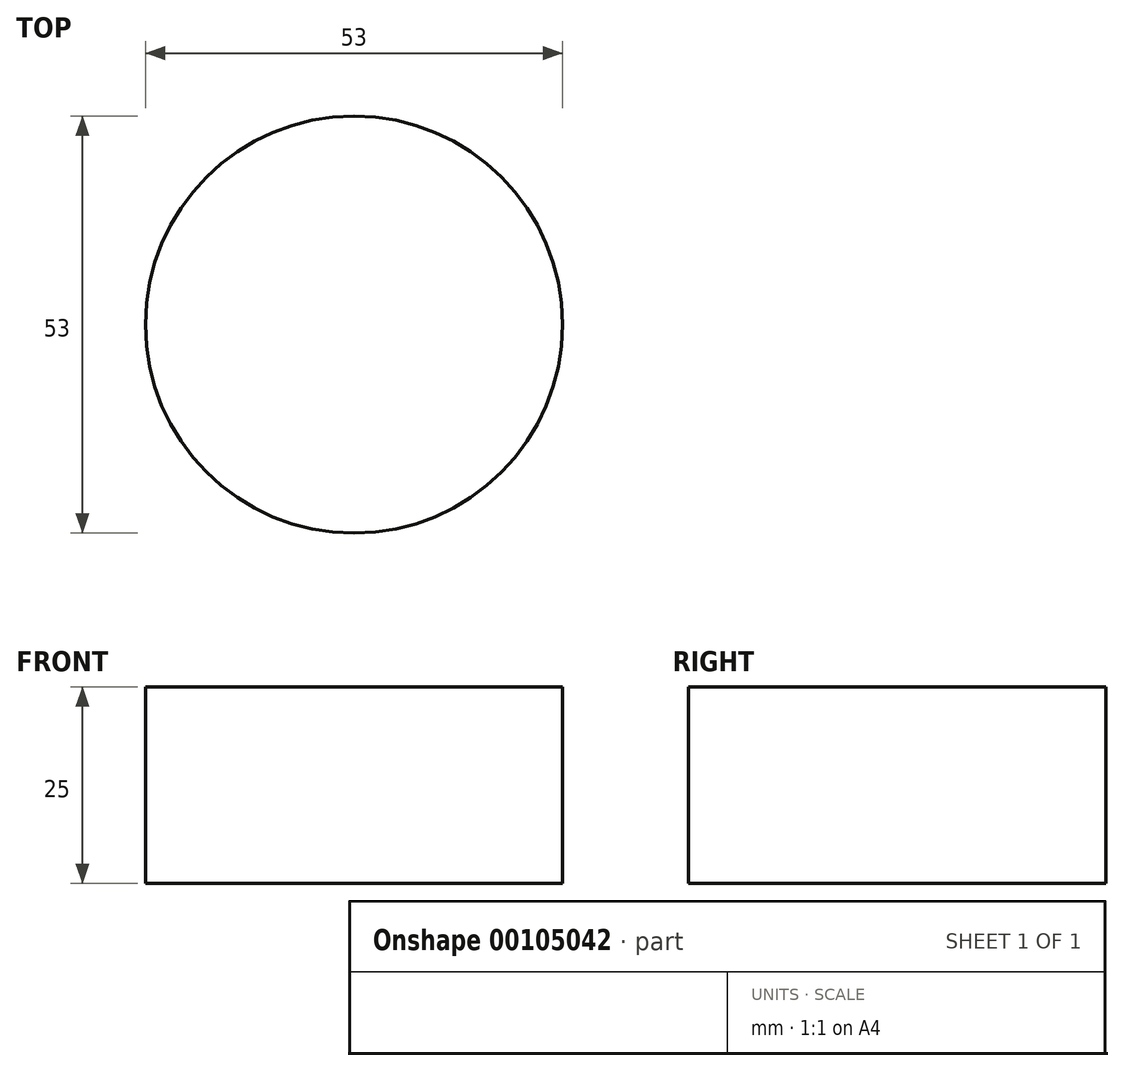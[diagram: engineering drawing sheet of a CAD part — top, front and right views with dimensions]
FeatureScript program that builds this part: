
annotation { "Feature Type Name" : "Feature", "Feature Type Description" : "" }
export const myFeature = defineFeature(function(context is Context, id is Id, definition is map)
    precondition{}
    {
        {
            assignVariable(context, id + "F0", {"name" : "F3", "anyValue" : 25});
        }
        {
            var Q0;
            Q0=qCreatedBy(makeId("Top.planeOp"),FACE);
            var sketch = newSketch(context, id + "F1", { "sketchPlane" : qUnion([Q0])});
            skCircle(sketch, "E0", {"center": v(390, 0) * mm, "radius": 26.5 * mm});
            skCircle(sketch, "E1", {"center": v(455, 0) * mm, "radius": 26.5 * mm});
            skCircle(sketch, "E2", {"center": v(520, 0) * mm, "radius": 26.5 * mm});
            skCircle(sketch, "E3", {"center": v(585, 0) * mm, "radius": 26.5 * mm});
            skCircle(sketch, "E4", {"center": v(650, 0) * mm, "radius": 26.5 * mm});
            skCircle(sketch, "E5", {"center": v(715, 0) * mm, "radius": 26.5 * mm});
            skCircle(sketch, "E6", {"center": v(780, 0) * mm, "radius": 26.5 * mm});
            skCircle(sketch, "E7", {"center": v(845, 0) * mm, "radius": 26.5 * mm});
            skCircle(sketch, "E8", {"center": v(910, 0) * mm, "radius": 26.5 * mm});
            skCircle(sketch, "E9", {"center": v(975, 0) * mm, "radius": 26.5 * mm});
            skCircle(sketch, "E10", {"center": v(1040, 0) * mm, "radius": 26.5 * mm});
            skCircle(sketch, "E11", {"center": v(1105, 0) * mm, "radius": 26.5 * mm});
            skCircle(sketch, "E12", {"center": v(1170, 0) * mm, "radius": 26.5 * mm});
            skCircle(sketch, "E13", {"center": v(1235, 0) * mm, "radius": 26.5 * mm});
            skCircle(sketch, "E14", {"center": v(1300, 0) * mm, "radius": 26.5 * mm});
            skCircle(sketch, "E15", {"center": v(1365, 0) * mm, "radius": 26.5 * mm});
            skCircle(sketch, "E16", {"center": v(1430, 0) * mm, "radius": 26.5 * mm});
            skCircle(sketch, "E17", {"center": v(1495, 0) * mm, "radius": 26.5 * mm});
            skCircle(sketch, "E18", {"center": v(1560, 0) * mm, "radius": 26.5 * mm});
            skCircle(sketch, "E19", {"center": v(422.5, 56.3) * mm, "radius": 26.5 * mm});
            skCircle(sketch, "E20", {"center": v(487.5, 56.3) * mm, "radius": 26.5 * mm});
            skCircle(sketch, "E21", {"center": v(552.5, 56.3) * mm, "radius": 26.5 * mm});
            skCircle(sketch, "E22", {"center": v(617.5, 56.3) * mm, "radius": 26.5 * mm});
            skCircle(sketch, "E23", {"center": v(682.5, 56.3) * mm, "radius": 26.5 * mm});
            skCircle(sketch, "E24", {"center": v(747.5, 56.3) * mm, "radius": 26.5 * mm});
            skCircle(sketch, "E25", {"center": v(812.5, 56.3) * mm, "radius": 26.5 * mm});
            skCircle(sketch, "E26", {"center": v(877.5, 56.3) * mm, "radius": 26.5 * mm});
            skCircle(sketch, "E27", {"center": v(942.5, 56.3) * mm, "radius": 26.5 * mm});
            skCircle(sketch, "E28", {"center": v(1007.5, 56.3) * mm, "radius": 26.5 * mm});
            skCircle(sketch, "E29", {"center": v(1072.5, 56.3) * mm, "radius": 26.5 * mm});
            skCircle(sketch, "E30", {"center": v(1137.5, 56.3) * mm, "radius": 26.5 * mm});
            skCircle(sketch, "E31", {"center": v(1202.5, 56.3) * mm, "radius": 26.5 * mm});
            skCircle(sketch, "E32", {"center": v(1267.5, 56.3) * mm, "radius": 26.5 * mm});
            skCircle(sketch, "E33", {"center": v(1332.5, 56.3) * mm, "radius": 26.5 * mm});
            skCircle(sketch, "E34", {"center": v(1397.5, 56.3) * mm, "radius": 26.5 * mm});
            skCircle(sketch, "E35", {"center": v(1462.5, 56.3) * mm, "radius": 26.5 * mm});
            skCircle(sketch, "E36", {"center": v(1527.5, 56.3) * mm, "radius": 26.5 * mm});
            skCircle(sketch, "E37", {"center": v(390, 112.58) * mm, "radius": 26.5 * mm});
            skCircle(sketch, "E38", {"center": v(455, 112.58) * mm, "radius": 26.5 * mm});
            skCircle(sketch, "E39", {"center": v(520, 112.58) * mm, "radius": 26.5 * mm});
            skCircle(sketch, "E40", {"center": v(585, 112.58) * mm, "radius": 26.5 * mm});
            skCircle(sketch, "E41", {"center": v(650, 112.58) * mm, "radius": 26.5 * mm});
            skCircle(sketch, "E42", {"center": v(715, 112.58) * mm, "radius": 26.5 * mm});
            skCircle(sketch, "E43", {"center": v(780, 112.58) * mm, "radius": 26.5 * mm});
            skCircle(sketch, "E44", {"center": v(845, 112.58) * mm, "radius": 26.5 * mm});
            skCircle(sketch, "E45", {"center": v(910, 112.58) * mm, "radius": 26.5 * mm});
            skCircle(sketch, "E46", {"center": v(975, 112.58) * mm, "radius": 26.5 * mm});
            skCircle(sketch, "E47", {"center": v(1040, 112.58) * mm, "radius": 26.5 * mm});
            skCircle(sketch, "E48", {"center": v(1105, 112.58) * mm, "radius": 26.5 * mm});
            skCircle(sketch, "E49", {"center": v(1170, 112.58) * mm, "radius": 26.5 * mm});
            skCircle(sketch, "E50", {"center": v(1235, 112.58) * mm, "radius": 26.5 * mm});
            skCircle(sketch, "E51", {"center": v(1300, 112.58) * mm, "radius": 26.5 * mm});
            skCircle(sketch, "E52", {"center": v(1365, 112.58) * mm, "radius": 26.5 * mm});
            skCircle(sketch, "E53", {"center": v(1430, 112.58) * mm, "radius": 26.5 * mm});
            skCircle(sketch, "E54", {"center": v(1495, 112.58) * mm, "radius": 26.5 * mm});
            skCircle(sketch, "E55", {"center": v(1560, 112.58) * mm, "radius": 26.5 * mm});
            skCircle(sketch, "E56", {"center": v(357.5, 168.87) * mm, "radius": 26.5 * mm});
            skCircle(sketch, "E57", {"center": v(422.5, 168.87) * mm, "radius": 26.5 * mm});
            skCircle(sketch, "E58", {"center": v(487.5, 168.87) * mm, "radius": 26.5 * mm});
            skCircle(sketch, "E59", {"center": v(552.5, 168.87) * mm, "radius": 26.5 * mm});
            skCircle(sketch, "E60", {"center": v(617.5, 168.87) * mm, "radius": 26.5 * mm});
            skCircle(sketch, "E61", {"center": v(682.5, 168.87) * mm, "radius": 26.5 * mm});
            skCircle(sketch, "E62", {"center": v(747.5, 168.87) * mm, "radius": 26.5 * mm});
            skCircle(sketch, "E63", {"center": v(812.5, 168.87) * mm, "radius": 26.5 * mm});
            skCircle(sketch, "E64", {"center": v(877.5, 168.87) * mm, "radius": 26.5 * mm});
            skCircle(sketch, "E65", {"center": v(942.5, 168.87) * mm, "radius": 26.5 * mm});
            skCircle(sketch, "E66", {"center": v(1007.5, 168.87) * mm, "radius": 26.5 * mm});
            skCircle(sketch, "E67", {"center": v(1072.5, 168.87) * mm, "radius": 26.5 * mm});
            skCircle(sketch, "E68", {"center": v(1137.5, 168.87) * mm, "radius": 26.5 * mm});
            skCircle(sketch, "E69", {"center": v(1202.5, 168.87) * mm, "radius": 26.5 * mm});
            skCircle(sketch, "E70", {"center": v(1267.5, 168.87) * mm, "radius": 26.5 * mm});
            skCircle(sketch, "E71", {"center": v(1332.5, 168.87) * mm, "radius": 26.5 * mm});
            skCircle(sketch, "E72", {"center": v(1397.5, 168.87) * mm, "radius": 26.5 * mm});
            skCircle(sketch, "E73", {"center": v(1462.5, 168.87) * mm, "radius": 26.5 * mm});
            skCircle(sketch, "E74", {"center": v(1527.5, 168.87) * mm, "radius": 26.5 * mm});
            skCircle(sketch, "E75", {"center": v(325, 225.17) * mm, "radius": 26.5 * mm});
            skCircle(sketch, "E76", {"center": v(390, 225.17) * mm, "radius": 26.5 * mm});
            skCircle(sketch, "E77", {"center": v(455, 225.17) * mm, "radius": 26.5 * mm});
            skCircle(sketch, "E78", {"center": v(520, 225.17) * mm, "radius": 26.5 * mm});
            skCircle(sketch, "E79", {"center": v(585, 225.17) * mm, "radius": 26.5 * mm});
            skCircle(sketch, "E80", {"center": v(650, 225.17) * mm, "radius": 26.5 * mm});
            skCircle(sketch, "E81", {"center": v(715, 225.17) * mm, "radius": 26.5 * mm});
            skCircle(sketch, "E82", {"center": v(780, 225.17) * mm, "radius": 26.5 * mm});
            skCircle(sketch, "E83", {"center": v(845, 225.17) * mm, "radius": 26.5 * mm});
            skCircle(sketch, "E84", {"center": v(910, 225.17) * mm, "radius": 26.5 * mm});
            skCircle(sketch, "E85", {"center": v(975, 225.17) * mm, "radius": 26.5 * mm});
            skCircle(sketch, "E86", {"center": v(1040, 225.17) * mm, "radius": 26.5 * mm});
            skCircle(sketch, "E87", {"center": v(1105, 225.17) * mm, "radius": 26.5 * mm});
            skCircle(sketch, "E88", {"center": v(1170, 225.17) * mm, "radius": 26.5 * mm});
            skCircle(sketch, "E89", {"center": v(1235, 225.17) * mm, "radius": 26.5 * mm});
            skCircle(sketch, "E90", {"center": v(1300, 225.17) * mm, "radius": 26.5 * mm});
            skCircle(sketch, "E91", {"center": v(1365, 225.17) * mm, "radius": 26.5 * mm});
            skCircle(sketch, "E92", {"center": v(1430, 225.17) * mm, "radius": 26.5 * mm});
            skCircle(sketch, "E93", {"center": v(1495, 225.17) * mm, "radius": 26.5 * mm});
            skCircle(sketch, "E94", {"center": v(1560, 225.17) * mm, "radius": 26.5 * mm});
            skCircle(sketch, "E95", {"center": v(292.5, 281.46) * mm, "radius": 26.5 * mm});
            skCircle(sketch, "E96", {"center": v(357.5, 281.46) * mm, "radius": 26.5 * mm});
            skCircle(sketch, "E97", {"center": v(422.5, 281.46) * mm, "radius": 26.5 * mm});
            skCircle(sketch, "E98", {"center": v(487.5, 281.46) * mm, "radius": 26.5 * mm});
            skCircle(sketch, "E99", {"center": v(552.5, 281.46) * mm, "radius": 26.5 * mm});
            skCircle(sketch, "E100", {"center": v(617.5, 281.46) * mm, "radius": 26.5 * mm});
            skCircle(sketch, "E101", {"center": v(682.5, 281.46) * mm, "radius": 26.5 * mm});
            skCircle(sketch, "E102", {"center": v(747.5, 281.46) * mm, "radius": 26.5 * mm});
            skCircle(sketch, "E103", {"center": v(812.5, 281.46) * mm, "radius": 26.5 * mm});
            skCircle(sketch, "E104", {"center": v(877.5, 281.46) * mm, "radius": 26.5 * mm});
            skCircle(sketch, "E105", {"center": v(942.5, 281.46) * mm, "radius": 26.5 * mm});
            skCircle(sketch, "E106", {"center": v(1007.5, 281.46) * mm, "radius": 26.5 * mm});
            skCircle(sketch, "E107", {"center": v(1072.5, 281.46) * mm, "radius": 26.5 * mm});
            skCircle(sketch, "E108", {"center": v(1137.5, 281.46) * mm, "radius": 26.5 * mm});
            skCircle(sketch, "E109", {"center": v(1202.5, 281.46) * mm, "radius": 26.5 * mm});
            skCircle(sketch, "E110", {"center": v(1267.5, 281.46) * mm, "radius": 26.5 * mm});
            skCircle(sketch, "E111", {"center": v(1332.5, 281.46) * mm, "radius": 26.5 * mm});
            skCircle(sketch, "E112", {"center": v(1397.5, 281.46) * mm, "radius": 26.5 * mm});
            skCircle(sketch, "E113", {"center": v(1462.5, 281.46) * mm, "radius": 26.5 * mm});
            skCircle(sketch, "E114", {"center": v(1527.5, 281.46) * mm, "radius": 26.5 * mm});
            skCircle(sketch, "E115", {"center": v(260, 337.75) * mm, "radius": 26.5 * mm});
            skCircle(sketch, "E116", {"center": v(325, 337.75) * mm, "radius": 26.5 * mm});
            skCircle(sketch, "E117", {"center": v(390, 337.75) * mm, "radius": 26.5 * mm});
            skCircle(sketch, "E118", {"center": v(455, 337.75) * mm, "radius": 26.5 * mm});
            skCircle(sketch, "E119", {"center": v(520, 337.75) * mm, "radius": 26.5 * mm});
            skCircle(sketch, "E120", {"center": v(585, 337.75) * mm, "radius": 26.5 * mm});
            skCircle(sketch, "E121", {"center": v(650, 337.75) * mm, "radius": 26.5 * mm});
            skCircle(sketch, "E122", {"center": v(715, 337.75) * mm, "radius": 26.5 * mm});
            skCircle(sketch, "E123", {"center": v(780, 337.75) * mm, "radius": 26.5 * mm});
            skCircle(sketch, "E124", {"center": v(845, 337.75) * mm, "radius": 26.5 * mm});
            skCircle(sketch, "E125", {"center": v(910, 337.75) * mm, "radius": 26.5 * mm});
            skCircle(sketch, "E126", {"center": v(975, 337.75) * mm, "radius": 26.5 * mm});
            skCircle(sketch, "E127", {"center": v(1040, 337.75) * mm, "radius": 26.5 * mm});
            skCircle(sketch, "E128", {"center": v(1105, 337.75) * mm, "radius": 26.5 * mm});
            skCircle(sketch, "E129", {"center": v(1170, 337.75) * mm, "radius": 26.5 * mm});
            skCircle(sketch, "E130", {"center": v(1235, 337.75) * mm, "radius": 26.5 * mm});
            skCircle(sketch, "E131", {"center": v(1300, 337.75) * mm, "radius": 26.5 * mm});
            skCircle(sketch, "E132", {"center": v(1365, 337.75) * mm, "radius": 26.5 * mm});
            skCircle(sketch, "E133", {"center": v(1430, 337.75) * mm, "radius": 26.5 * mm});
            skCircle(sketch, "E134", {"center": v(1495, 337.75) * mm, "radius": 26.5 * mm});
            skCircle(sketch, "E135", {"center": v(292.5, 394.04) * mm, "radius": 26.5 * mm});
            skCircle(sketch, "E136", {"center": v(357.5, 394.04) * mm, "radius": 26.5 * mm});
            skCircle(sketch, "E137", {"center": v(422.5, 394.04) * mm, "radius": 26.5 * mm});
            skCircle(sketch, "E138", {"center": v(487.5, 394.04) * mm, "radius": 26.5 * mm});
            skCircle(sketch, "E139", {"center": v(552.5, 394.04) * mm, "radius": 26.5 * mm});
            skCircle(sketch, "E140", {"center": v(617.5, 394.04) * mm, "radius": 26.5 * mm});
            skCircle(sketch, "E141", {"center": v(682.5, 394.04) * mm, "radius": 26.5 * mm});
            skCircle(sketch, "E142", {"center": v(747.5, 394.04) * mm, "radius": 26.5 * mm});
            skCircle(sketch, "E143", {"center": v(812.5, 394.04) * mm, "radius": 26.5 * mm});
            skCircle(sketch, "E144", {"center": v(877.5, 394.04) * mm, "radius": 26.5 * mm});
            skCircle(sketch, "E145", {"center": v(942.5, 394.04) * mm, "radius": 26.5 * mm});
            skCircle(sketch, "E146", {"center": v(1007.5, 394.04) * mm, "radius": 26.5 * mm});
            skCircle(sketch, "E147", {"center": v(1072.5, 394.04) * mm, "radius": 26.5 * mm});
            skCircle(sketch, "E148", {"center": v(1137.5, 394.04) * mm, "radius": 26.5 * mm});
            skCircle(sketch, "E149", {"center": v(1202.5, 394.04) * mm, "radius": 26.5 * mm});
            skCircle(sketch, "E150", {"center": v(1267.5, 394.04) * mm, "radius": 26.5 * mm});
            skCircle(sketch, "E151", {"center": v(1332.5, 394.04) * mm, "radius": 26.5 * mm});
            skCircle(sketch, "E152", {"center": v(1397.5, 394.04) * mm, "radius": 26.5 * mm});
            skCircle(sketch, "E153", {"center": v(1462.5, 394.04) * mm, "radius": 26.5 * mm});
            skCircle(sketch, "E154", {"center": v(1527.5, 394.04) * mm, "radius": 26.5 * mm});
            skCircle(sketch, "E155", {"center": v(325, 450.33) * mm, "radius": 26.5 * mm});
            skCircle(sketch, "E156", {"center": v(390, 450.33) * mm, "radius": 26.5 * mm});
            skCircle(sketch, "E157", {"center": v(455, 450.33) * mm, "radius": 26.5 * mm});
            skCircle(sketch, "E158", {"center": v(520, 450.33) * mm, "radius": 26.5 * mm});
            skCircle(sketch, "E159", {"center": v(585, 450.33) * mm, "radius": 26.5 * mm});
            skCircle(sketch, "E160", {"center": v(650, 450.33) * mm, "radius": 26.5 * mm});
            skCircle(sketch, "E161", {"center": v(715, 450.33) * mm, "radius": 26.5 * mm});
            skCircle(sketch, "E162", {"center": v(780, 450.33) * mm, "radius": 26.5 * mm});
            skCircle(sketch, "E163", {"center": v(845, 450.33) * mm, "radius": 26.5 * mm});
            skCircle(sketch, "E164", {"center": v(910, 450.33) * mm, "radius": 26.5 * mm});
            skCircle(sketch, "E165", {"center": v(975, 450.33) * mm, "radius": 26.5 * mm});
            skCircle(sketch, "E166", {"center": v(1040, 450.33) * mm, "radius": 26.5 * mm});
            skCircle(sketch, "E167", {"center": v(1105, 450.33) * mm, "radius": 26.5 * mm});
            skCircle(sketch, "E168", {"center": v(1170, 450.33) * mm, "radius": 26.5 * mm});
            skCircle(sketch, "E169", {"center": v(1235, 450.33) * mm, "radius": 26.5 * mm});
            skCircle(sketch, "E170", {"center": v(1300, 450.33) * mm, "radius": 26.5 * mm});
            skCircle(sketch, "E171", {"center": v(1365, 450.33) * mm, "radius": 26.5 * mm});
            skCircle(sketch, "E172", {"center": v(1430, 450.33) * mm, "radius": 26.5 * mm});
            skCircle(sketch, "E173", {"center": v(1495, 450.33) * mm, "radius": 26.5 * mm});
            skCircle(sketch, "E174", {"center": v(357.5, 506.62) * mm, "radius": 26.5 * mm});
            skCircle(sketch, "E175", {"center": v(422.5, 506.62) * mm, "radius": 26.5 * mm});
            skCircle(sketch, "E176", {"center": v(487.5, 506.62) * mm, "radius": 26.5 * mm});
            skCircle(sketch, "E177", {"center": v(552.5, 506.62) * mm, "radius": 26.5 * mm});
            skCircle(sketch, "E178", {"center": v(617.5, 506.62) * mm, "radius": 26.5 * mm});
            skCircle(sketch, "E179", {"center": v(682.5, 506.62) * mm, "radius": 26.5 * mm});
            skCircle(sketch, "E180", {"center": v(747.5, 506.62) * mm, "radius": 26.5 * mm});
            skCircle(sketch, "E181", {"center": v(812.5, 506.62) * mm, "radius": 26.5 * mm});
            skCircle(sketch, "E182", {"center": v(877.5, 506.62) * mm, "radius": 26.5 * mm});
            skCircle(sketch, "E183", {"center": v(1072.5, 506.62) * mm, "radius": 26.5 * mm});
            skCircle(sketch, "E184", {"center": v(1137.5, 506.62) * mm, "radius": 26.5 * mm});
            skCircle(sketch, "E185", {"center": v(1202.5, 506.62) * mm, "radius": 26.5 * mm});
            skCircle(sketch, "E186", {"center": v(1267.5, 506.62) * mm, "radius": 26.5 * mm});
            skCircle(sketch, "E187", {"center": v(1332.5, 506.62) * mm, "radius": 26.5 * mm});
            skCircle(sketch, "E188", {"center": v(1397.5, 506.62) * mm, "radius": 26.5 * mm});
            skCircle(sketch, "E189", {"center": v(1462.5, 506.62) * mm, "radius": 26.5 * mm});
            skCircle(sketch, "E190", {"center": v(390, 562.92) * mm, "radius": 26.5 * mm});
            skCircle(sketch, "E191", {"center": v(455, 562.92) * mm, "radius": 26.5 * mm});
            skCircle(sketch, "E192", {"center": v(520, 562.92) * mm, "radius": 26.5 * mm});
            skCircle(sketch, "E193", {"center": v(585, 562.92) * mm, "radius": 26.5 * mm});
            skCircle(sketch, "E194", {"center": v(650, 562.92) * mm, "radius": 26.5 * mm});
            skCircle(sketch, "E195", {"center": v(715, 562.92) * mm, "radius": 26.5 * mm});
            skCircle(sketch, "E196", {"center": v(780, 562.92) * mm, "radius": 26.5 * mm});
            skCircle(sketch, "E197", {"center": v(845, 562.92) * mm, "radius": 26.5 * mm});
            skCircle(sketch, "E198", {"center": v(1105, 562.92) * mm, "radius": 26.5 * mm});
            skCircle(sketch, "E199", {"center": v(1170, 562.92) * mm, "radius": 26.5 * mm});
            skCircle(sketch, "E200", {"center": v(1235, 562.92) * mm, "radius": 26.5 * mm});
            skCircle(sketch, "E201", {"center": v(1300, 562.92) * mm, "radius": 26.5 * mm});
            skCircle(sketch, "E202", {"center": v(1365, 562.92) * mm, "radius": 26.5 * mm});
            skCircle(sketch, "E203", {"center": v(1430, 562.92) * mm, "radius": 26.5 * mm});
            skCircle(sketch, "E204", {"center": v(422.5, 619.2) * mm, "radius": 26.5 * mm});
            skCircle(sketch, "E205", {"center": v(487.5, 619.2) * mm, "radius": 26.5 * mm});
            skCircle(sketch, "E206", {"center": v(552.5, 619.2) * mm, "radius": 26.5 * mm});
            skCircle(sketch, "E207", {"center": v(617.5, 619.2) * mm, "radius": 26.5 * mm});
            skCircle(sketch, "E208", {"center": v(682.5, 619.2) * mm, "radius": 26.5 * mm});
            skCircle(sketch, "E209", {"center": v(747.5, 619.2) * mm, "radius": 26.5 * mm});
            skCircle(sketch, "E210", {"center": v(812.5, 619.2) * mm, "radius": 26.5 * mm});
            skCircle(sketch, "E211", {"center": v(877.5, 619.2) * mm, "radius": 26.5 * mm});
            skCircle(sketch, "E212", {"center": v(1072.5, 619.2) * mm, "radius": 26.5 * mm});
            skCircle(sketch, "E213", {"center": v(1137.5, 619.2) * mm, "radius": 26.5 * mm});
            skCircle(sketch, "E214", {"center": v(1202.5, 619.2) * mm, "radius": 26.5 * mm});
            skCircle(sketch, "E215", {"center": v(1267.5, 619.2) * mm, "radius": 26.5 * mm});
            skCircle(sketch, "E216", {"center": v(1332.5, 619.2) * mm, "radius": 26.5 * mm});
            skCircle(sketch, "E217", {"center": v(1397.5, 619.2) * mm, "radius": 26.5 * mm});
            skCircle(sketch, "E218", {"center": v(455, 675.5) * mm, "radius": 26.5 * mm});
            skCircle(sketch, "E219", {"center": v(520, 675.5) * mm, "radius": 26.5 * mm});
            skCircle(sketch, "E220", {"center": v(585, 675.5) * mm, "radius": 26.5 * mm});
            skCircle(sketch, "E221", {"center": v(650, 675.5) * mm, "radius": 26.5 * mm});
            skCircle(sketch, "E222", {"center": v(715, 675.5) * mm, "radius": 26.5 * mm});
            skCircle(sketch, "E223", {"center": v(780, 675.5) * mm, "radius": 26.5 * mm});
            skCircle(sketch, "E224", {"center": v(845, 675.5) * mm, "radius": 26.5 * mm});
            skCircle(sketch, "E225", {"center": v(910, 675.5) * mm, "radius": 26.5 * mm});
            skCircle(sketch, "E226", {"center": v(975, 675.5) * mm, "radius": 26.5 * mm});
            skCircle(sketch, "E227", {"center": v(1040, 675.5) * mm, "radius": 26.5 * mm});
            skCircle(sketch, "E228", {"center": v(1105, 675.5) * mm, "radius": 26.5 * mm});
            skCircle(sketch, "E229", {"center": v(1170, 675.5) * mm, "radius": 26.5 * mm});
            skCircle(sketch, "E230", {"center": v(1235, 675.5) * mm, "radius": 26.5 * mm});
            skCircle(sketch, "E231", {"center": v(1300, 675.5) * mm, "radius": 26.5 * mm});
            skCircle(sketch, "E232", {"center": v(1365, 675.5) * mm, "radius": 26.5 * mm});
            skCircle(sketch, "E233", {"center": v(487.5, 731.8) * mm, "radius": 26.5 * mm});
            skCircle(sketch, "E234", {"center": v(552.5, 731.8) * mm, "radius": 26.5 * mm});
            skCircle(sketch, "E235", {"center": v(617.5, 731.8) * mm, "radius": 26.5 * mm});
            skCircle(sketch, "E236", {"center": v(682.5, 731.8) * mm, "radius": 26.5 * mm});
            skCircle(sketch, "E237", {"center": v(747.5, 731.8) * mm, "radius": 26.5 * mm});
            skCircle(sketch, "E238", {"center": v(812.5, 731.8) * mm, "radius": 26.5 * mm});
            skCircle(sketch, "E239", {"center": v(877.5, 731.8) * mm, "radius": 26.5 * mm});
            skCircle(sketch, "E240", {"center": v(942.5, 731.8) * mm, "radius": 26.5 * mm});
            skCircle(sketch, "E241", {"center": v(1007.5, 731.8) * mm, "radius": 26.5 * mm});
            skCircle(sketch, "E242", {"center": v(1072.5, 731.8) * mm, "radius": 26.5 * mm});
            skCircle(sketch, "E243", {"center": v(1137.5, 731.8) * mm, "radius": 26.5 * mm});
            skCircle(sketch, "E244", {"center": v(1202.5, 731.8) * mm, "radius": 26.5 * mm});
            skCircle(sketch, "E245", {"center": v(1267.5, 731.8) * mm, "radius": 26.5 * mm});
            skCircle(sketch, "E246", {"center": v(1332.5, 731.8) * mm, "radius": 26.5 * mm});
            skCircle(sketch, "E247", {"center": v(1397.5, 731.8) * mm, "radius": 26.5 * mm});
            skCircle(sketch, "E248", {"center": v(520, 788.08) * mm, "radius": 26.5 * mm});
            skCircle(sketch, "E249", {"center": v(585, 788.08) * mm, "radius": 26.5 * mm});
            skCircle(sketch, "E250", {"center": v(650, 788.08) * mm, "radius": 26.5 * mm});
            skCircle(sketch, "E251", {"center": v(715, 788.08) * mm, "radius": 26.5 * mm});
            skCircle(sketch, "E252", {"center": v(780, 788.08) * mm, "radius": 26.5 * mm});
            skCircle(sketch, "E253", {"center": v(845, 788.08) * mm, "radius": 26.5 * mm});
            skCircle(sketch, "E254", {"center": v(910, 788.08) * mm, "radius": 26.5 * mm});
            skCircle(sketch, "E255", {"center": v(975, 788.08) * mm, "radius": 26.5 * mm});
            skCircle(sketch, "E256", {"center": v(1040, 788.08) * mm, "radius": 26.5 * mm});
            skCircle(sketch, "E257", {"center": v(1105, 788.08) * mm, "radius": 26.5 * mm});
            skCircle(sketch, "E258", {"center": v(1170, 788.08) * mm, "radius": 26.5 * mm});
            skCircle(sketch, "E259", {"center": v(1235, 788.08) * mm, "radius": 26.5 * mm});
            skCircle(sketch, "E260", {"center": v(1300, 788.08) * mm, "radius": 26.5 * mm});
            skCircle(sketch, "E261", {"center": v(1365, 788.08) * mm, "radius": 26.5 * mm});
            skCircle(sketch, "E262", {"center": v(552.5, 844.37) * mm, "radius": 26.5 * mm});
            skCircle(sketch, "E263", {"center": v(617.5, 844.37) * mm, "radius": 26.5 * mm});
            skCircle(sketch, "E264", {"center": v(682.5, 844.37) * mm, "radius": 26.5 * mm});
            skCircle(sketch, "E265", {"center": v(747.5, 844.37) * mm, "radius": 26.5 * mm});
            skCircle(sketch, "E266", {"center": v(812.5, 844.37) * mm, "radius": 26.5 * mm});
            skCircle(sketch, "E267", {"center": v(877.5, 844.37) * mm, "radius": 26.5 * mm});
            skCircle(sketch, "E268", {"center": v(942.5, 844.37) * mm, "radius": 26.5 * mm});
            skCircle(sketch, "E269", {"center": v(1007.5, 844.37) * mm, "radius": 26.5 * mm});
            skCircle(sketch, "E270", {"center": v(1072.5, 844.37) * mm, "radius": 26.5 * mm});
            skCircle(sketch, "E271", {"center": v(1137.5, 844.37) * mm, "radius": 26.5 * mm});
            skCircle(sketch, "E272", {"center": v(1202.5, 844.37) * mm, "radius": 26.5 * mm});
            skCircle(sketch, "E273", {"center": v(1267.5, 844.37) * mm, "radius": 26.5 * mm});
            skCircle(sketch, "E274", {"center": v(1332.5, 844.37) * mm, "radius": 26.5 * mm});
            skCircle(sketch, "E275", {"center": v(585, 900.67) * mm, "radius": 26.5 * mm});
            skCircle(sketch, "E276", {"center": v(650, 900.67) * mm, "radius": 26.5 * mm});
            skCircle(sketch, "E277", {"center": v(715, 900.67) * mm, "radius": 26.5 * mm});
            skCircle(sketch, "E278", {"center": v(780, 900.67) * mm, "radius": 26.5 * mm});
            skCircle(sketch, "E279", {"center": v(845, 900.67) * mm, "radius": 26.5 * mm});
            skCircle(sketch, "E280", {"center": v(910, 900.67) * mm, "radius": 26.5 * mm});
            skCircle(sketch, "E281", {"center": v(975, 900.67) * mm, "radius": 26.5 * mm});
            skCircle(sketch, "E282", {"center": v(1040, 900.67) * mm, "radius": 26.5 * mm});
            skCircle(sketch, "E283", {"center": v(1105, 900.67) * mm, "radius": 26.5 * mm});
            skCircle(sketch, "E284", {"center": v(1170, 900.67) * mm, "radius": 26.5 * mm});
            skCircle(sketch, "E285", {"center": v(1235, 900.67) * mm, "radius": 26.5 * mm});
            skCircle(sketch, "E286", {"center": v(617.5, 956.96) * mm, "radius": 26.5 * mm});
            skCircle(sketch, "E287", {"center": v(682.5, 956.96) * mm, "radius": 26.5 * mm});
            skCircle(sketch, "E288", {"center": v(747.5, 956.96) * mm, "radius": 26.5 * mm});
            skCircle(sketch, "E289", {"center": v(812.5, 956.96) * mm, "radius": 26.5 * mm});
            skCircle(sketch, "E290", {"center": v(877.5, 956.96) * mm, "radius": 26.5 * mm});
            skCircle(sketch, "E291", {"center": v(942.5, 956.96) * mm, "radius": 26.5 * mm});
            skCircle(sketch, "E292", {"center": v(1007.5, 956.96) * mm, "radius": 26.5 * mm});
            skCircle(sketch, "E293", {"center": v(1072.5, 956.96) * mm, "radius": 26.5 * mm});
            skCircle(sketch, "E294", {"center": v(1137.5, 956.96) * mm, "radius": 26.5 * mm});
            skCircle(sketch, "E295", {"center": v(1202.5, 956.96) * mm, "radius": 26.5 * mm});
            skCircle(sketch, "E296", {"center": v(650, 1013.25) * mm, "radius": 26.5 * mm});
            skCircle(sketch, "E297", {"center": v(715, 1013.25) * mm, "radius": 26.5 * mm});
            skCircle(sketch, "E298", {"center": v(780, 1013.25) * mm, "radius": 26.5 * mm});
            skCircle(sketch, "E299", {"center": v(845, 1013.25) * mm, "radius": 26.5 * mm});
            skCircle(sketch, "E300", {"center": v(910, 1013.25) * mm, "radius": 26.5 * mm});
            skCircle(sketch, "E301", {"center": v(975, 1013.25) * mm, "radius": 26.5 * mm});
            skCircle(sketch, "E302", {"center": v(1040, 1013.25) * mm, "radius": 26.5 * mm});
            skCircle(sketch, "E303", {"center": v(1105, 1013.25) * mm, "radius": 26.5 * mm});
            skCircle(sketch, "E304", {"center": v(1170, 1013.25) * mm, "radius": 26.5 * mm});
            skCircle(sketch, "E305", {"center": v(682.5, 1069.54) * mm, "radius": 26.5 * mm});
            skCircle(sketch, "E306", {"center": v(747.5, 1069.54) * mm, "radius": 26.5 * mm});
            skCircle(sketch, "E307", {"center": v(812.5, 1069.54) * mm, "radius": 26.5 * mm});
            skCircle(sketch, "E308", {"center": v(877.5, 1069.54) * mm, "radius": 26.5 * mm});
            skCircle(sketch, "E309", {"center": v(942.5, 1069.54) * mm, "radius": 26.5 * mm});
            skCircle(sketch, "E310", {"center": v(1007.5, 1069.54) * mm, "radius": 26.5 * mm});
            skCircle(sketch, "E311", {"center": v(1072.5, 1069.54) * mm, "radius": 26.5 * mm});
            skCircle(sketch, "E312", {"center": v(1137.5, 1069.54) * mm, "radius": 26.5 * mm});
            skCircle(sketch, "E313", {"center": v(715, 1125.83) * mm, "radius": 26.5 * mm});
            skCircle(sketch, "E314", {"center": v(780, 1125.83) * mm, "radius": 26.5 * mm});
            skCircle(sketch, "E315", {"center": v(845, 1125.83) * mm, "radius": 26.5 * mm});
            skCircle(sketch, "E316", {"center": v(910, 1125.83) * mm, "radius": 26.5 * mm});
            skCircle(sketch, "E317", {"center": v(975, 1125.83) * mm, "radius": 26.5 * mm});
            skCircle(sketch, "E318", {"center": v(1040, 1125.83) * mm, "radius": 26.5 * mm});
            skCircle(sketch, "E319", {"center": v(1105, 1125.83) * mm, "radius": 26.5 * mm});
            skCircle(sketch, "E320", {"center": v(747.5, 1182.12) * mm, "radius": 26.5 * mm});
            skCircle(sketch, "E321", {"center": v(812.5, 1182.12) * mm, "radius": 26.5 * mm});
            skCircle(sketch, "E322", {"center": v(877.5, 1182.12) * mm, "radius": 26.5 * mm});
            skCircle(sketch, "E323", {"center": v(942.5, 1182.12) * mm, "radius": 26.5 * mm});
            skCircle(sketch, "E324", {"center": v(1007.5, 1182.12) * mm, "radius": 26.5 * mm});
            skCircle(sketch, "E325", {"center": v(780, 1238.42) * mm, "radius": 26.5 * mm});
            skCircle(sketch, "E326", {"center": v(845, 1238.42) * mm, "radius": 26.5 * mm});
            skCircle(sketch, "E327", {"center": v(910, 1238.42) * mm, "radius": 26.5 * mm});
            skCircle(sketch, "E328", {"center": v(975, 1238.42) * mm, "radius": 26.5 * mm});
            skCircle(sketch, "E329", {"center": v(812.5, 1294.7) * mm, "radius": 26.5 * mm});
            skCircle(sketch, "E330", {"center": v(877.5, 1294.7) * mm, "radius": 26.5 * mm});
            skCircle(sketch, "E331", {"center": v(0, 0) * mm, "radius": 304.8 * mm, "construction": true});
            skCircle(sketch, "E332", {"center": v(0, 0) * mm, "radius": 1655.21 * mm, "construction": true});
            skCircle(sketch, "E333", {"center": v(975, 562.92) * mm, "radius": 58 * mm});
            skCircle(sketch, "E334", {"center": v(195, 337.75) * mm, "radius": 26.5 * mm});
            skCircle(sketch, "E335", {"center": v(227.5, 394.04) * mm, "radius": 26.5 * mm});
            skCircle(sketch, "E336", {"center": v(260, 450.33) * mm, "radius": 26.5 * mm});
            skCircle(sketch, "E337", {"center": v(292.5, 506.62) * mm, "radius": 26.5 * mm});
            skCircle(sketch, "E338", {"center": v(325, 562.92) * mm, "radius": 26.5 * mm});
            skCircle(sketch, "E339", {"center": v(357.5, 619.2) * mm, "radius": 26.5 * mm});
            skCircle(sketch, "E340", {"center": v(390, 675.5) * mm, "radius": 26.5 * mm});
            skCircle(sketch, "E341", {"center": v(422.5, 731.8) * mm, "radius": 26.5 * mm});
            skCircle(sketch, "E342", {"center": v(455, 788.08) * mm, "radius": 26.5 * mm});
            skCircle(sketch, "E343", {"center": v(487.5, 844.37) * mm, "radius": 26.5 * mm});
            skCircle(sketch, "E344", {"center": v(520, 900.67) * mm, "radius": 26.5 * mm});
            skCircle(sketch, "E345", {"center": v(552.5, 956.96) * mm, "radius": 26.5 * mm});
            skCircle(sketch, "E346", {"center": v(585, 1013.25) * mm, "radius": 26.5 * mm});
            skCircle(sketch, "E347", {"center": v(617.5, 1069.54) * mm, "radius": 26.5 * mm});
            skCircle(sketch, "E348", {"center": v(650, 1125.83) * mm, "radius": 26.5 * mm});
            skCircle(sketch, "E349", {"center": v(682.5, 1182.12) * mm, "radius": 26.5 * mm});
            skCircle(sketch, "E350", {"center": v(715, 1238.42) * mm, "radius": 26.5 * mm});
            skCircle(sketch, "E351", {"center": v(747.5, 1294.7) * mm, "radius": 26.5 * mm});
            skCircle(sketch, "E352", {"center": v(780, 1351) * mm, "radius": 26.5 * mm});
            skCircle(sketch, "E353", {"center": v(162.5, 394.04) * mm, "radius": 26.5 * mm});
            skCircle(sketch, "E354", {"center": v(195, 450.33) * mm, "radius": 26.5 * mm});
            skCircle(sketch, "E355", {"center": v(227.5, 506.62) * mm, "radius": 26.5 * mm});
            skCircle(sketch, "E356", {"center": v(260, 562.92) * mm, "radius": 26.5 * mm});
            skCircle(sketch, "E357", {"center": v(292.5, 619.2) * mm, "radius": 26.5 * mm});
            skCircle(sketch, "E358", {"center": v(325, 675.5) * mm, "radius": 26.5 * mm});
            skCircle(sketch, "E359", {"center": v(357.5, 731.8) * mm, "radius": 26.5 * mm});
            skCircle(sketch, "E360", {"center": v(390, 788.08) * mm, "radius": 26.5 * mm});
            skCircle(sketch, "E361", {"center": v(422.5, 844.37) * mm, "radius": 26.5 * mm});
            skCircle(sketch, "E362", {"center": v(455, 900.67) * mm, "radius": 26.5 * mm});
            skCircle(sketch, "E363", {"center": v(487.5, 956.96) * mm, "radius": 26.5 * mm});
            skCircle(sketch, "E364", {"center": v(520, 1013.25) * mm, "radius": 26.5 * mm});
            skCircle(sketch, "E365", {"center": v(552.5, 1069.54) * mm, "radius": 26.5 * mm});
            skCircle(sketch, "E366", {"center": v(585, 1125.83) * mm, "radius": 26.5 * mm});
            skCircle(sketch, "E367", {"center": v(617.5, 1182.12) * mm, "radius": 26.5 * mm});
            skCircle(sketch, "E368", {"center": v(650, 1238.42) * mm, "radius": 26.5 * mm});
            skCircle(sketch, "E369", {"center": v(682.5, 1294.7) * mm, "radius": 26.5 * mm});
            skCircle(sketch, "E370", {"center": v(715, 1351) * mm, "radius": 26.5 * mm});
            skCircle(sketch, "E371", {"center": v(97.5, 394.04) * mm, "radius": 26.5 * mm});
            skCircle(sketch, "E372", {"center": v(130, 450.33) * mm, "radius": 26.5 * mm});
            skCircle(sketch, "E373", {"center": v(162.5, 506.62) * mm, "radius": 26.5 * mm});
            skCircle(sketch, "E374", {"center": v(195, 562.92) * mm, "radius": 26.5 * mm});
            skCircle(sketch, "E375", {"center": v(227.5, 619.2) * mm, "radius": 26.5 * mm});
            skCircle(sketch, "E376", {"center": v(260, 675.5) * mm, "radius": 26.5 * mm});
            skCircle(sketch, "E377", {"center": v(292.5, 731.8) * mm, "radius": 26.5 * mm});
            skCircle(sketch, "E378", {"center": v(325, 788.08) * mm, "radius": 26.5 * mm});
            skCircle(sketch, "E379", {"center": v(357.5, 844.37) * mm, "radius": 26.5 * mm});
            skCircle(sketch, "E380", {"center": v(390, 900.67) * mm, "radius": 26.5 * mm});
            skCircle(sketch, "E381", {"center": v(422.5, 956.96) * mm, "radius": 26.5 * mm});
            skCircle(sketch, "E382", {"center": v(455, 1013.25) * mm, "radius": 26.5 * mm});
            skCircle(sketch, "E383", {"center": v(487.5, 1069.54) * mm, "radius": 26.5 * mm});
            skCircle(sketch, "E384", {"center": v(520, 1125.83) * mm, "radius": 26.5 * mm});
            skCircle(sketch, "E385", {"center": v(552.5, 1182.12) * mm, "radius": 26.5 * mm});
            skCircle(sketch, "E386", {"center": v(585, 1238.42) * mm, "radius": 26.5 * mm});
            skCircle(sketch, "E387", {"center": v(617.5, 1294.7) * mm, "radius": 26.5 * mm});
            skCircle(sketch, "E388", {"center": v(650, 1351) * mm, "radius": 26.5 * mm});
            skCircle(sketch, "E389", {"center": v(682.5, 1407.3) * mm, "radius": 26.5 * mm});
            skCircle(sketch, "E390", {"center": v(32.5, 394.04) * mm, "radius": 26.5 * mm});
            skCircle(sketch, "E391", {"center": v(65, 450.33) * mm, "radius": 26.5 * mm});
            skCircle(sketch, "E392", {"center": v(97.5, 506.62) * mm, "radius": 26.5 * mm});
            skCircle(sketch, "E393", {"center": v(130, 562.92) * mm, "radius": 26.5 * mm});
            skCircle(sketch, "E394", {"center": v(162.5, 619.2) * mm, "radius": 26.5 * mm});
            skCircle(sketch, "E395", {"center": v(195, 675.5) * mm, "radius": 26.5 * mm});
            skCircle(sketch, "E396", {"center": v(227.5, 731.8) * mm, "radius": 26.5 * mm});
            skCircle(sketch, "E397", {"center": v(260, 788.08) * mm, "radius": 26.5 * mm});
            skCircle(sketch, "E398", {"center": v(292.5, 844.37) * mm, "radius": 26.5 * mm});
            skCircle(sketch, "E399", {"center": v(325, 900.67) * mm, "radius": 26.5 * mm});
            skCircle(sketch, "E400", {"center": v(357.5, 956.96) * mm, "radius": 26.5 * mm});
            skCircle(sketch, "E401", {"center": v(390, 1013.25) * mm, "radius": 26.5 * mm});
            skCircle(sketch, "E402", {"center": v(422.5, 1069.54) * mm, "radius": 26.5 * mm});
            skCircle(sketch, "E403", {"center": v(455, 1125.83) * mm, "radius": 26.5 * mm});
            skCircle(sketch, "E404", {"center": v(487.5, 1182.12) * mm, "radius": 26.5 * mm});
            skCircle(sketch, "E405", {"center": v(520, 1238.42) * mm, "radius": 26.5 * mm});
            skCircle(sketch, "E406", {"center": v(552.5, 1294.7) * mm, "radius": 26.5 * mm});
            skCircle(sketch, "E407", {"center": v(585, 1351) * mm, "radius": 26.5 * mm});
            skCircle(sketch, "E408", {"center": v(617.5, 1407.3) * mm, "radius": 26.5 * mm});
            skCircle(sketch, "E409", {"center": v(-32.5, 394.04) * mm, "radius": 26.5 * mm});
            skCircle(sketch, "E410", {"center": v(0, 450.33) * mm, "radius": 26.5 * mm});
            skCircle(sketch, "E411", {"center": v(32.5, 506.62) * mm, "radius": 26.5 * mm});
            skCircle(sketch, "E412", {"center": v(65, 562.92) * mm, "radius": 26.5 * mm});
            skCircle(sketch, "E413", {"center": v(97.5, 619.2) * mm, "radius": 26.5 * mm});
            skCircle(sketch, "E414", {"center": v(130, 675.5) * mm, "radius": 26.5 * mm});
            skCircle(sketch, "E415", {"center": v(162.5, 731.8) * mm, "radius": 26.5 * mm});
            skCircle(sketch, "E416", {"center": v(195, 788.08) * mm, "radius": 26.5 * mm});
            skCircle(sketch, "E417", {"center": v(227.5, 844.37) * mm, "radius": 26.5 * mm});
            skCircle(sketch, "E418", {"center": v(260, 900.67) * mm, "radius": 26.5 * mm});
            skCircle(sketch, "E419", {"center": v(292.5, 956.96) * mm, "radius": 26.5 * mm});
            skCircle(sketch, "E420", {"center": v(325, 1013.25) * mm, "radius": 26.5 * mm});
            skCircle(sketch, "E421", {"center": v(357.5, 1069.54) * mm, "radius": 26.5 * mm});
            skCircle(sketch, "E422", {"center": v(390, 1125.83) * mm, "radius": 26.5 * mm});
            skCircle(sketch, "E423", {"center": v(422.5, 1182.12) * mm, "radius": 26.5 * mm});
            skCircle(sketch, "E424", {"center": v(455, 1238.42) * mm, "radius": 26.5 * mm});
            skCircle(sketch, "E425", {"center": v(487.5, 1294.7) * mm, "radius": 26.5 * mm});
            skCircle(sketch, "E426", {"center": v(520, 1351) * mm, "radius": 26.5 * mm});
            skCircle(sketch, "E427", {"center": v(552.5, 1407.3) * mm, "radius": 26.5 * mm});
            skCircle(sketch, "E428", {"center": v(585, 1463.58) * mm, "radius": 26.5 * mm});
            skCircle(sketch, "E429", {"center": v(-97.5, 394.04) * mm, "radius": 26.5 * mm});
            skCircle(sketch, "E430", {"center": v(-65, 450.33) * mm, "radius": 26.5 * mm});
            skCircle(sketch, "E431", {"center": v(-32.5, 506.62) * mm, "radius": 26.5 * mm});
            skCircle(sketch, "E432", {"center": v(0, 562.92) * mm, "radius": 26.5 * mm});
            skCircle(sketch, "E433", {"center": v(32.5, 619.2) * mm, "radius": 26.5 * mm});
            skCircle(sketch, "E434", {"center": v(65, 675.5) * mm, "radius": 26.5 * mm});
            skCircle(sketch, "E435", {"center": v(97.5, 731.8) * mm, "radius": 26.5 * mm});
            skCircle(sketch, "E436", {"center": v(130, 788.08) * mm, "radius": 26.5 * mm});
            skCircle(sketch, "E437", {"center": v(162.5, 844.37) * mm, "radius": 26.5 * mm});
            skCircle(sketch, "E438", {"center": v(195, 900.67) * mm, "radius": 26.5 * mm});
            skCircle(sketch, "E439", {"center": v(227.5, 956.96) * mm, "radius": 26.5 * mm});
            skCircle(sketch, "E440", {"center": v(260, 1013.25) * mm, "radius": 26.5 * mm});
            skCircle(sketch, "E441", {"center": v(292.5, 1069.54) * mm, "radius": 26.5 * mm});
            skCircle(sketch, "E442", {"center": v(325, 1125.83) * mm, "radius": 26.5 * mm});
            skCircle(sketch, "E443", {"center": v(357.5, 1182.12) * mm, "radius": 26.5 * mm});
            skCircle(sketch, "E444", {"center": v(390, 1238.42) * mm, "radius": 26.5 * mm});
            skCircle(sketch, "E445", {"center": v(422.5, 1294.7) * mm, "radius": 26.5 * mm});
            skCircle(sketch, "E446", {"center": v(455, 1351) * mm, "radius": 26.5 * mm});
            skCircle(sketch, "E447", {"center": v(487.5, 1407.3) * mm, "radius": 26.5 * mm});
            skCircle(sketch, "E448", {"center": v(520, 1463.58) * mm, "radius": 26.5 * mm});
            skCircle(sketch, "E449", {"center": v(-162.5, 394.04) * mm, "radius": 26.5 * mm});
            skCircle(sketch, "E450", {"center": v(-130, 450.33) * mm, "radius": 26.5 * mm});
            skCircle(sketch, "E451", {"center": v(-97.5, 506.62) * mm, "radius": 26.5 * mm});
            skCircle(sketch, "E452", {"center": v(-65, 562.92) * mm, "radius": 26.5 * mm});
            skCircle(sketch, "E453", {"center": v(-32.5, 619.2) * mm, "radius": 26.5 * mm});
            skCircle(sketch, "E454", {"center": v(0, 675.5) * mm, "radius": 26.5 * mm});
            skCircle(sketch, "E455", {"center": v(32.5, 731.8) * mm, "radius": 26.5 * mm});
            skCircle(sketch, "E456", {"center": v(65, 788.08) * mm, "radius": 26.5 * mm});
            skCircle(sketch, "E457", {"center": v(97.5, 844.37) * mm, "radius": 26.5 * mm});
            skCircle(sketch, "E458", {"center": v(130, 900.67) * mm, "radius": 26.5 * mm});
            skCircle(sketch, "E459", {"center": v(162.5, 956.96) * mm, "radius": 26.5 * mm});
            skCircle(sketch, "E460", {"center": v(195, 1013.25) * mm, "radius": 26.5 * mm});
            skCircle(sketch, "E461", {"center": v(227.5, 1069.54) * mm, "radius": 26.5 * mm});
            skCircle(sketch, "E462", {"center": v(260, 1125.83) * mm, "radius": 26.5 * mm});
            skCircle(sketch, "E463", {"center": v(292.5, 1182.12) * mm, "radius": 26.5 * mm});
            skCircle(sketch, "E464", {"center": v(325, 1238.42) * mm, "radius": 26.5 * mm});
            skCircle(sketch, "E465", {"center": v(357.5, 1294.7) * mm, "radius": 26.5 * mm});
            skCircle(sketch, "E466", {"center": v(390, 1351) * mm, "radius": 26.5 * mm});
            skCircle(sketch, "E467", {"center": v(422.5, 1407.3) * mm, "radius": 26.5 * mm});
            skCircle(sketch, "E468", {"center": v(455, 1463.58) * mm, "radius": 26.5 * mm});
            skCircle(sketch, "E469", {"center": v(-195, 450.33) * mm, "radius": 26.5 * mm});
            skCircle(sketch, "E470", {"center": v(-162.5, 506.62) * mm, "radius": 26.5 * mm});
            skCircle(sketch, "E471", {"center": v(-130, 562.92) * mm, "radius": 26.5 * mm});
            skCircle(sketch, "E472", {"center": v(-97.5, 619.2) * mm, "radius": 26.5 * mm});
            skCircle(sketch, "E473", {"center": v(-65, 675.5) * mm, "radius": 26.5 * mm});
            skCircle(sketch, "E474", {"center": v(-32.5, 731.8) * mm, "radius": 26.5 * mm});
            skCircle(sketch, "E475", {"center": v(0, 788.08) * mm, "radius": 26.5 * mm});
            skCircle(sketch, "E476", {"center": v(32.5, 844.37) * mm, "radius": 26.5 * mm});
            skCircle(sketch, "E477", {"center": v(65, 900.67) * mm, "radius": 26.5 * mm});
            skCircle(sketch, "E478", {"center": v(97.5, 956.96) * mm, "radius": 26.5 * mm});
            skCircle(sketch, "E479", {"center": v(130, 1013.25) * mm, "radius": 26.5 * mm});
            skCircle(sketch, "E480", {"center": v(162.5, 1069.54) * mm, "radius": 26.5 * mm});
            skCircle(sketch, "E481", {"center": v(195, 1125.83) * mm, "radius": 26.5 * mm});
            skCircle(sketch, "E482", {"center": v(227.5, 1182.12) * mm, "radius": 26.5 * mm});
            skCircle(sketch, "E483", {"center": v(260, 1238.42) * mm, "radius": 26.5 * mm});
            skCircle(sketch, "E484", {"center": v(292.5, 1294.7) * mm, "radius": 26.5 * mm});
            skCircle(sketch, "E485", {"center": v(325, 1351) * mm, "radius": 26.5 * mm});
            skCircle(sketch, "E486", {"center": v(357.5, 1407.3) * mm, "radius": 26.5 * mm});
            skCircle(sketch, "E487", {"center": v(390, 1463.58) * mm, "radius": 26.5 * mm});
            skCircle(sketch, "E488", {"center": v(422.5, 1519.87) * mm, "radius": 26.5 * mm});
            skCircle(sketch, "E489", {"center": v(-227.5, 506.62) * mm, "radius": 26.5 * mm});
            skCircle(sketch, "E490", {"center": v(-195, 562.92) * mm, "radius": 26.5 * mm});
            skCircle(sketch, "E491", {"center": v(-162.5, 619.2) * mm, "radius": 26.5 * mm});
            skCircle(sketch, "E492", {"center": v(-130, 675.5) * mm, "radius": 26.5 * mm});
            skCircle(sketch, "E493", {"center": v(-97.5, 731.8) * mm, "radius": 26.5 * mm});
            skCircle(sketch, "E494", {"center": v(-65, 788.08) * mm, "radius": 26.5 * mm});
            skCircle(sketch, "E495", {"center": v(-32.5, 844.37) * mm, "radius": 26.5 * mm});
            skCircle(sketch, "E496", {"center": v(0, 900.67) * mm, "radius": 26.5 * mm});
            skCircle(sketch, "E497", {"center": v(32.5, 956.96) * mm, "radius": 26.5 * mm});
            skCircle(sketch, "E498", {"center": v(65, 1013.25) * mm, "radius": 26.5 * mm});
            skCircle(sketch, "E499", {"center": v(97.5, 1069.54) * mm, "radius": 26.5 * mm});
            skCircle(sketch, "E500", {"center": v(130, 1125.83) * mm, "radius": 26.5 * mm});
            skCircle(sketch, "E501", {"center": v(162.5, 1182.12) * mm, "radius": 26.5 * mm});
            skCircle(sketch, "E502", {"center": v(195, 1238.42) * mm, "radius": 26.5 * mm});
            skCircle(sketch, "E503", {"center": v(227.5, 1294.7) * mm, "radius": 26.5 * mm});
            skCircle(sketch, "E504", {"center": v(260, 1351) * mm, "radius": 26.5 * mm});
            skCircle(sketch, "E505", {"center": v(292.5, 1407.3) * mm, "radius": 26.5 * mm});
            skCircle(sketch, "E506", {"center": v(325, 1463.58) * mm, "radius": 26.5 * mm});
            skCircle(sketch, "E507", {"center": v(357.5, 1519.87) * mm, "radius": 26.5 * mm});
            skCircle(sketch, "E508", {"center": v(-260, 562.92) * mm, "radius": 26.5 * mm});
            skCircle(sketch, "E509", {"center": v(-227.5, 619.2) * mm, "radius": 26.5 * mm});
            skCircle(sketch, "E510", {"center": v(-195, 675.5) * mm, "radius": 26.5 * mm});
            skCircle(sketch, "E511", {"center": v(-162.5, 731.8) * mm, "radius": 26.5 * mm});
            skCircle(sketch, "E512", {"center": v(-130, 788.08) * mm, "radius": 26.5 * mm});
            skCircle(sketch, "E513", {"center": v(-97.5, 844.37) * mm, "radius": 26.5 * mm});
            skCircle(sketch, "E514", {"center": v(-65, 900.67) * mm, "radius": 26.5 * mm});
            skCircle(sketch, "E515", {"center": v(-32.5, 956.96) * mm, "radius": 26.5 * mm});
            skCircle(sketch, "E516", {"center": v(0, 1013.25) * mm, "radius": 26.5 * mm});
            skCircle(sketch, "E517", {"center": v(97.5, 1182.12) * mm, "radius": 26.5 * mm});
            skCircle(sketch, "E518", {"center": v(130, 1238.42) * mm, "radius": 26.5 * mm});
            skCircle(sketch, "E519", {"center": v(162.5, 1294.7) * mm, "radius": 26.5 * mm});
            skCircle(sketch, "E520", {"center": v(195, 1351) * mm, "radius": 26.5 * mm});
            skCircle(sketch, "E521", {"center": v(227.5, 1407.3) * mm, "radius": 26.5 * mm});
            skCircle(sketch, "E522", {"center": v(260, 1463.58) * mm, "radius": 26.5 * mm});
            skCircle(sketch, "E523", {"center": v(292.5, 1519.87) * mm, "radius": 26.5 * mm});
            skCircle(sketch, "E524", {"center": v(-292.5, 619.2) * mm, "radius": 26.5 * mm});
            skCircle(sketch, "E525", {"center": v(-260, 675.5) * mm, "radius": 26.5 * mm});
            skCircle(sketch, "E526", {"center": v(-227.5, 731.8) * mm, "radius": 26.5 * mm});
            skCircle(sketch, "E527", {"center": v(-195, 788.08) * mm, "radius": 26.5 * mm});
            skCircle(sketch, "E528", {"center": v(-162.5, 844.37) * mm, "radius": 26.5 * mm});
            skCircle(sketch, "E529", {"center": v(-130, 900.67) * mm, "radius": 26.5 * mm});
            skCircle(sketch, "E530", {"center": v(-97.5, 956.96) * mm, "radius": 26.5 * mm});
            skCircle(sketch, "E531", {"center": v(-65, 1013.25) * mm, "radius": 26.5 * mm});
            skCircle(sketch, "E532", {"center": v(65, 1238.42) * mm, "radius": 26.5 * mm});
            skCircle(sketch, "E533", {"center": v(97.5, 1294.7) * mm, "radius": 26.5 * mm});
            skCircle(sketch, "E534", {"center": v(130, 1351) * mm, "radius": 26.5 * mm});
            skCircle(sketch, "E535", {"center": v(162.5, 1407.3) * mm, "radius": 26.5 * mm});
            skCircle(sketch, "E536", {"center": v(195, 1463.58) * mm, "radius": 26.5 * mm});
            skCircle(sketch, "E537", {"center": v(227.5, 1519.87) * mm, "radius": 26.5 * mm});
            skCircle(sketch, "E538", {"center": v(-325, 675.5) * mm, "radius": 26.5 * mm});
            skCircle(sketch, "E539", {"center": v(-292.5, 731.8) * mm, "radius": 26.5 * mm});
            skCircle(sketch, "E540", {"center": v(-260, 788.08) * mm, "radius": 26.5 * mm});
            skCircle(sketch, "E541", {"center": v(-227.5, 844.37) * mm, "radius": 26.5 * mm});
            skCircle(sketch, "E542", {"center": v(-195, 900.67) * mm, "radius": 26.5 * mm});
            skCircle(sketch, "E543", {"center": v(-162.5, 956.96) * mm, "radius": 26.5 * mm});
            skCircle(sketch, "E544", {"center": v(-130, 1013.25) * mm, "radius": 26.5 * mm});
            skCircle(sketch, "E545", {"center": v(-97.5, 1069.54) * mm, "radius": 26.5 * mm});
            skCircle(sketch, "E546", {"center": v(0, 1238.42) * mm, "radius": 26.5 * mm});
            skCircle(sketch, "E547", {"center": v(32.5, 1294.7) * mm, "radius": 26.5 * mm});
            skCircle(sketch, "E548", {"center": v(65, 1351) * mm, "radius": 26.5 * mm});
            skCircle(sketch, "E549", {"center": v(97.5, 1407.3) * mm, "radius": 26.5 * mm});
            skCircle(sketch, "E550", {"center": v(130, 1463.58) * mm, "radius": 26.5 * mm});
            skCircle(sketch, "E551", {"center": v(162.5, 1519.87) * mm, "radius": 26.5 * mm});
            skCircle(sketch, "E552", {"center": v(-357.5, 731.8) * mm, "radius": 26.5 * mm});
            skCircle(sketch, "E553", {"center": v(-325, 788.08) * mm, "radius": 26.5 * mm});
            skCircle(sketch, "E554", {"center": v(-292.5, 844.37) * mm, "radius": 26.5 * mm});
            skCircle(sketch, "E555", {"center": v(-260, 900.67) * mm, "radius": 26.5 * mm});
            skCircle(sketch, "E556", {"center": v(-227.5, 956.96) * mm, "radius": 26.5 * mm});
            skCircle(sketch, "E557", {"center": v(-195, 1013.25) * mm, "radius": 26.5 * mm});
            skCircle(sketch, "E558", {"center": v(-162.5, 1069.54) * mm, "radius": 26.5 * mm});
            skCircle(sketch, "E559", {"center": v(-130, 1125.83) * mm, "radius": 26.5 * mm});
            skCircle(sketch, "E560", {"center": v(-97.5, 1182.12) * mm, "radius": 26.5 * mm});
            skCircle(sketch, "E561", {"center": v(-65, 1238.42) * mm, "radius": 26.5 * mm});
            skCircle(sketch, "E562", {"center": v(-32.5, 1294.7) * mm, "radius": 26.5 * mm});
            skCircle(sketch, "E563", {"center": v(0, 1351) * mm, "radius": 26.5 * mm});
            skCircle(sketch, "E564", {"center": v(32.5, 1407.3) * mm, "radius": 26.5 * mm});
            skCircle(sketch, "E565", {"center": v(65, 1463.58) * mm, "radius": 26.5 * mm});
            skCircle(sketch, "E566", {"center": v(97.5, 1519.87) * mm, "radius": 26.5 * mm});
            skCircle(sketch, "E567", {"center": v(-390, 788.08) * mm, "radius": 26.5 * mm});
            skCircle(sketch, "E568", {"center": v(-357.5, 844.37) * mm, "radius": 26.5 * mm});
            skCircle(sketch, "E569", {"center": v(-325, 900.67) * mm, "radius": 26.5 * mm});
            skCircle(sketch, "E570", {"center": v(-292.5, 956.96) * mm, "radius": 26.5 * mm});
            skCircle(sketch, "E571", {"center": v(-260, 1013.25) * mm, "radius": 26.5 * mm});
            skCircle(sketch, "E572", {"center": v(-227.5, 1069.54) * mm, "radius": 26.5 * mm});
            skCircle(sketch, "E573", {"center": v(-195, 1125.83) * mm, "radius": 26.5 * mm});
            skCircle(sketch, "E574", {"center": v(-162.5, 1182.12) * mm, "radius": 26.5 * mm});
            skCircle(sketch, "E575", {"center": v(-130, 1238.42) * mm, "radius": 26.5 * mm});
            skCircle(sketch, "E576", {"center": v(-97.5, 1294.7) * mm, "radius": 26.5 * mm});
            skCircle(sketch, "E577", {"center": v(-65, 1351) * mm, "radius": 26.5 * mm});
            skCircle(sketch, "E578", {"center": v(-32.5, 1407.3) * mm, "radius": 26.5 * mm});
            skCircle(sketch, "E579", {"center": v(0, 1463.58) * mm, "radius": 26.5 * mm});
            skCircle(sketch, "E580", {"center": v(32.5, 1519.87) * mm, "radius": 26.5 * mm});
            skCircle(sketch, "E581", {"center": v(65, 1576.17) * mm, "radius": 26.5 * mm});
            skCircle(sketch, "E582", {"center": v(-422.5, 844.37) * mm, "radius": 26.5 * mm});
            skCircle(sketch, "E583", {"center": v(-390, 900.67) * mm, "radius": 26.5 * mm});
            skCircle(sketch, "E584", {"center": v(-357.5, 956.96) * mm, "radius": 26.5 * mm});
            skCircle(sketch, "E585", {"center": v(-325, 1013.25) * mm, "radius": 26.5 * mm});
            skCircle(sketch, "E586", {"center": v(-292.5, 1069.54) * mm, "radius": 26.5 * mm});
            skCircle(sketch, "E587", {"center": v(-260, 1125.83) * mm, "radius": 26.5 * mm});
            skCircle(sketch, "E588", {"center": v(-227.5, 1182.12) * mm, "radius": 26.5 * mm});
            skCircle(sketch, "E589", {"center": v(-195, 1238.42) * mm, "radius": 26.5 * mm});
            skCircle(sketch, "E590", {"center": v(-162.5, 1294.7) * mm, "radius": 26.5 * mm});
            skCircle(sketch, "E591", {"center": v(-130, 1351) * mm, "radius": 26.5 * mm});
            skCircle(sketch, "E592", {"center": v(-97.5, 1407.3) * mm, "radius": 26.5 * mm});
            skCircle(sketch, "E593", {"center": v(-65, 1463.58) * mm, "radius": 26.5 * mm});
            skCircle(sketch, "E594", {"center": v(-32.5, 1519.87) * mm, "radius": 26.5 * mm});
            skCircle(sketch, "E595", {"center": v(0, 1576.17) * mm, "radius": 26.5 * mm});
            skCircle(sketch, "E596", {"center": v(-455, 900.67) * mm, "radius": 26.5 * mm});
            skCircle(sketch, "E597", {"center": v(-422.5, 956.96) * mm, "radius": 26.5 * mm});
            skCircle(sketch, "E598", {"center": v(-390, 1013.25) * mm, "radius": 26.5 * mm});
            skCircle(sketch, "E599", {"center": v(-357.5, 1069.54) * mm, "radius": 26.5 * mm});
            skCircle(sketch, "E600", {"center": v(-325, 1125.83) * mm, "radius": 26.5 * mm});
            skCircle(sketch, "E601", {"center": v(-292.5, 1182.12) * mm, "radius": 26.5 * mm});
            skCircle(sketch, "E602", {"center": v(-260, 1238.42) * mm, "radius": 26.5 * mm});
            skCircle(sketch, "E603", {"center": v(-227.5, 1294.7) * mm, "radius": 26.5 * mm});
            skCircle(sketch, "E604", {"center": v(-195, 1351) * mm, "radius": 26.5 * mm});
            skCircle(sketch, "E605", {"center": v(-162.5, 1407.3) * mm, "radius": 26.5 * mm});
            skCircle(sketch, "E606", {"center": v(-130, 1463.58) * mm, "radius": 26.5 * mm});
            skCircle(sketch, "E607", {"center": v(-97.5, 1519.87) * mm, "radius": 26.5 * mm});
            skCircle(sketch, "E608", {"center": v(-65, 1576.17) * mm, "radius": 26.5 * mm});
            skCircle(sketch, "E609", {"center": v(-487.5, 956.96) * mm, "radius": 26.5 * mm});
            skCircle(sketch, "E610", {"center": v(-455, 1013.25) * mm, "radius": 26.5 * mm});
            skCircle(sketch, "E611", {"center": v(-422.5, 1069.54) * mm, "radius": 26.5 * mm});
            skCircle(sketch, "E612", {"center": v(-390, 1125.83) * mm, "radius": 26.5 * mm});
            skCircle(sketch, "E613", {"center": v(-357.5, 1182.12) * mm, "radius": 26.5 * mm});
            skCircle(sketch, "E614", {"center": v(-325, 1238.42) * mm, "radius": 26.5 * mm});
            skCircle(sketch, "E615", {"center": v(-292.5, 1294.7) * mm, "radius": 26.5 * mm});
            skCircle(sketch, "E616", {"center": v(-260, 1351) * mm, "radius": 26.5 * mm});
            skCircle(sketch, "E617", {"center": v(-227.5, 1407.3) * mm, "radius": 26.5 * mm});
            skCircle(sketch, "E618", {"center": v(-195, 1463.58) * mm, "radius": 26.5 * mm});
            skCircle(sketch, "E619", {"center": v(-162.5, 1519.87) * mm, "radius": 26.5 * mm});
            skCircle(sketch, "E620", {"center": v(-520, 1013.25) * mm, "radius": 26.5 * mm});
            skCircle(sketch, "E621", {"center": v(-487.5, 1069.54) * mm, "radius": 26.5 * mm});
            skCircle(sketch, "E622", {"center": v(-455, 1125.83) * mm, "radius": 26.5 * mm});
            skCircle(sketch, "E623", {"center": v(-422.5, 1182.12) * mm, "radius": 26.5 * mm});
            skCircle(sketch, "E624", {"center": v(-390, 1238.42) * mm, "radius": 26.5 * mm});
            skCircle(sketch, "E625", {"center": v(-357.5, 1294.7) * mm, "radius": 26.5 * mm});
            skCircle(sketch, "E626", {"center": v(-325, 1351) * mm, "radius": 26.5 * mm});
            skCircle(sketch, "E627", {"center": v(-292.5, 1407.3) * mm, "radius": 26.5 * mm});
            skCircle(sketch, "E628", {"center": v(-260, 1463.58) * mm, "radius": 26.5 * mm});
            skCircle(sketch, "E629", {"center": v(-227.5, 1519.87) * mm, "radius": 26.5 * mm});
            skCircle(sketch, "E630", {"center": v(-552.5, 1069.54) * mm, "radius": 26.5 * mm});
            skCircle(sketch, "E631", {"center": v(-520, 1125.83) * mm, "radius": 26.5 * mm});
            skCircle(sketch, "E632", {"center": v(-487.5, 1182.12) * mm, "radius": 26.5 * mm});
            skCircle(sketch, "E633", {"center": v(-455, 1238.42) * mm, "radius": 26.5 * mm});
            skCircle(sketch, "E634", {"center": v(-422.5, 1294.7) * mm, "radius": 26.5 * mm});
            skCircle(sketch, "E635", {"center": v(-390, 1351) * mm, "radius": 26.5 * mm});
            skCircle(sketch, "E636", {"center": v(-357.5, 1407.3) * mm, "radius": 26.5 * mm});
            skCircle(sketch, "E637", {"center": v(-325, 1463.58) * mm, "radius": 26.5 * mm});
            skCircle(sketch, "E638", {"center": v(-292.5, 1519.87) * mm, "radius": 26.5 * mm});
            skCircle(sketch, "E639", {"center": v(-585, 1125.83) * mm, "radius": 26.5 * mm});
            skCircle(sketch, "E640", {"center": v(-552.5, 1182.12) * mm, "radius": 26.5 * mm});
            skCircle(sketch, "E641", {"center": v(-520, 1238.42) * mm, "radius": 26.5 * mm});
            skCircle(sketch, "E642", {"center": v(-487.5, 1294.7) * mm, "radius": 26.5 * mm});
            skCircle(sketch, "E643", {"center": v(-455, 1351) * mm, "radius": 26.5 * mm});
            skCircle(sketch, "E644", {"center": v(-422.5, 1407.3) * mm, "radius": 26.5 * mm});
            skCircle(sketch, "E645", {"center": v(-390, 1463.58) * mm, "radius": 26.5 * mm});
            skCircle(sketch, "E646", {"center": v(-357.5, 1519.87) * mm, "radius": 26.5 * mm});
            skCircle(sketch, "E647", {"center": v(-617.5, 1182.12) * mm, "radius": 26.5 * mm});
            skCircle(sketch, "E648", {"center": v(-585, 1238.42) * mm, "radius": 26.5 * mm});
            skCircle(sketch, "E649", {"center": v(-552.5, 1294.7) * mm, "radius": 26.5 * mm});
            skCircle(sketch, "E650", {"center": v(-520, 1351) * mm, "radius": 26.5 * mm});
            skCircle(sketch, "E651", {"center": v(-487.5, 1407.3) * mm, "radius": 26.5 * mm});
            skCircle(sketch, "E652", {"center": v(-455, 1463.58) * mm, "radius": 26.5 * mm});
            skCircle(sketch, "E653", {"center": v(-422.5, 1519.87) * mm, "radius": 26.5 * mm});
            skCircle(sketch, "E654", {"center": v(-650, 1238.42) * mm, "radius": 26.5 * mm});
            skCircle(sketch, "E655", {"center": v(-617.5, 1294.7) * mm, "radius": 26.5 * mm});
            skCircle(sketch, "E656", {"center": v(-585, 1351) * mm, "radius": 26.5 * mm});
            skCircle(sketch, "E657", {"center": v(-552.5, 1407.3) * mm, "radius": 26.5 * mm});
            skCircle(sketch, "E658", {"center": v(-520, 1463.58) * mm, "radius": 26.5 * mm});
            skCircle(sketch, "E659", {"center": v(-682.5, 1294.7) * mm, "radius": 26.5 * mm});
            skCircle(sketch, "E660", {"center": v(-650, 1351) * mm, "radius": 26.5 * mm});
            skCircle(sketch, "E661", {"center": v(-617.5, 1407.3) * mm, "radius": 26.5 * mm});
            skCircle(sketch, "E662", {"center": v(-585, 1463.58) * mm, "radius": 26.5 * mm});
            skCircle(sketch, "E663", {"center": v(-715, 1351) * mm, "radius": 26.5 * mm});
            skCircle(sketch, "E664", {"center": v(-682.5, 1407.3) * mm, "radius": 26.5 * mm});
            skCircle(sketch, "E665", {"center": v(0, 1125.83) * mm, "radius": 58 * mm});
            skCircle(sketch, "E666", {"center": v(-195, 337.75) * mm, "radius": 26.5 * mm});
            skCircle(sketch, "E667", {"center": v(-227.5, 394.04) * mm, "radius": 26.5 * mm});
            skCircle(sketch, "E668", {"center": v(-260, 450.33) * mm, "radius": 26.5 * mm});
            skCircle(sketch, "E669", {"center": v(-292.5, 506.62) * mm, "radius": 26.5 * mm});
            skCircle(sketch, "E670", {"center": v(-325, 562.92) * mm, "radius": 26.5 * mm});
            skCircle(sketch, "E671", {"center": v(-357.5, 619.2) * mm, "radius": 26.5 * mm});
            skCircle(sketch, "E672", {"center": v(-390, 675.5) * mm, "radius": 26.5 * mm});
            skCircle(sketch, "E673", {"center": v(-422.5, 731.8) * mm, "radius": 26.5 * mm});
            skCircle(sketch, "E674", {"center": v(-455, 788.08) * mm, "radius": 26.5 * mm});
            skCircle(sketch, "E675", {"center": v(-487.5, 844.37) * mm, "radius": 26.5 * mm});
            skCircle(sketch, "E676", {"center": v(-520, 900.67) * mm, "radius": 26.5 * mm});
            skCircle(sketch, "E677", {"center": v(-552.5, 956.96) * mm, "radius": 26.5 * mm});
            skCircle(sketch, "E678", {"center": v(-585, 1013.25) * mm, "radius": 26.5 * mm});
            skCircle(sketch, "E679", {"center": v(-617.5, 1069.54) * mm, "radius": 26.5 * mm});
            skCircle(sketch, "E680", {"center": v(-650, 1125.83) * mm, "radius": 26.5 * mm});
            skCircle(sketch, "E681", {"center": v(-682.5, 1182.12) * mm, "radius": 26.5 * mm});
            skCircle(sketch, "E682", {"center": v(-715, 1238.42) * mm, "radius": 26.5 * mm});
            skCircle(sketch, "E683", {"center": v(-747.5, 1294.7) * mm, "radius": 26.5 * mm});
            skCircle(sketch, "E684", {"center": v(-780, 1351) * mm, "radius": 26.5 * mm});
            skCircle(sketch, "E685", {"center": v(-260, 337.75) * mm, "radius": 26.5 * mm});
            skCircle(sketch, "E686", {"center": v(-292.5, 394.04) * mm, "radius": 26.5 * mm});
            skCircle(sketch, "E687", {"center": v(-325, 450.33) * mm, "radius": 26.5 * mm});
            skCircle(sketch, "E688", {"center": v(-357.5, 506.62) * mm, "radius": 26.5 * mm});
            skCircle(sketch, "E689", {"center": v(-390, 562.92) * mm, "radius": 26.5 * mm});
            skCircle(sketch, "E690", {"center": v(-422.5, 619.2) * mm, "radius": 26.5 * mm});
            skCircle(sketch, "E691", {"center": v(-455, 675.5) * mm, "radius": 26.5 * mm});
            skCircle(sketch, "E692", {"center": v(-487.5, 731.8) * mm, "radius": 26.5 * mm});
            skCircle(sketch, "E693", {"center": v(-520, 788.08) * mm, "radius": 26.5 * mm});
            skCircle(sketch, "E694", {"center": v(-552.5, 844.37) * mm, "radius": 26.5 * mm});
            skCircle(sketch, "E695", {"center": v(-585, 900.67) * mm, "radius": 26.5 * mm});
            skCircle(sketch, "E696", {"center": v(-617.5, 956.96) * mm, "radius": 26.5 * mm});
            skCircle(sketch, "E697", {"center": v(-650, 1013.25) * mm, "radius": 26.5 * mm});
            skCircle(sketch, "E698", {"center": v(-682.5, 1069.54) * mm, "radius": 26.5 * mm});
            skCircle(sketch, "E699", {"center": v(-715, 1125.83) * mm, "radius": 26.5 * mm});
            skCircle(sketch, "E700", {"center": v(-747.5, 1182.12) * mm, "radius": 26.5 * mm});
            skCircle(sketch, "E701", {"center": v(-780, 1238.42) * mm, "radius": 26.5 * mm});
            skCircle(sketch, "E702", {"center": v(-812.5, 1294.7) * mm, "radius": 26.5 * mm});
            skCircle(sketch, "E703", {"center": v(-292.5, 281.46) * mm, "radius": 26.5 * mm});
            skCircle(sketch, "E704", {"center": v(-325, 337.75) * mm, "radius": 26.5 * mm});
            skCircle(sketch, "E705", {"center": v(-357.5, 394.04) * mm, "radius": 26.5 * mm});
            skCircle(sketch, "E706", {"center": v(-390, 450.33) * mm, "radius": 26.5 * mm});
            skCircle(sketch, "E707", {"center": v(-422.5, 506.62) * mm, "radius": 26.5 * mm});
            skCircle(sketch, "E708", {"center": v(-455, 562.92) * mm, "radius": 26.5 * mm});
            skCircle(sketch, "E709", {"center": v(-487.5, 619.2) * mm, "radius": 26.5 * mm});
            skCircle(sketch, "E710", {"center": v(-520, 675.5) * mm, "radius": 26.5 * mm});
            skCircle(sketch, "E711", {"center": v(-552.5, 731.8) * mm, "radius": 26.5 * mm});
            skCircle(sketch, "E712", {"center": v(-585, 788.08) * mm, "radius": 26.5 * mm});
            skCircle(sketch, "E713", {"center": v(-617.5, 844.37) * mm, "radius": 26.5 * mm});
            skCircle(sketch, "E714", {"center": v(-650, 900.67) * mm, "radius": 26.5 * mm});
            skCircle(sketch, "E715", {"center": v(-682.5, 956.96) * mm, "radius": 26.5 * mm});
            skCircle(sketch, "E716", {"center": v(-715, 1013.25) * mm, "radius": 26.5 * mm});
            skCircle(sketch, "E717", {"center": v(-747.5, 1069.54) * mm, "radius": 26.5 * mm});
            skCircle(sketch, "E718", {"center": v(-780, 1125.83) * mm, "radius": 26.5 * mm});
            skCircle(sketch, "E719", {"center": v(-812.5, 1182.12) * mm, "radius": 26.5 * mm});
            skCircle(sketch, "E720", {"center": v(-845, 1238.42) * mm, "radius": 26.5 * mm});
            skCircle(sketch, "E721", {"center": v(-877.5, 1294.7) * mm, "radius": 26.5 * mm});
            skCircle(sketch, "E722", {"center": v(-325, 225.17) * mm, "radius": 26.5 * mm});
            skCircle(sketch, "E723", {"center": v(-357.5, 281.46) * mm, "radius": 26.5 * mm});
            skCircle(sketch, "E724", {"center": v(-390, 337.75) * mm, "radius": 26.5 * mm});
            skCircle(sketch, "E725", {"center": v(-422.5, 394.04) * mm, "radius": 26.5 * mm});
            skCircle(sketch, "E726", {"center": v(-455, 450.33) * mm, "radius": 26.5 * mm});
            skCircle(sketch, "E727", {"center": v(-487.5, 506.62) * mm, "radius": 26.5 * mm});
            skCircle(sketch, "E728", {"center": v(-520, 562.92) * mm, "radius": 26.5 * mm});
            skCircle(sketch, "E729", {"center": v(-552.5, 619.2) * mm, "radius": 26.5 * mm});
            skCircle(sketch, "E730", {"center": v(-585, 675.5) * mm, "radius": 26.5 * mm});
            skCircle(sketch, "E731", {"center": v(-617.5, 731.8) * mm, "radius": 26.5 * mm});
            skCircle(sketch, "E732", {"center": v(-650, 788.08) * mm, "radius": 26.5 * mm});
            skCircle(sketch, "E733", {"center": v(-682.5, 844.37) * mm, "radius": 26.5 * mm});
            skCircle(sketch, "E734", {"center": v(-715, 900.67) * mm, "radius": 26.5 * mm});
            skCircle(sketch, "E735", {"center": v(-747.5, 956.96) * mm, "radius": 26.5 * mm});
            skCircle(sketch, "E736", {"center": v(-780, 1013.25) * mm, "radius": 26.5 * mm});
            skCircle(sketch, "E737", {"center": v(-812.5, 1069.54) * mm, "radius": 26.5 * mm});
            skCircle(sketch, "E738", {"center": v(-845, 1125.83) * mm, "radius": 26.5 * mm});
            skCircle(sketch, "E739", {"center": v(-877.5, 1182.12) * mm, "radius": 26.5 * mm});
            skCircle(sketch, "E740", {"center": v(-910, 1238.42) * mm, "radius": 26.5 * mm});
            skCircle(sketch, "E741", {"center": v(-357.5, 168.87) * mm, "radius": 26.5 * mm});
            skCircle(sketch, "E742", {"center": v(-390, 225.17) * mm, "radius": 26.5 * mm});
            skCircle(sketch, "E743", {"center": v(-422.5, 281.46) * mm, "radius": 26.5 * mm});
            skCircle(sketch, "E744", {"center": v(-455, 337.75) * mm, "radius": 26.5 * mm});
            skCircle(sketch, "E745", {"center": v(-487.5, 394.04) * mm, "radius": 26.5 * mm});
            skCircle(sketch, "E746", {"center": v(-520, 450.33) * mm, "radius": 26.5 * mm});
            skCircle(sketch, "E747", {"center": v(-552.5, 506.62) * mm, "radius": 26.5 * mm});
            skCircle(sketch, "E748", {"center": v(-585, 562.92) * mm, "radius": 26.5 * mm});
            skCircle(sketch, "E749", {"center": v(-617.5, 619.2) * mm, "radius": 26.5 * mm});
            skCircle(sketch, "E750", {"center": v(-650, 675.5) * mm, "radius": 26.5 * mm});
            skCircle(sketch, "E751", {"center": v(-682.5, 731.8) * mm, "radius": 26.5 * mm});
            skCircle(sketch, "E752", {"center": v(-715, 788.08) * mm, "radius": 26.5 * mm});
            skCircle(sketch, "E753", {"center": v(-747.5, 844.37) * mm, "radius": 26.5 * mm});
            skCircle(sketch, "E754", {"center": v(-780, 900.67) * mm, "radius": 26.5 * mm});
            skCircle(sketch, "E755", {"center": v(-812.5, 956.96) * mm, "radius": 26.5 * mm});
            skCircle(sketch, "E756", {"center": v(-845, 1013.25) * mm, "radius": 26.5 * mm});
            skCircle(sketch, "E757", {"center": v(-877.5, 1069.54) * mm, "radius": 26.5 * mm});
            skCircle(sketch, "E758", {"center": v(-910, 1125.83) * mm, "radius": 26.5 * mm});
            skCircle(sketch, "E759", {"center": v(-942.5, 1182.12) * mm, "radius": 26.5 * mm});
            skCircle(sketch, "E760", {"center": v(-975, 1238.42) * mm, "radius": 26.5 * mm});
            skCircle(sketch, "E761", {"center": v(-390, 112.58) * mm, "radius": 26.5 * mm});
            skCircle(sketch, "E762", {"center": v(-422.5, 168.87) * mm, "radius": 26.5 * mm});
            skCircle(sketch, "E763", {"center": v(-455, 225.17) * mm, "radius": 26.5 * mm});
            skCircle(sketch, "E764", {"center": v(-487.5, 281.46) * mm, "radius": 26.5 * mm});
            skCircle(sketch, "E765", {"center": v(-520, 337.75) * mm, "radius": 26.5 * mm});
            skCircle(sketch, "E766", {"center": v(-552.5, 394.04) * mm, "radius": 26.5 * mm});
            skCircle(sketch, "E767", {"center": v(-585, 450.33) * mm, "radius": 26.5 * mm});
            skCircle(sketch, "E768", {"center": v(-617.5, 506.62) * mm, "radius": 26.5 * mm});
            skCircle(sketch, "E769", {"center": v(-650, 562.92) * mm, "radius": 26.5 * mm});
            skCircle(sketch, "E770", {"center": v(-682.5, 619.2) * mm, "radius": 26.5 * mm});
            skCircle(sketch, "E771", {"center": v(-715, 675.5) * mm, "radius": 26.5 * mm});
            skCircle(sketch, "E772", {"center": v(-747.5, 731.8) * mm, "radius": 26.5 * mm});
            skCircle(sketch, "E773", {"center": v(-780, 788.08) * mm, "radius": 26.5 * mm});
            skCircle(sketch, "E774", {"center": v(-812.5, 844.37) * mm, "radius": 26.5 * mm});
            skCircle(sketch, "E775", {"center": v(-845, 900.67) * mm, "radius": 26.5 * mm});
            skCircle(sketch, "E776", {"center": v(-877.5, 956.96) * mm, "radius": 26.5 * mm});
            skCircle(sketch, "E777", {"center": v(-910, 1013.25) * mm, "radius": 26.5 * mm});
            skCircle(sketch, "E778", {"center": v(-942.5, 1069.54) * mm, "radius": 26.5 * mm});
            skCircle(sketch, "E779", {"center": v(-975, 1125.83) * mm, "radius": 26.5 * mm});
            skCircle(sketch, "E780", {"center": v(-1007.5, 1182.12) * mm, "radius": 26.5 * mm});
            skCircle(sketch, "E781", {"center": v(-422.5, 56.3) * mm, "radius": 26.5 * mm});
            skCircle(sketch, "E782", {"center": v(-455, 112.58) * mm, "radius": 26.5 * mm});
            skCircle(sketch, "E783", {"center": v(-487.5, 168.87) * mm, "radius": 26.5 * mm});
            skCircle(sketch, "E784", {"center": v(-520, 225.17) * mm, "radius": 26.5 * mm});
            skCircle(sketch, "E785", {"center": v(-552.5, 281.46) * mm, "radius": 26.5 * mm});
            skCircle(sketch, "E786", {"center": v(-585, 337.75) * mm, "radius": 26.5 * mm});
            skCircle(sketch, "E787", {"center": v(-617.5, 394.04) * mm, "radius": 26.5 * mm});
            skCircle(sketch, "E788", {"center": v(-650, 450.33) * mm, "radius": 26.5 * mm});
            skCircle(sketch, "E789", {"center": v(-682.5, 506.62) * mm, "radius": 26.5 * mm});
            skCircle(sketch, "E790", {"center": v(-715, 562.92) * mm, "radius": 26.5 * mm});
            skCircle(sketch, "E791", {"center": v(-747.5, 619.2) * mm, "radius": 26.5 * mm});
            skCircle(sketch, "E792", {"center": v(-780, 675.5) * mm, "radius": 26.5 * mm});
            skCircle(sketch, "E793", {"center": v(-812.5, 731.8) * mm, "radius": 26.5 * mm});
            skCircle(sketch, "E794", {"center": v(-845, 788.08) * mm, "radius": 26.5 * mm});
            skCircle(sketch, "E795", {"center": v(-877.5, 844.37) * mm, "radius": 26.5 * mm});
            skCircle(sketch, "E796", {"center": v(-910, 900.67) * mm, "radius": 26.5 * mm});
            skCircle(sketch, "E797", {"center": v(-942.5, 956.96) * mm, "radius": 26.5 * mm});
            skCircle(sketch, "E798", {"center": v(-975, 1013.25) * mm, "radius": 26.5 * mm});
            skCircle(sketch, "E799", {"center": v(-1007.5, 1069.54) * mm, "radius": 26.5 * mm});
            skCircle(sketch, "E800", {"center": v(-1040, 1125.83) * mm, "radius": 26.5 * mm});
            skCircle(sketch, "E801", {"center": v(-487.5, 56.3) * mm, "radius": 26.5 * mm});
            skCircle(sketch, "E802", {"center": v(-520, 112.58) * mm, "radius": 26.5 * mm});
            skCircle(sketch, "E803", {"center": v(-552.5, 168.87) * mm, "radius": 26.5 * mm});
            skCircle(sketch, "E804", {"center": v(-585, 225.17) * mm, "radius": 26.5 * mm});
            skCircle(sketch, "E805", {"center": v(-617.5, 281.46) * mm, "radius": 26.5 * mm});
            skCircle(sketch, "E806", {"center": v(-650, 337.75) * mm, "radius": 26.5 * mm});
            skCircle(sketch, "E807", {"center": v(-682.5, 394.04) * mm, "radius": 26.5 * mm});
            skCircle(sketch, "E808", {"center": v(-715, 450.33) * mm, "radius": 26.5 * mm});
            skCircle(sketch, "E809", {"center": v(-747.5, 506.62) * mm, "radius": 26.5 * mm});
            skCircle(sketch, "E810", {"center": v(-780, 562.92) * mm, "radius": 26.5 * mm});
            skCircle(sketch, "E811", {"center": v(-812.5, 619.2) * mm, "radius": 26.5 * mm});
            skCircle(sketch, "E812", {"center": v(-845, 675.5) * mm, "radius": 26.5 * mm});
            skCircle(sketch, "E813", {"center": v(-877.5, 731.8) * mm, "radius": 26.5 * mm});
            skCircle(sketch, "E814", {"center": v(-910, 788.08) * mm, "radius": 26.5 * mm});
            skCircle(sketch, "E815", {"center": v(-942.5, 844.37) * mm, "radius": 26.5 * mm});
            skCircle(sketch, "E816", {"center": v(-975, 900.67) * mm, "radius": 26.5 * mm});
            skCircle(sketch, "E817", {"center": v(-1007.5, 956.96) * mm, "radius": 26.5 * mm});
            skCircle(sketch, "E818", {"center": v(-1040, 1013.25) * mm, "radius": 26.5 * mm});
            skCircle(sketch, "E819", {"center": v(-1072.5, 1069.54) * mm, "radius": 26.5 * mm});
            skCircle(sketch, "E820", {"center": v(-1105, 1125.83) * mm, "radius": 26.5 * mm});
            skCircle(sketch, "E821", {"center": v(-552.5, 56.3) * mm, "radius": 26.5 * mm});
            skCircle(sketch, "E822", {"center": v(-585, 112.58) * mm, "radius": 26.5 * mm});
            skCircle(sketch, "E823", {"center": v(-617.5, 168.87) * mm, "radius": 26.5 * mm});
            skCircle(sketch, "E824", {"center": v(-650, 225.17) * mm, "radius": 26.5 * mm});
            skCircle(sketch, "E825", {"center": v(-682.5, 281.46) * mm, "radius": 26.5 * mm});
            skCircle(sketch, "E826", {"center": v(-715, 337.75) * mm, "radius": 26.5 * mm});
            skCircle(sketch, "E827", {"center": v(-747.5, 394.04) * mm, "radius": 26.5 * mm});
            skCircle(sketch, "E828", {"center": v(-780, 450.33) * mm, "radius": 26.5 * mm});
            skCircle(sketch, "E829", {"center": v(-812.5, 506.62) * mm, "radius": 26.5 * mm});
            skCircle(sketch, "E830", {"center": v(-845, 562.92) * mm, "radius": 26.5 * mm});
            skCircle(sketch, "E831", {"center": v(-877.5, 619.2) * mm, "radius": 26.5 * mm});
            skCircle(sketch, "E832", {"center": v(-910, 675.5) * mm, "radius": 26.5 * mm});
            skCircle(sketch, "E833", {"center": v(-942.5, 731.8) * mm, "radius": 26.5 * mm});
            skCircle(sketch, "E834", {"center": v(-975, 788.08) * mm, "radius": 26.5 * mm});
            skCircle(sketch, "E835", {"center": v(-1007.5, 844.37) * mm, "radius": 26.5 * mm});
            skCircle(sketch, "E836", {"center": v(-1040, 900.67) * mm, "radius": 26.5 * mm});
            skCircle(sketch, "E837", {"center": v(-1072.5, 956.96) * mm, "radius": 26.5 * mm});
            skCircle(sketch, "E838", {"center": v(-1105, 1013.25) * mm, "radius": 26.5 * mm});
            skCircle(sketch, "E839", {"center": v(-1137.5, 1069.54) * mm, "radius": 26.5 * mm});
            skCircle(sketch, "E840", {"center": v(-617.5, 56.3) * mm, "radius": 26.5 * mm});
            skCircle(sketch, "E841", {"center": v(-650, 112.58) * mm, "radius": 26.5 * mm});
            skCircle(sketch, "E842", {"center": v(-682.5, 168.87) * mm, "radius": 26.5 * mm});
            skCircle(sketch, "E843", {"center": v(-715, 225.17) * mm, "radius": 26.5 * mm});
            skCircle(sketch, "E844", {"center": v(-747.5, 281.46) * mm, "radius": 26.5 * mm});
            skCircle(sketch, "E845", {"center": v(-780, 337.75) * mm, "radius": 26.5 * mm});
            skCircle(sketch, "E846", {"center": v(-812.5, 394.04) * mm, "radius": 26.5 * mm});
            skCircle(sketch, "E847", {"center": v(-845, 450.33) * mm, "radius": 26.5 * mm});
            skCircle(sketch, "E848", {"center": v(-877.5, 506.62) * mm, "radius": 26.5 * mm});
            skCircle(sketch, "E849", {"center": v(-975, 675.5) * mm, "radius": 26.5 * mm});
            skCircle(sketch, "E850", {"center": v(-1007.5, 731.8) * mm, "radius": 26.5 * mm});
            skCircle(sketch, "E851", {"center": v(-1040, 788.08) * mm, "radius": 26.5 * mm});
            skCircle(sketch, "E852", {"center": v(-1072.5, 844.37) * mm, "radius": 26.5 * mm});
            skCircle(sketch, "E853", {"center": v(-1105, 900.67) * mm, "radius": 26.5 * mm});
            skCircle(sketch, "E854", {"center": v(-1137.5, 956.96) * mm, "radius": 26.5 * mm});
            skCircle(sketch, "E855", {"center": v(-1170, 1013.25) * mm, "radius": 26.5 * mm});
            skCircle(sketch, "E856", {"center": v(-682.5, 56.3) * mm, "radius": 26.5 * mm});
            skCircle(sketch, "E857", {"center": v(-715, 112.58) * mm, "radius": 26.5 * mm});
            skCircle(sketch, "E858", {"center": v(-747.5, 168.87) * mm, "radius": 26.5 * mm});
            skCircle(sketch, "E859", {"center": v(-780, 225.17) * mm, "radius": 26.5 * mm});
            skCircle(sketch, "E860", {"center": v(-812.5, 281.46) * mm, "radius": 26.5 * mm});
            skCircle(sketch, "E861", {"center": v(-845, 337.75) * mm, "radius": 26.5 * mm});
            skCircle(sketch, "E862", {"center": v(-877.5, 394.04) * mm, "radius": 26.5 * mm});
            skCircle(sketch, "E863", {"center": v(-910, 450.33) * mm, "radius": 26.5 * mm});
            skCircle(sketch, "E864", {"center": v(-1040, 675.5) * mm, "radius": 26.5 * mm});
            skCircle(sketch, "E865", {"center": v(-1072.5, 731.8) * mm, "radius": 26.5 * mm});
            skCircle(sketch, "E866", {"center": v(-1105, 788.08) * mm, "radius": 26.5 * mm});
            skCircle(sketch, "E867", {"center": v(-1137.5, 844.37) * mm, "radius": 26.5 * mm});
            skCircle(sketch, "E868", {"center": v(-1170, 900.67) * mm, "radius": 26.5 * mm});
            skCircle(sketch, "E869", {"center": v(-1202.5, 956.96) * mm, "radius": 26.5 * mm});
            skCircle(sketch, "E870", {"center": v(-747.5, 56.3) * mm, "radius": 26.5 * mm});
            skCircle(sketch, "E871", {"center": v(-780, 112.58) * mm, "radius": 26.5 * mm});
            skCircle(sketch, "E872", {"center": v(-812.5, 168.87) * mm, "radius": 26.5 * mm});
            skCircle(sketch, "E873", {"center": v(-845, 225.17) * mm, "radius": 26.5 * mm});
            skCircle(sketch, "E874", {"center": v(-877.5, 281.46) * mm, "radius": 26.5 * mm});
            skCircle(sketch, "E875", {"center": v(-910, 337.75) * mm, "radius": 26.5 * mm});
            skCircle(sketch, "E876", {"center": v(-942.5, 394.04) * mm, "radius": 26.5 * mm});
            skCircle(sketch, "E877", {"center": v(-975, 450.33) * mm, "radius": 26.5 * mm});
            skCircle(sketch, "E878", {"center": v(-1072.5, 619.2) * mm, "radius": 26.5 * mm});
            skCircle(sketch, "E879", {"center": v(-1105, 675.5) * mm, "radius": 26.5 * mm});
            skCircle(sketch, "E880", {"center": v(-1137.5, 731.8) * mm, "radius": 26.5 * mm});
            skCircle(sketch, "E881", {"center": v(-1170, 788.08) * mm, "radius": 26.5 * mm});
            skCircle(sketch, "E882", {"center": v(-1202.5, 844.37) * mm, "radius": 26.5 * mm});
            skCircle(sketch, "E883", {"center": v(-1235, 900.67) * mm, "radius": 26.5 * mm});
            skCircle(sketch, "E884", {"center": v(-812.5, 56.3) * mm, "radius": 26.5 * mm});
            skCircle(sketch, "E885", {"center": v(-845, 112.58) * mm, "radius": 26.5 * mm});
            skCircle(sketch, "E886", {"center": v(-877.5, 168.87) * mm, "radius": 26.5 * mm});
            skCircle(sketch, "E887", {"center": v(-910, 225.17) * mm, "radius": 26.5 * mm});
            skCircle(sketch, "E888", {"center": v(-942.5, 281.46) * mm, "radius": 26.5 * mm});
            skCircle(sketch, "E889", {"center": v(-975, 337.75) * mm, "radius": 26.5 * mm});
            skCircle(sketch, "E890", {"center": v(-1007.5, 394.04) * mm, "radius": 26.5 * mm});
            skCircle(sketch, "E891", {"center": v(-1040, 450.33) * mm, "radius": 26.5 * mm});
            skCircle(sketch, "E892", {"center": v(-1072.5, 506.62) * mm, "radius": 26.5 * mm});
            skCircle(sketch, "E893", {"center": v(-1105, 562.92) * mm, "radius": 26.5 * mm});
            skCircle(sketch, "E894", {"center": v(-1137.5, 619.2) * mm, "radius": 26.5 * mm});
            skCircle(sketch, "E895", {"center": v(-1170, 675.5) * mm, "radius": 26.5 * mm});
            skCircle(sketch, "E896", {"center": v(-1202.5, 731.8) * mm, "radius": 26.5 * mm});
            skCircle(sketch, "E897", {"center": v(-1235, 788.08) * mm, "radius": 26.5 * mm});
            skCircle(sketch, "E898", {"center": v(-1267.5, 844.37) * mm, "radius": 26.5 * mm});
            skCircle(sketch, "E899", {"center": v(-877.5, 56.3) * mm, "radius": 26.5 * mm});
            skCircle(sketch, "E900", {"center": v(-910, 112.58) * mm, "radius": 26.5 * mm});
            skCircle(sketch, "E901", {"center": v(-942.5, 168.87) * mm, "radius": 26.5 * mm});
            skCircle(sketch, "E902", {"center": v(-975, 225.17) * mm, "radius": 26.5 * mm});
            skCircle(sketch, "E903", {"center": v(-1007.5, 281.46) * mm, "radius": 26.5 * mm});
            skCircle(sketch, "E904", {"center": v(-1040, 337.75) * mm, "radius": 26.5 * mm});
            skCircle(sketch, "E905", {"center": v(-1072.5, 394.04) * mm, "radius": 26.5 * mm});
            skCircle(sketch, "E906", {"center": v(-1105, 450.33) * mm, "radius": 26.5 * mm});
            skCircle(sketch, "E907", {"center": v(-1137.5, 506.62) * mm, "radius": 26.5 * mm});
            skCircle(sketch, "E908", {"center": v(-1170, 562.92) * mm, "radius": 26.5 * mm});
            skCircle(sketch, "E909", {"center": v(-1202.5, 619.2) * mm, "radius": 26.5 * mm});
            skCircle(sketch, "E910", {"center": v(-1235, 675.5) * mm, "radius": 26.5 * mm});
            skCircle(sketch, "E911", {"center": v(-1267.5, 731.8) * mm, "radius": 26.5 * mm});
            skCircle(sketch, "E912", {"center": v(-1300, 788.08) * mm, "radius": 26.5 * mm});
            skCircle(sketch, "E913", {"center": v(-1332.5, 844.37) * mm, "radius": 26.5 * mm});
            skCircle(sketch, "E914", {"center": v(-942.5, 56.3) * mm, "radius": 26.5 * mm});
            skCircle(sketch, "E915", {"center": v(-975, 112.58) * mm, "radius": 26.5 * mm});
            skCircle(sketch, "E916", {"center": v(-1007.5, 168.87) * mm, "radius": 26.5 * mm});
            skCircle(sketch, "E917", {"center": v(-1040, 225.17) * mm, "radius": 26.5 * mm});
            skCircle(sketch, "E918", {"center": v(-1072.5, 281.46) * mm, "radius": 26.5 * mm});
            skCircle(sketch, "E919", {"center": v(-1105, 337.75) * mm, "radius": 26.5 * mm});
            skCircle(sketch, "E920", {"center": v(-1137.5, 394.04) * mm, "radius": 26.5 * mm});
            skCircle(sketch, "E921", {"center": v(-1170, 450.33) * mm, "radius": 26.5 * mm});
            skCircle(sketch, "E922", {"center": v(-1202.5, 506.62) * mm, "radius": 26.5 * mm});
            skCircle(sketch, "E923", {"center": v(-1235, 562.92) * mm, "radius": 26.5 * mm});
            skCircle(sketch, "E924", {"center": v(-1267.5, 619.2) * mm, "radius": 26.5 * mm});
            skCircle(sketch, "E925", {"center": v(-1300, 675.5) * mm, "radius": 26.5 * mm});
            skCircle(sketch, "E926", {"center": v(-1332.5, 731.8) * mm, "radius": 26.5 * mm});
            skCircle(sketch, "E927", {"center": v(-1365, 788.08) * mm, "radius": 26.5 * mm});
            skCircle(sketch, "E928", {"center": v(-1007.5, 56.3) * mm, "radius": 26.5 * mm});
            skCircle(sketch, "E929", {"center": v(-1040, 112.58) * mm, "radius": 26.5 * mm});
            skCircle(sketch, "E930", {"center": v(-1072.5, 168.87) * mm, "radius": 26.5 * mm});
            skCircle(sketch, "E931", {"center": v(-1105, 225.17) * mm, "radius": 26.5 * mm});
            skCircle(sketch, "E932", {"center": v(-1137.5, 281.46) * mm, "radius": 26.5 * mm});
            skCircle(sketch, "E933", {"center": v(-1170, 337.75) * mm, "radius": 26.5 * mm});
            skCircle(sketch, "E934", {"center": v(-1202.5, 394.04) * mm, "radius": 26.5 * mm});
            skCircle(sketch, "E935", {"center": v(-1235, 450.33) * mm, "radius": 26.5 * mm});
            skCircle(sketch, "E936", {"center": v(-1267.5, 506.62) * mm, "radius": 26.5 * mm});
            skCircle(sketch, "E937", {"center": v(-1300, 562.92) * mm, "radius": 26.5 * mm});
            skCircle(sketch, "E938", {"center": v(-1332.5, 619.2) * mm, "radius": 26.5 * mm});
            skCircle(sketch, "E939", {"center": v(-1365, 675.5) * mm, "radius": 26.5 * mm});
            skCircle(sketch, "E940", {"center": v(-1397.5, 731.8) * mm, "radius": 26.5 * mm});
            skCircle(sketch, "E941", {"center": v(-1072.5, 56.3) * mm, "radius": 26.5 * mm});
            skCircle(sketch, "E942", {"center": v(-1105, 112.58) * mm, "radius": 26.5 * mm});
            skCircle(sketch, "E943", {"center": v(-1137.5, 168.87) * mm, "radius": 26.5 * mm});
            skCircle(sketch, "E944", {"center": v(-1170, 225.17) * mm, "radius": 26.5 * mm});
            skCircle(sketch, "E945", {"center": v(-1202.5, 281.46) * mm, "radius": 26.5 * mm});
            skCircle(sketch, "E946", {"center": v(-1235, 337.75) * mm, "radius": 26.5 * mm});
            skCircle(sketch, "E947", {"center": v(-1267.5, 394.04) * mm, "radius": 26.5 * mm});
            skCircle(sketch, "E948", {"center": v(-1300, 450.33) * mm, "radius": 26.5 * mm});
            skCircle(sketch, "E949", {"center": v(-1332.5, 506.62) * mm, "radius": 26.5 * mm});
            skCircle(sketch, "E950", {"center": v(-1365, 562.92) * mm, "radius": 26.5 * mm});
            skCircle(sketch, "E951", {"center": v(-1397.5, 619.2) * mm, "radius": 26.5 * mm});
            skCircle(sketch, "E952", {"center": v(-1137.5, 56.3) * mm, "radius": 26.5 * mm});
            skCircle(sketch, "E953", {"center": v(-1170, 112.58) * mm, "radius": 26.5 * mm});
            skCircle(sketch, "E954", {"center": v(-1202.5, 168.87) * mm, "radius": 26.5 * mm});
            skCircle(sketch, "E955", {"center": v(-1235, 225.17) * mm, "radius": 26.5 * mm});
            skCircle(sketch, "E956", {"center": v(-1267.5, 281.46) * mm, "radius": 26.5 * mm});
            skCircle(sketch, "E957", {"center": v(-1300, 337.75) * mm, "radius": 26.5 * mm});
            skCircle(sketch, "E958", {"center": v(-1332.5, 394.04) * mm, "radius": 26.5 * mm});
            skCircle(sketch, "E959", {"center": v(-1365, 450.33) * mm, "radius": 26.5 * mm});
            skCircle(sketch, "E960", {"center": v(-1397.5, 506.62) * mm, "radius": 26.5 * mm});
            skCircle(sketch, "E961", {"center": v(-1430, 562.92) * mm, "radius": 26.5 * mm});
            skCircle(sketch, "E962", {"center": v(-1202.5, 56.3) * mm, "radius": 26.5 * mm});
            skCircle(sketch, "E963", {"center": v(-1235, 112.58) * mm, "radius": 26.5 * mm});
            skCircle(sketch, "E964", {"center": v(-1267.5, 168.87) * mm, "radius": 26.5 * mm});
            skCircle(sketch, "E965", {"center": v(-1300, 225.17) * mm, "radius": 26.5 * mm});
            skCircle(sketch, "E966", {"center": v(-1332.5, 281.46) * mm, "radius": 26.5 * mm});
            skCircle(sketch, "E967", {"center": v(-1365, 337.75) * mm, "radius": 26.5 * mm});
            skCircle(sketch, "E968", {"center": v(-1397.5, 394.04) * mm, "radius": 26.5 * mm});
            skCircle(sketch, "E969", {"center": v(-1430, 450.33) * mm, "radius": 26.5 * mm});
            skCircle(sketch, "E970", {"center": v(-1462.5, 506.62) * mm, "radius": 26.5 * mm});
            skCircle(sketch, "E971", {"center": v(-1267.5, 56.3) * mm, "radius": 26.5 * mm});
            skCircle(sketch, "E972", {"center": v(-1300, 112.58) * mm, "radius": 26.5 * mm});
            skCircle(sketch, "E973", {"center": v(-1332.5, 168.87) * mm, "radius": 26.5 * mm});
            skCircle(sketch, "E974", {"center": v(-1365, 225.17) * mm, "radius": 26.5 * mm});
            skCircle(sketch, "E975", {"center": v(-1397.5, 281.46) * mm, "radius": 26.5 * mm});
            skCircle(sketch, "E976", {"center": v(-1430, 337.75) * mm, "radius": 26.5 * mm});
            skCircle(sketch, "E977", {"center": v(-1462.5, 394.04) * mm, "radius": 26.5 * mm});
            skCircle(sketch, "E978", {"center": v(-1495, 450.33) * mm, "radius": 26.5 * mm});
            skCircle(sketch, "E979", {"center": v(-1332.5, 56.3) * mm, "radius": 26.5 * mm});
            skCircle(sketch, "E980", {"center": v(-1365, 112.58) * mm, "radius": 26.5 * mm});
            skCircle(sketch, "E981", {"center": v(-1397.5, 168.87) * mm, "radius": 26.5 * mm});
            skCircle(sketch, "E982", {"center": v(-1430, 225.17) * mm, "radius": 26.5 * mm});
            skCircle(sketch, "E983", {"center": v(-1462.5, 281.46) * mm, "radius": 26.5 * mm});
            skCircle(sketch, "E984", {"center": v(-1495, 337.75) * mm, "radius": 26.5 * mm});
            skCircle(sketch, "E985", {"center": v(-1527.5, 394.04) * mm, "radius": 26.5 * mm});
            skCircle(sketch, "E986", {"center": v(-1397.5, 56.3) * mm, "radius": 26.5 * mm});
            skCircle(sketch, "E987", {"center": v(-1430, 112.58) * mm, "radius": 26.5 * mm});
            skCircle(sketch, "E988", {"center": v(-1462.5, 168.87) * mm, "radius": 26.5 * mm});
            skCircle(sketch, "E989", {"center": v(-1495, 225.17) * mm, "radius": 26.5 * mm});
            skCircle(sketch, "E990", {"center": v(-1527.5, 281.46) * mm, "radius": 26.5 * mm});
            skCircle(sketch, "E991", {"center": v(-1462.5, 56.3) * mm, "radius": 26.5 * mm});
            skCircle(sketch, "E992", {"center": v(-1495, 112.58) * mm, "radius": 26.5 * mm});
            skCircle(sketch, "E993", {"center": v(-1527.5, 168.87) * mm, "radius": 26.5 * mm});
            skCircle(sketch, "E994", {"center": v(-1560, 225.17) * mm, "radius": 26.5 * mm});
            skCircle(sketch, "E995", {"center": v(-1527.5, 56.3) * mm, "radius": 26.5 * mm});
            skCircle(sketch, "E996", {"center": v(-1560, 112.58) * mm, "radius": 26.5 * mm});
            skCircle(sketch, "E997", {"center": v(-975, 562.92) * mm, "radius": 58 * mm});
            skCircle(sketch, "E998", {"center": v(-390, 0) * mm, "radius": 26.5 * mm});
            skCircle(sketch, "E999", {"center": v(-455, 0) * mm, "radius": 26.5 * mm});
            skCircle(sketch, "E1000", {"center": v(-520, 0) * mm, "radius": 26.5 * mm});
            skCircle(sketch, "E1001", {"center": v(-585, 0) * mm, "radius": 26.5 * mm});
            skCircle(sketch, "E1002", {"center": v(-650, 0) * mm, "radius": 26.5 * mm});
            skCircle(sketch, "E1003", {"center": v(-715, 0) * mm, "radius": 26.5 * mm});
            skCircle(sketch, "E1004", {"center": v(-780, 0) * mm, "radius": 26.5 * mm});
            skCircle(sketch, "E1005", {"center": v(-845, 0) * mm, "radius": 26.5 * mm});
            skCircle(sketch, "E1006", {"center": v(-910, 0) * mm, "radius": 26.5 * mm});
            skCircle(sketch, "E1007", {"center": v(-975, 0) * mm, "radius": 26.5 * mm});
            skCircle(sketch, "E1008", {"center": v(-1040, 0) * mm, "radius": 26.5 * mm});
            skCircle(sketch, "E1009", {"center": v(-1105, 0) * mm, "radius": 26.5 * mm});
            skCircle(sketch, "E1010", {"center": v(-1170, 0) * mm, "radius": 26.5 * mm});
            skCircle(sketch, "E1011", {"center": v(-1235, 0) * mm, "radius": 26.5 * mm});
            skCircle(sketch, "E1012", {"center": v(-1300, 0) * mm, "radius": 26.5 * mm});
            skCircle(sketch, "E1013", {"center": v(-1365, 0) * mm, "radius": 26.5 * mm});
            skCircle(sketch, "E1014", {"center": v(-1430, 0) * mm, "radius": 26.5 * mm});
            skCircle(sketch, "E1015", {"center": v(-1495, 0) * mm, "radius": 26.5 * mm});
            skCircle(sketch, "E1016", {"center": v(-1560, 0) * mm, "radius": 26.5 * mm});
            skCircle(sketch, "E1017", {"center": v(-422.5, -56.3) * mm, "radius": 26.5 * mm});
            skCircle(sketch, "E1018", {"center": v(-487.5, -56.3) * mm, "radius": 26.5 * mm});
            skCircle(sketch, "E1019", {"center": v(-552.5, -56.3) * mm, "radius": 26.5 * mm});
            skCircle(sketch, "E1020", {"center": v(-617.5, -56.3) * mm, "radius": 26.5 * mm});
            skCircle(sketch, "E1021", {"center": v(-682.5, -56.3) * mm, "radius": 26.5 * mm});
            skCircle(sketch, "E1022", {"center": v(-747.5, -56.3) * mm, "radius": 26.5 * mm});
            skCircle(sketch, "E1023", {"center": v(-812.5, -56.3) * mm, "radius": 26.5 * mm});
            skCircle(sketch, "E1024", {"center": v(-877.5, -56.3) * mm, "radius": 26.5 * mm});
            skCircle(sketch, "E1025", {"center": v(-942.5, -56.3) * mm, "radius": 26.5 * mm});
            skCircle(sketch, "E1026", {"center": v(-1007.5, -56.3) * mm, "radius": 26.5 * mm});
            skCircle(sketch, "E1027", {"center": v(-1072.5, -56.3) * mm, "radius": 26.5 * mm});
            skCircle(sketch, "E1028", {"center": v(-1137.5, -56.3) * mm, "radius": 26.5 * mm});
            skCircle(sketch, "E1029", {"center": v(-1202.5, -56.3) * mm, "radius": 26.5 * mm});
            skCircle(sketch, "E1030", {"center": v(-1267.5, -56.3) * mm, "radius": 26.5 * mm});
            skCircle(sketch, "E1031", {"center": v(-1332.5, -56.3) * mm, "radius": 26.5 * mm});
            skCircle(sketch, "E1032", {"center": v(-1397.5, -56.3) * mm, "radius": 26.5 * mm});
            skCircle(sketch, "E1033", {"center": v(-1462.5, -56.3) * mm, "radius": 26.5 * mm});
            skCircle(sketch, "E1034", {"center": v(-1527.5, -56.3) * mm, "radius": 26.5 * mm});
            skCircle(sketch, "E1035", {"center": v(-390, -112.58) * mm, "radius": 26.5 * mm});
            skCircle(sketch, "E1036", {"center": v(-455, -112.58) * mm, "radius": 26.5 * mm});
            skCircle(sketch, "E1037", {"center": v(-520, -112.58) * mm, "radius": 26.5 * mm});
            skCircle(sketch, "E1038", {"center": v(-585, -112.58) * mm, "radius": 26.5 * mm});
            skCircle(sketch, "E1039", {"center": v(-650, -112.58) * mm, "radius": 26.5 * mm});
            skCircle(sketch, "E1040", {"center": v(-715, -112.58) * mm, "radius": 26.5 * mm});
            skCircle(sketch, "E1041", {"center": v(-780, -112.58) * mm, "radius": 26.5 * mm});
            skCircle(sketch, "E1042", {"center": v(-845, -112.58) * mm, "radius": 26.5 * mm});
            skCircle(sketch, "E1043", {"center": v(-910, -112.58) * mm, "radius": 26.5 * mm});
            skCircle(sketch, "E1044", {"center": v(-975, -112.58) * mm, "radius": 26.5 * mm});
            skCircle(sketch, "E1045", {"center": v(-1040, -112.58) * mm, "radius": 26.5 * mm});
            skCircle(sketch, "E1046", {"center": v(-1105, -112.58) * mm, "radius": 26.5 * mm});
            skCircle(sketch, "E1047", {"center": v(-1170, -112.58) * mm, "radius": 26.5 * mm});
            skCircle(sketch, "E1048", {"center": v(-1235, -112.58) * mm, "radius": 26.5 * mm});
            skCircle(sketch, "E1049", {"center": v(-1300, -112.58) * mm, "radius": 26.5 * mm});
            skCircle(sketch, "E1050", {"center": v(-1365, -112.58) * mm, "radius": 26.5 * mm});
            skCircle(sketch, "E1051", {"center": v(-1430, -112.58) * mm, "radius": 26.5 * mm});
            skCircle(sketch, "E1052", {"center": v(-1495, -112.58) * mm, "radius": 26.5 * mm});
            skCircle(sketch, "E1053", {"center": v(-1560, -112.58) * mm, "radius": 26.5 * mm});
            skCircle(sketch, "E1054", {"center": v(-357.5, -168.87) * mm, "radius": 26.5 * mm});
            skCircle(sketch, "E1055", {"center": v(-422.5, -168.87) * mm, "radius": 26.5 * mm});
            skCircle(sketch, "E1056", {"center": v(-487.5, -168.87) * mm, "radius": 26.5 * mm});
            skCircle(sketch, "E1057", {"center": v(-552.5, -168.87) * mm, "radius": 26.5 * mm});
            skCircle(sketch, "E1058", {"center": v(-617.5, -168.87) * mm, "radius": 26.5 * mm});
            skCircle(sketch, "E1059", {"center": v(-682.5, -168.87) * mm, "radius": 26.5 * mm});
            skCircle(sketch, "E1060", {"center": v(-747.5, -168.87) * mm, "radius": 26.5 * mm});
            skCircle(sketch, "E1061", {"center": v(-812.5, -168.87) * mm, "radius": 26.5 * mm});
            skCircle(sketch, "E1062", {"center": v(-877.5, -168.87) * mm, "radius": 26.5 * mm});
            skCircle(sketch, "E1063", {"center": v(-942.5, -168.87) * mm, "radius": 26.5 * mm});
            skCircle(sketch, "E1064", {"center": v(-1007.5, -168.87) * mm, "radius": 26.5 * mm});
            skCircle(sketch, "E1065", {"center": v(-1072.5, -168.87) * mm, "radius": 26.5 * mm});
            skCircle(sketch, "E1066", {"center": v(-1137.5, -168.87) * mm, "radius": 26.5 * mm});
            skCircle(sketch, "E1067", {"center": v(-1202.5, -168.87) * mm, "radius": 26.5 * mm});
            skCircle(sketch, "E1068", {"center": v(-1267.5, -168.87) * mm, "radius": 26.5 * mm});
            skCircle(sketch, "E1069", {"center": v(-1332.5, -168.87) * mm, "radius": 26.5 * mm});
            skCircle(sketch, "E1070", {"center": v(-1397.5, -168.87) * mm, "radius": 26.5 * mm});
            skCircle(sketch, "E1071", {"center": v(-1462.5, -168.87) * mm, "radius": 26.5 * mm});
            skCircle(sketch, "E1072", {"center": v(-1527.5, -168.87) * mm, "radius": 26.5 * mm});
            skCircle(sketch, "E1073", {"center": v(-325, -225.17) * mm, "radius": 26.5 * mm});
            skCircle(sketch, "E1074", {"center": v(-390, -225.17) * mm, "radius": 26.5 * mm});
            skCircle(sketch, "E1075", {"center": v(-455, -225.17) * mm, "radius": 26.5 * mm});
            skCircle(sketch, "E1076", {"center": v(-520, -225.17) * mm, "radius": 26.5 * mm});
            skCircle(sketch, "E1077", {"center": v(-585, -225.17) * mm, "radius": 26.5 * mm});
            skCircle(sketch, "E1078", {"center": v(-650, -225.17) * mm, "radius": 26.5 * mm});
            skCircle(sketch, "E1079", {"center": v(-715, -225.17) * mm, "radius": 26.5 * mm});
            skCircle(sketch, "E1080", {"center": v(-780, -225.17) * mm, "radius": 26.5 * mm});
            skCircle(sketch, "E1081", {"center": v(-845, -225.17) * mm, "radius": 26.5 * mm});
            skCircle(sketch, "E1082", {"center": v(-910, -225.17) * mm, "radius": 26.5 * mm});
            skCircle(sketch, "E1083", {"center": v(-975, -225.17) * mm, "radius": 26.5 * mm});
            skCircle(sketch, "E1084", {"center": v(-1040, -225.17) * mm, "radius": 26.5 * mm});
            skCircle(sketch, "E1085", {"center": v(-1105, -225.17) * mm, "radius": 26.5 * mm});
            skCircle(sketch, "E1086", {"center": v(-1170, -225.17) * mm, "radius": 26.5 * mm});
            skCircle(sketch, "E1087", {"center": v(-1235, -225.17) * mm, "radius": 26.5 * mm});
            skCircle(sketch, "E1088", {"center": v(-1300, -225.17) * mm, "radius": 26.5 * mm});
            skCircle(sketch, "E1089", {"center": v(-1365, -225.17) * mm, "radius": 26.5 * mm});
            skCircle(sketch, "E1090", {"center": v(-1430, -225.17) * mm, "radius": 26.5 * mm});
            skCircle(sketch, "E1091", {"center": v(-1495, -225.17) * mm, "radius": 26.5 * mm});
            skCircle(sketch, "E1092", {"center": v(-1560, -225.17) * mm, "radius": 26.5 * mm});
            skCircle(sketch, "E1093", {"center": v(-292.5, -281.46) * mm, "radius": 26.5 * mm});
            skCircle(sketch, "E1094", {"center": v(-357.5, -281.46) * mm, "radius": 26.5 * mm});
            skCircle(sketch, "E1095", {"center": v(-422.5, -281.46) * mm, "radius": 26.5 * mm});
            skCircle(sketch, "E1096", {"center": v(-487.5, -281.46) * mm, "radius": 26.5 * mm});
            skCircle(sketch, "E1097", {"center": v(-552.5, -281.46) * mm, "radius": 26.5 * mm});
            skCircle(sketch, "E1098", {"center": v(-617.5, -281.46) * mm, "radius": 26.5 * mm});
            skCircle(sketch, "E1099", {"center": v(-682.5, -281.46) * mm, "radius": 26.5 * mm});
            skCircle(sketch, "E1100", {"center": v(-747.5, -281.46) * mm, "radius": 26.5 * mm});
            skCircle(sketch, "E1101", {"center": v(-812.5, -281.46) * mm, "radius": 26.5 * mm});
            skCircle(sketch, "E1102", {"center": v(-877.5, -281.46) * mm, "radius": 26.5 * mm});
            skCircle(sketch, "E1103", {"center": v(-942.5, -281.46) * mm, "radius": 26.5 * mm});
            skCircle(sketch, "E1104", {"center": v(-1007.5, -281.46) * mm, "radius": 26.5 * mm});
            skCircle(sketch, "E1105", {"center": v(-1072.5, -281.46) * mm, "radius": 26.5 * mm});
            skCircle(sketch, "E1106", {"center": v(-1137.5, -281.46) * mm, "radius": 26.5 * mm});
            skCircle(sketch, "E1107", {"center": v(-1202.5, -281.46) * mm, "radius": 26.5 * mm});
            skCircle(sketch, "E1108", {"center": v(-1267.5, -281.46) * mm, "radius": 26.5 * mm});
            skCircle(sketch, "E1109", {"center": v(-1332.5, -281.46) * mm, "radius": 26.5 * mm});
            skCircle(sketch, "E1110", {"center": v(-1397.5, -281.46) * mm, "radius": 26.5 * mm});
            skCircle(sketch, "E1111", {"center": v(-1462.5, -281.46) * mm, "radius": 26.5 * mm});
            skCircle(sketch, "E1112", {"center": v(-1527.5, -281.46) * mm, "radius": 26.5 * mm});
            skCircle(sketch, "E1113", {"center": v(-260, -337.75) * mm, "radius": 26.5 * mm});
            skCircle(sketch, "E1114", {"center": v(-325, -337.75) * mm, "radius": 26.5 * mm});
            skCircle(sketch, "E1115", {"center": v(-390, -337.75) * mm, "radius": 26.5 * mm});
            skCircle(sketch, "E1116", {"center": v(-455, -337.75) * mm, "radius": 26.5 * mm});
            skCircle(sketch, "E1117", {"center": v(-520, -337.75) * mm, "radius": 26.5 * mm});
            skCircle(sketch, "E1118", {"center": v(-585, -337.75) * mm, "radius": 26.5 * mm});
            skCircle(sketch, "E1119", {"center": v(-650, -337.75) * mm, "radius": 26.5 * mm});
            skCircle(sketch, "E1120", {"center": v(-715, -337.75) * mm, "radius": 26.5 * mm});
            skCircle(sketch, "E1121", {"center": v(-780, -337.75) * mm, "radius": 26.5 * mm});
            skCircle(sketch, "E1122", {"center": v(-845, -337.75) * mm, "radius": 26.5 * mm});
            skCircle(sketch, "E1123", {"center": v(-910, -337.75) * mm, "radius": 26.5 * mm});
            skCircle(sketch, "E1124", {"center": v(-975, -337.75) * mm, "radius": 26.5 * mm});
            skCircle(sketch, "E1125", {"center": v(-1040, -337.75) * mm, "radius": 26.5 * mm});
            skCircle(sketch, "E1126", {"center": v(-1105, -337.75) * mm, "radius": 26.5 * mm});
            skCircle(sketch, "E1127", {"center": v(-1170, -337.75) * mm, "radius": 26.5 * mm});
            skCircle(sketch, "E1128", {"center": v(-1235, -337.75) * mm, "radius": 26.5 * mm});
            skCircle(sketch, "E1129", {"center": v(-1300, -337.75) * mm, "radius": 26.5 * mm});
            skCircle(sketch, "E1130", {"center": v(-1365, -337.75) * mm, "radius": 26.5 * mm});
            skCircle(sketch, "E1131", {"center": v(-1430, -337.75) * mm, "radius": 26.5 * mm});
            skCircle(sketch, "E1132", {"center": v(-1495, -337.75) * mm, "radius": 26.5 * mm});
            skCircle(sketch, "E1133", {"center": v(-292.5, -394.04) * mm, "radius": 26.5 * mm});
            skCircle(sketch, "E1134", {"center": v(-357.5, -394.04) * mm, "radius": 26.5 * mm});
            skCircle(sketch, "E1135", {"center": v(-422.5, -394.04) * mm, "radius": 26.5 * mm});
            skCircle(sketch, "E1136", {"center": v(-487.5, -394.04) * mm, "radius": 26.5 * mm});
            skCircle(sketch, "E1137", {"center": v(-552.5, -394.04) * mm, "radius": 26.5 * mm});
            skCircle(sketch, "E1138", {"center": v(-617.5, -394.04) * mm, "radius": 26.5 * mm});
            skCircle(sketch, "E1139", {"center": v(-682.5, -394.04) * mm, "radius": 26.5 * mm});
            skCircle(sketch, "E1140", {"center": v(-747.5, -394.04) * mm, "radius": 26.5 * mm});
            skCircle(sketch, "E1141", {"center": v(-812.5, -394.04) * mm, "radius": 26.5 * mm});
            skCircle(sketch, "E1142", {"center": v(-877.5, -394.04) * mm, "radius": 26.5 * mm});
            skCircle(sketch, "E1143", {"center": v(-942.5, -394.04) * mm, "radius": 26.5 * mm});
            skCircle(sketch, "E1144", {"center": v(-1007.5, -394.04) * mm, "radius": 26.5 * mm});
            skCircle(sketch, "E1145", {"center": v(-1072.5, -394.04) * mm, "radius": 26.5 * mm});
            skCircle(sketch, "E1146", {"center": v(-1137.5, -394.04) * mm, "radius": 26.5 * mm});
            skCircle(sketch, "E1147", {"center": v(-1202.5, -394.04) * mm, "radius": 26.5 * mm});
            skCircle(sketch, "E1148", {"center": v(-1267.5, -394.04) * mm, "radius": 26.5 * mm});
            skCircle(sketch, "E1149", {"center": v(-1332.5, -394.04) * mm, "radius": 26.5 * mm});
            skCircle(sketch, "E1150", {"center": v(-1397.5, -394.04) * mm, "radius": 26.5 * mm});
            skCircle(sketch, "E1151", {"center": v(-1462.5, -394.04) * mm, "radius": 26.5 * mm});
            skCircle(sketch, "E1152", {"center": v(-1527.5, -394.04) * mm, "radius": 26.5 * mm});
            skCircle(sketch, "E1153", {"center": v(-325, -450.33) * mm, "radius": 26.5 * mm});
            skCircle(sketch, "E1154", {"center": v(-390, -450.33) * mm, "radius": 26.5 * mm});
            skCircle(sketch, "E1155", {"center": v(-455, -450.33) * mm, "radius": 26.5 * mm});
            skCircle(sketch, "E1156", {"center": v(-520, -450.33) * mm, "radius": 26.5 * mm});
            skCircle(sketch, "E1157", {"center": v(-585, -450.33) * mm, "radius": 26.5 * mm});
            skCircle(sketch, "E1158", {"center": v(-650, -450.33) * mm, "radius": 26.5 * mm});
            skCircle(sketch, "E1159", {"center": v(-715, -450.33) * mm, "radius": 26.5 * mm});
            skCircle(sketch, "E1160", {"center": v(-780, -450.33) * mm, "radius": 26.5 * mm});
            skCircle(sketch, "E1161", {"center": v(-845, -450.33) * mm, "radius": 26.5 * mm});
            skCircle(sketch, "E1162", {"center": v(-910, -450.33) * mm, "radius": 26.5 * mm});
            skCircle(sketch, "E1163", {"center": v(-975, -450.33) * mm, "radius": 26.5 * mm});
            skCircle(sketch, "E1164", {"center": v(-1040, -450.33) * mm, "radius": 26.5 * mm});
            skCircle(sketch, "E1165", {"center": v(-1105, -450.33) * mm, "radius": 26.5 * mm});
            skCircle(sketch, "E1166", {"center": v(-1170, -450.33) * mm, "radius": 26.5 * mm});
            skCircle(sketch, "E1167", {"center": v(-1235, -450.33) * mm, "radius": 26.5 * mm});
            skCircle(sketch, "E1168", {"center": v(-1300, -450.33) * mm, "radius": 26.5 * mm});
            skCircle(sketch, "E1169", {"center": v(-1365, -450.33) * mm, "radius": 26.5 * mm});
            skCircle(sketch, "E1170", {"center": v(-1430, -450.33) * mm, "radius": 26.5 * mm});
            skCircle(sketch, "E1171", {"center": v(-1495, -450.33) * mm, "radius": 26.5 * mm});
            skCircle(sketch, "E1172", {"center": v(-357.5, -506.62) * mm, "radius": 26.5 * mm});
            skCircle(sketch, "E1173", {"center": v(-422.5, -506.62) * mm, "radius": 26.5 * mm});
            skCircle(sketch, "E1174", {"center": v(-487.5, -506.62) * mm, "radius": 26.5 * mm});
            skCircle(sketch, "E1175", {"center": v(-552.5, -506.62) * mm, "radius": 26.5 * mm});
            skCircle(sketch, "E1176", {"center": v(-617.5, -506.62) * mm, "radius": 26.5 * mm});
            skCircle(sketch, "E1177", {"center": v(-682.5, -506.62) * mm, "radius": 26.5 * mm});
            skCircle(sketch, "E1178", {"center": v(-747.5, -506.62) * mm, "radius": 26.5 * mm});
            skCircle(sketch, "E1179", {"center": v(-812.5, -506.62) * mm, "radius": 26.5 * mm});
            skCircle(sketch, "E1180", {"center": v(-877.5, -506.62) * mm, "radius": 26.5 * mm});
            skCircle(sketch, "E1181", {"center": v(-1072.5, -506.62) * mm, "radius": 26.5 * mm});
            skCircle(sketch, "E1182", {"center": v(-1137.5, -506.62) * mm, "radius": 26.5 * mm});
            skCircle(sketch, "E1183", {"center": v(-1202.5, -506.62) * mm, "radius": 26.5 * mm});
            skCircle(sketch, "E1184", {"center": v(-1267.5, -506.62) * mm, "radius": 26.5 * mm});
            skCircle(sketch, "E1185", {"center": v(-1332.5, -506.62) * mm, "radius": 26.5 * mm});
            skCircle(sketch, "E1186", {"center": v(-1397.5, -506.62) * mm, "radius": 26.5 * mm});
            skCircle(sketch, "E1187", {"center": v(-1462.5, -506.62) * mm, "radius": 26.5 * mm});
            skCircle(sketch, "E1188", {"center": v(-390, -562.92) * mm, "radius": 26.5 * mm});
            skCircle(sketch, "E1189", {"center": v(-455, -562.92) * mm, "radius": 26.5 * mm});
            skCircle(sketch, "E1190", {"center": v(-520, -562.92) * mm, "radius": 26.5 * mm});
            skCircle(sketch, "E1191", {"center": v(-585, -562.92) * mm, "radius": 26.5 * mm});
            skCircle(sketch, "E1192", {"center": v(-650, -562.92) * mm, "radius": 26.5 * mm});
            skCircle(sketch, "E1193", {"center": v(-715, -562.92) * mm, "radius": 26.5 * mm});
            skCircle(sketch, "E1194", {"center": v(-780, -562.92) * mm, "radius": 26.5 * mm});
            skCircle(sketch, "E1195", {"center": v(-845, -562.92) * mm, "radius": 26.5 * mm});
            skCircle(sketch, "E1196", {"center": v(-1105, -562.92) * mm, "radius": 26.5 * mm});
            skCircle(sketch, "E1197", {"center": v(-1170, -562.92) * mm, "radius": 26.5 * mm});
            skCircle(sketch, "E1198", {"center": v(-1235, -562.92) * mm, "radius": 26.5 * mm});
            skCircle(sketch, "E1199", {"center": v(-1300, -562.92) * mm, "radius": 26.5 * mm});
            skCircle(sketch, "E1200", {"center": v(-1365, -562.92) * mm, "radius": 26.5 * mm});
            skCircle(sketch, "E1201", {"center": v(-1430, -562.92) * mm, "radius": 26.5 * mm});
            skCircle(sketch, "E1202", {"center": v(-422.5, -619.2) * mm, "radius": 26.5 * mm});
            skCircle(sketch, "E1203", {"center": v(-487.5, -619.2) * mm, "radius": 26.5 * mm});
            skCircle(sketch, "E1204", {"center": v(-552.5, -619.2) * mm, "radius": 26.5 * mm});
            skCircle(sketch, "E1205", {"center": v(-617.5, -619.2) * mm, "radius": 26.5 * mm});
            skCircle(sketch, "E1206", {"center": v(-682.5, -619.2) * mm, "radius": 26.5 * mm});
            skCircle(sketch, "E1207", {"center": v(-747.5, -619.2) * mm, "radius": 26.5 * mm});
            skCircle(sketch, "E1208", {"center": v(-812.5, -619.2) * mm, "radius": 26.5 * mm});
            skCircle(sketch, "E1209", {"center": v(-877.5, -619.2) * mm, "radius": 26.5 * mm});
            skCircle(sketch, "E1210", {"center": v(-1072.5, -619.2) * mm, "radius": 26.5 * mm});
            skCircle(sketch, "E1211", {"center": v(-1137.5, -619.2) * mm, "radius": 26.5 * mm});
            skCircle(sketch, "E1212", {"center": v(-1202.5, -619.2) * mm, "radius": 26.5 * mm});
            skCircle(sketch, "E1213", {"center": v(-1267.5, -619.2) * mm, "radius": 26.5 * mm});
            skCircle(sketch, "E1214", {"center": v(-1332.5, -619.2) * mm, "radius": 26.5 * mm});
            skCircle(sketch, "E1215", {"center": v(-1397.5, -619.2) * mm, "radius": 26.5 * mm});
            skCircle(sketch, "E1216", {"center": v(-455, -675.5) * mm, "radius": 26.5 * mm});
            skCircle(sketch, "E1217", {"center": v(-520, -675.5) * mm, "radius": 26.5 * mm});
            skCircle(sketch, "E1218", {"center": v(-585, -675.5) * mm, "radius": 26.5 * mm});
            skCircle(sketch, "E1219", {"center": v(-650, -675.5) * mm, "radius": 26.5 * mm});
            skCircle(sketch, "E1220", {"center": v(-715, -675.5) * mm, "radius": 26.5 * mm});
            skCircle(sketch, "E1221", {"center": v(-780, -675.5) * mm, "radius": 26.5 * mm});
            skCircle(sketch, "E1222", {"center": v(-845, -675.5) * mm, "radius": 26.5 * mm});
            skCircle(sketch, "E1223", {"center": v(-910, -675.5) * mm, "radius": 26.5 * mm});
            skCircle(sketch, "E1224", {"center": v(-975, -675.5) * mm, "radius": 26.5 * mm});
            skCircle(sketch, "E1225", {"center": v(-1040, -675.5) * mm, "radius": 26.5 * mm});
            skCircle(sketch, "E1226", {"center": v(-1105, -675.5) * mm, "radius": 26.5 * mm});
            skCircle(sketch, "E1227", {"center": v(-1170, -675.5) * mm, "radius": 26.5 * mm});
            skCircle(sketch, "E1228", {"center": v(-1235, -675.5) * mm, "radius": 26.5 * mm});
            skCircle(sketch, "E1229", {"center": v(-1300, -675.5) * mm, "radius": 26.5 * mm});
            skCircle(sketch, "E1230", {"center": v(-1365, -675.5) * mm, "radius": 26.5 * mm});
            skCircle(sketch, "E1231", {"center": v(-487.5, -731.8) * mm, "radius": 26.5 * mm});
            skCircle(sketch, "E1232", {"center": v(-552.5, -731.8) * mm, "radius": 26.5 * mm});
            skCircle(sketch, "E1233", {"center": v(-617.5, -731.8) * mm, "radius": 26.5 * mm});
            skCircle(sketch, "E1234", {"center": v(-682.5, -731.8) * mm, "radius": 26.5 * mm});
            skCircle(sketch, "E1235", {"center": v(-747.5, -731.8) * mm, "radius": 26.5 * mm});
            skCircle(sketch, "E1236", {"center": v(-812.5, -731.8) * mm, "radius": 26.5 * mm});
            skCircle(sketch, "E1237", {"center": v(-877.5, -731.8) * mm, "radius": 26.5 * mm});
            skCircle(sketch, "E1238", {"center": v(-942.5, -731.8) * mm, "radius": 26.5 * mm});
            skCircle(sketch, "E1239", {"center": v(-1007.5, -731.8) * mm, "radius": 26.5 * mm});
            skCircle(sketch, "E1240", {"center": v(-1072.5, -731.8) * mm, "radius": 26.5 * mm});
            skCircle(sketch, "E1241", {"center": v(-1137.5, -731.8) * mm, "radius": 26.5 * mm});
            skCircle(sketch, "E1242", {"center": v(-1202.5, -731.8) * mm, "radius": 26.5 * mm});
            skCircle(sketch, "E1243", {"center": v(-1267.5, -731.8) * mm, "radius": 26.5 * mm});
            skCircle(sketch, "E1244", {"center": v(-1332.5, -731.8) * mm, "radius": 26.5 * mm});
            skCircle(sketch, "E1245", {"center": v(-1397.5, -731.8) * mm, "radius": 26.5 * mm});
            skCircle(sketch, "E1246", {"center": v(-520, -788.08) * mm, "radius": 26.5 * mm});
            skCircle(sketch, "E1247", {"center": v(-585, -788.08) * mm, "radius": 26.5 * mm});
            skCircle(sketch, "E1248", {"center": v(-650, -788.08) * mm, "radius": 26.5 * mm});
            skCircle(sketch, "E1249", {"center": v(-715, -788.08) * mm, "radius": 26.5 * mm});
            skCircle(sketch, "E1250", {"center": v(-780, -788.08) * mm, "radius": 26.5 * mm});
            skCircle(sketch, "E1251", {"center": v(-845, -788.08) * mm, "radius": 26.5 * mm});
            skCircle(sketch, "E1252", {"center": v(-910, -788.08) * mm, "radius": 26.5 * mm});
            skCircle(sketch, "E1253", {"center": v(-975, -788.08) * mm, "radius": 26.5 * mm});
            skCircle(sketch, "E1254", {"center": v(-1040, -788.08) * mm, "radius": 26.5 * mm});
            skCircle(sketch, "E1255", {"center": v(-1105, -788.08) * mm, "radius": 26.5 * mm});
            skCircle(sketch, "E1256", {"center": v(-1170, -788.08) * mm, "radius": 26.5 * mm});
            skCircle(sketch, "E1257", {"center": v(-1235, -788.08) * mm, "radius": 26.5 * mm});
            skCircle(sketch, "E1258", {"center": v(-1300, -788.08) * mm, "radius": 26.5 * mm});
            skCircle(sketch, "E1259", {"center": v(-1365, -788.08) * mm, "radius": 26.5 * mm});
            skCircle(sketch, "E1260", {"center": v(-552.5, -844.37) * mm, "radius": 26.5 * mm});
            skCircle(sketch, "E1261", {"center": v(-617.5, -844.37) * mm, "radius": 26.5 * mm});
            skCircle(sketch, "E1262", {"center": v(-682.5, -844.37) * mm, "radius": 26.5 * mm});
            skCircle(sketch, "E1263", {"center": v(-747.5, -844.37) * mm, "radius": 26.5 * mm});
            skCircle(sketch, "E1264", {"center": v(-812.5, -844.37) * mm, "radius": 26.5 * mm});
            skCircle(sketch, "E1265", {"center": v(-877.5, -844.37) * mm, "radius": 26.5 * mm});
            skCircle(sketch, "E1266", {"center": v(-942.5, -844.37) * mm, "radius": 26.5 * mm});
            skCircle(sketch, "E1267", {"center": v(-1007.5, -844.37) * mm, "radius": 26.5 * mm});
            skCircle(sketch, "E1268", {"center": v(-1072.5, -844.37) * mm, "radius": 26.5 * mm});
            skCircle(sketch, "E1269", {"center": v(-1137.5, -844.37) * mm, "radius": 26.5 * mm});
            skCircle(sketch, "E1270", {"center": v(-1202.5, -844.37) * mm, "radius": 26.5 * mm});
            skCircle(sketch, "E1271", {"center": v(-1267.5, -844.37) * mm, "radius": 26.5 * mm});
            skCircle(sketch, "E1272", {"center": v(-1332.5, -844.37) * mm, "radius": 26.5 * mm});
            skCircle(sketch, "E1273", {"center": v(-585, -900.67) * mm, "radius": 26.5 * mm});
            skCircle(sketch, "E1274", {"center": v(-650, -900.67) * mm, "radius": 26.5 * mm});
            skCircle(sketch, "E1275", {"center": v(-715, -900.67) * mm, "radius": 26.5 * mm});
            skCircle(sketch, "E1276", {"center": v(-780, -900.67) * mm, "radius": 26.5 * mm});
            skCircle(sketch, "E1277", {"center": v(-845, -900.67) * mm, "radius": 26.5 * mm});
            skCircle(sketch, "E1278", {"center": v(-910, -900.67) * mm, "radius": 26.5 * mm});
            skCircle(sketch, "E1279", {"center": v(-975, -900.67) * mm, "radius": 26.5 * mm});
            skCircle(sketch, "E1280", {"center": v(-1040, -900.67) * mm, "radius": 26.5 * mm});
            skCircle(sketch, "E1281", {"center": v(-1105, -900.67) * mm, "radius": 26.5 * mm});
            skCircle(sketch, "E1282", {"center": v(-1170, -900.67) * mm, "radius": 26.5 * mm});
            skCircle(sketch, "E1283", {"center": v(-1235, -900.67) * mm, "radius": 26.5 * mm});
            skCircle(sketch, "E1284", {"center": v(-617.5, -956.96) * mm, "radius": 26.5 * mm});
            skCircle(sketch, "E1285", {"center": v(-682.5, -956.96) * mm, "radius": 26.5 * mm});
            skCircle(sketch, "E1286", {"center": v(-747.5, -956.96) * mm, "radius": 26.5 * mm});
            skCircle(sketch, "E1287", {"center": v(-812.5, -956.96) * mm, "radius": 26.5 * mm});
            skCircle(sketch, "E1288", {"center": v(-877.5, -956.96) * mm, "radius": 26.5 * mm});
            skCircle(sketch, "E1289", {"center": v(-942.5, -956.96) * mm, "radius": 26.5 * mm});
            skCircle(sketch, "E1290", {"center": v(-1007.5, -956.96) * mm, "radius": 26.5 * mm});
            skCircle(sketch, "E1291", {"center": v(-1072.5, -956.96) * mm, "radius": 26.5 * mm});
            skCircle(sketch, "E1292", {"center": v(-1137.5, -956.96) * mm, "radius": 26.5 * mm});
            skCircle(sketch, "E1293", {"center": v(-1202.5, -956.96) * mm, "radius": 26.5 * mm});
            skCircle(sketch, "E1294", {"center": v(-650, -1013.25) * mm, "radius": 26.5 * mm});
            skCircle(sketch, "E1295", {"center": v(-715, -1013.25) * mm, "radius": 26.5 * mm});
            skCircle(sketch, "E1296", {"center": v(-780, -1013.25) * mm, "radius": 26.5 * mm});
            skCircle(sketch, "E1297", {"center": v(-845, -1013.25) * mm, "radius": 26.5 * mm});
            skCircle(sketch, "E1298", {"center": v(-910, -1013.25) * mm, "radius": 26.5 * mm});
            skCircle(sketch, "E1299", {"center": v(-975, -1013.25) * mm, "radius": 26.5 * mm});
            skCircle(sketch, "E1300", {"center": v(-1040, -1013.25) * mm, "radius": 26.5 * mm});
            skCircle(sketch, "E1301", {"center": v(-1105, -1013.25) * mm, "radius": 26.5 * mm});
            skCircle(sketch, "E1302", {"center": v(-1170, -1013.25) * mm, "radius": 26.5 * mm});
            skCircle(sketch, "E1303", {"center": v(-682.5, -1069.54) * mm, "radius": 26.5 * mm});
            skCircle(sketch, "E1304", {"center": v(-747.5, -1069.54) * mm, "radius": 26.5 * mm});
            skCircle(sketch, "E1305", {"center": v(-812.5, -1069.54) * mm, "radius": 26.5 * mm});
            skCircle(sketch, "E1306", {"center": v(-877.5, -1069.54) * mm, "radius": 26.5 * mm});
            skCircle(sketch, "E1307", {"center": v(-942.5, -1069.54) * mm, "radius": 26.5 * mm});
            skCircle(sketch, "E1308", {"center": v(-1007.5, -1069.54) * mm, "radius": 26.5 * mm});
            skCircle(sketch, "E1309", {"center": v(-1072.5, -1069.54) * mm, "radius": 26.5 * mm});
            skCircle(sketch, "E1310", {"center": v(-1137.5, -1069.54) * mm, "radius": 26.5 * mm});
            skCircle(sketch, "E1311", {"center": v(-715, -1125.83) * mm, "radius": 26.5 * mm});
            skCircle(sketch, "E1312", {"center": v(-780, -1125.83) * mm, "radius": 26.5 * mm});
            skCircle(sketch, "E1313", {"center": v(-845, -1125.83) * mm, "radius": 26.5 * mm});
            skCircle(sketch, "E1314", {"center": v(-910, -1125.83) * mm, "radius": 26.5 * mm});
            skCircle(sketch, "E1315", {"center": v(-975, -1125.83) * mm, "radius": 26.5 * mm});
            skCircle(sketch, "E1316", {"center": v(-1040, -1125.83) * mm, "radius": 26.5 * mm});
            skCircle(sketch, "E1317", {"center": v(-1105, -1125.83) * mm, "radius": 26.5 * mm});
            skCircle(sketch, "E1318", {"center": v(-747.5, -1182.12) * mm, "radius": 26.5 * mm});
            skCircle(sketch, "E1319", {"center": v(-812.5, -1182.12) * mm, "radius": 26.5 * mm});
            skCircle(sketch, "E1320", {"center": v(-877.5, -1182.12) * mm, "radius": 26.5 * mm});
            skCircle(sketch, "E1321", {"center": v(-942.5, -1182.12) * mm, "radius": 26.5 * mm});
            skCircle(sketch, "E1322", {"center": v(-1007.5, -1182.12) * mm, "radius": 26.5 * mm});
            skCircle(sketch, "E1323", {"center": v(-780, -1238.42) * mm, "radius": 26.5 * mm});
            skCircle(sketch, "E1324", {"center": v(-845, -1238.42) * mm, "radius": 26.5 * mm});
            skCircle(sketch, "E1325", {"center": v(-910, -1238.42) * mm, "radius": 26.5 * mm});
            skCircle(sketch, "E1326", {"center": v(-975, -1238.42) * mm, "radius": 26.5 * mm});
            skCircle(sketch, "E1327", {"center": v(-812.5, -1294.7) * mm, "radius": 26.5 * mm});
            skCircle(sketch, "E1328", {"center": v(-877.5, -1294.7) * mm, "radius": 26.5 * mm});
            skCircle(sketch, "E1329", {"center": v(-975, -562.92) * mm, "radius": 58 * mm});
            skCircle(sketch, "E1330", {"center": v(-195, -337.75) * mm, "radius": 26.5 * mm});
            skCircle(sketch, "E1331", {"center": v(-227.5, -394.04) * mm, "radius": 26.5 * mm});
            skCircle(sketch, "E1332", {"center": v(-260, -450.33) * mm, "radius": 26.5 * mm});
            skCircle(sketch, "E1333", {"center": v(-292.5, -506.62) * mm, "radius": 26.5 * mm});
            skCircle(sketch, "E1334", {"center": v(-325, -562.92) * mm, "radius": 26.5 * mm});
            skCircle(sketch, "E1335", {"center": v(-357.5, -619.2) * mm, "radius": 26.5 * mm});
            skCircle(sketch, "E1336", {"center": v(-390, -675.5) * mm, "radius": 26.5 * mm});
            skCircle(sketch, "E1337", {"center": v(-422.5, -731.8) * mm, "radius": 26.5 * mm});
            skCircle(sketch, "E1338", {"center": v(-455, -788.08) * mm, "radius": 26.5 * mm});
            skCircle(sketch, "E1339", {"center": v(-487.5, -844.37) * mm, "radius": 26.5 * mm});
            skCircle(sketch, "E1340", {"center": v(-520, -900.67) * mm, "radius": 26.5 * mm});
            skCircle(sketch, "E1341", {"center": v(-552.5, -956.96) * mm, "radius": 26.5 * mm});
            skCircle(sketch, "E1342", {"center": v(-585, -1013.25) * mm, "radius": 26.5 * mm});
            skCircle(sketch, "E1343", {"center": v(-617.5, -1069.54) * mm, "radius": 26.5 * mm});
            skCircle(sketch, "E1344", {"center": v(-650, -1125.83) * mm, "radius": 26.5 * mm});
            skCircle(sketch, "E1345", {"center": v(-682.5, -1182.12) * mm, "radius": 26.5 * mm});
            skCircle(sketch, "E1346", {"center": v(-715, -1238.42) * mm, "radius": 26.5 * mm});
            skCircle(sketch, "E1347", {"center": v(-747.5, -1294.7) * mm, "radius": 26.5 * mm});
            skCircle(sketch, "E1348", {"center": v(-780, -1351) * mm, "radius": 26.5 * mm});
            skCircle(sketch, "E1349", {"center": v(-162.5, -394.04) * mm, "radius": 26.5 * mm});
            skCircle(sketch, "E1350", {"center": v(-195, -450.33) * mm, "radius": 26.5 * mm});
            skCircle(sketch, "E1351", {"center": v(-227.5, -506.62) * mm, "radius": 26.5 * mm});
            skCircle(sketch, "E1352", {"center": v(-260, -562.92) * mm, "radius": 26.5 * mm});
            skCircle(sketch, "E1353", {"center": v(-292.5, -619.2) * mm, "radius": 26.5 * mm});
            skCircle(sketch, "E1354", {"center": v(-325, -675.5) * mm, "radius": 26.5 * mm});
            skCircle(sketch, "E1355", {"center": v(-357.5, -731.8) * mm, "radius": 26.5 * mm});
            skCircle(sketch, "E1356", {"center": v(-390, -788.08) * mm, "radius": 26.5 * mm});
            skCircle(sketch, "E1357", {"center": v(-422.5, -844.37) * mm, "radius": 26.5 * mm});
            skCircle(sketch, "E1358", {"center": v(-455, -900.67) * mm, "radius": 26.5 * mm});
            skCircle(sketch, "E1359", {"center": v(-487.5, -956.96) * mm, "radius": 26.5 * mm});
            skCircle(sketch, "E1360", {"center": v(-520, -1013.25) * mm, "radius": 26.5 * mm});
            skCircle(sketch, "E1361", {"center": v(-552.5, -1069.54) * mm, "radius": 26.5 * mm});
            skCircle(sketch, "E1362", {"center": v(-585, -1125.83) * mm, "radius": 26.5 * mm});
            skCircle(sketch, "E1363", {"center": v(-617.5, -1182.12) * mm, "radius": 26.5 * mm});
            skCircle(sketch, "E1364", {"center": v(-650, -1238.42) * mm, "radius": 26.5 * mm});
            skCircle(sketch, "E1365", {"center": v(-682.5, -1294.7) * mm, "radius": 26.5 * mm});
            skCircle(sketch, "E1366", {"center": v(-715, -1351) * mm, "radius": 26.5 * mm});
            skCircle(sketch, "E1367", {"center": v(-97.5, -394.04) * mm, "radius": 26.5 * mm});
            skCircle(sketch, "E1368", {"center": v(-130, -450.33) * mm, "radius": 26.5 * mm});
            skCircle(sketch, "E1369", {"center": v(-162.5, -506.62) * mm, "radius": 26.5 * mm});
            skCircle(sketch, "E1370", {"center": v(-195, -562.92) * mm, "radius": 26.5 * mm});
            skCircle(sketch, "E1371", {"center": v(-227.5, -619.2) * mm, "radius": 26.5 * mm});
            skCircle(sketch, "E1372", {"center": v(-260, -675.5) * mm, "radius": 26.5 * mm});
            skCircle(sketch, "E1373", {"center": v(-292.5, -731.8) * mm, "radius": 26.5 * mm});
            skCircle(sketch, "E1374", {"center": v(-325, -788.08) * mm, "radius": 26.5 * mm});
            skCircle(sketch, "E1375", {"center": v(-357.5, -844.37) * mm, "radius": 26.5 * mm});
            skCircle(sketch, "E1376", {"center": v(-390, -900.67) * mm, "radius": 26.5 * mm});
            skCircle(sketch, "E1377", {"center": v(-422.5, -956.96) * mm, "radius": 26.5 * mm});
            skCircle(sketch, "E1378", {"center": v(-455, -1013.25) * mm, "radius": 26.5 * mm});
            skCircle(sketch, "E1379", {"center": v(-487.5, -1069.54) * mm, "radius": 26.5 * mm});
            skCircle(sketch, "E1380", {"center": v(-520, -1125.83) * mm, "radius": 26.5 * mm});
            skCircle(sketch, "E1381", {"center": v(-552.5, -1182.12) * mm, "radius": 26.5 * mm});
            skCircle(sketch, "E1382", {"center": v(-585, -1238.42) * mm, "radius": 26.5 * mm});
            skCircle(sketch, "E1383", {"center": v(-617.5, -1294.7) * mm, "radius": 26.5 * mm});
            skCircle(sketch, "E1384", {"center": v(-650, -1351) * mm, "radius": 26.5 * mm});
            skCircle(sketch, "E1385", {"center": v(-682.5, -1407.3) * mm, "radius": 26.5 * mm});
            skCircle(sketch, "E1386", {"center": v(-32.5, -394.04) * mm, "radius": 26.5 * mm});
            skCircle(sketch, "E1387", {"center": v(-65, -450.33) * mm, "radius": 26.5 * mm});
            skCircle(sketch, "E1388", {"center": v(-97.5, -506.62) * mm, "radius": 26.5 * mm});
            skCircle(sketch, "E1389", {"center": v(-130, -562.92) * mm, "radius": 26.5 * mm});
            skCircle(sketch, "E1390", {"center": v(-162.5, -619.2) * mm, "radius": 26.5 * mm});
            skCircle(sketch, "E1391", {"center": v(-195, -675.5) * mm, "radius": 26.5 * mm});
            skCircle(sketch, "E1392", {"center": v(-227.5, -731.8) * mm, "radius": 26.5 * mm});
            skCircle(sketch, "E1393", {"center": v(-260, -788.08) * mm, "radius": 26.5 * mm});
            skCircle(sketch, "E1394", {"center": v(-292.5, -844.37) * mm, "radius": 26.5 * mm});
            skCircle(sketch, "E1395", {"center": v(-325, -900.67) * mm, "radius": 26.5 * mm});
            skCircle(sketch, "E1396", {"center": v(-357.5, -956.96) * mm, "radius": 26.5 * mm});
            skCircle(sketch, "E1397", {"center": v(-390, -1013.25) * mm, "radius": 26.5 * mm});
            skCircle(sketch, "E1398", {"center": v(-422.5, -1069.54) * mm, "radius": 26.5 * mm});
            skCircle(sketch, "E1399", {"center": v(-455, -1125.83) * mm, "radius": 26.5 * mm});
            skCircle(sketch, "E1400", {"center": v(-487.5, -1182.12) * mm, "radius": 26.5 * mm});
            skCircle(sketch, "E1401", {"center": v(-520, -1238.42) * mm, "radius": 26.5 * mm});
            skCircle(sketch, "E1402", {"center": v(-552.5, -1294.7) * mm, "radius": 26.5 * mm});
            skCircle(sketch, "E1403", {"center": v(-585, -1351) * mm, "radius": 26.5 * mm});
            skCircle(sketch, "E1404", {"center": v(-617.5, -1407.3) * mm, "radius": 26.5 * mm});
            skCircle(sketch, "E1405", {"center": v(32.5, -394.04) * mm, "radius": 26.5 * mm});
            skCircle(sketch, "E1406", {"center": v(0, -450.33) * mm, "radius": 26.5 * mm});
            skCircle(sketch, "E1407", {"center": v(-32.5, -506.62) * mm, "radius": 26.5 * mm});
            skCircle(sketch, "E1408", {"center": v(-65, -562.92) * mm, "radius": 26.5 * mm});
            skCircle(sketch, "E1409", {"center": v(-97.5, -619.2) * mm, "radius": 26.5 * mm});
            skCircle(sketch, "E1410", {"center": v(-130, -675.5) * mm, "radius": 26.5 * mm});
            skCircle(sketch, "E1411", {"center": v(-162.5, -731.8) * mm, "radius": 26.5 * mm});
            skCircle(sketch, "E1412", {"center": v(-195, -788.08) * mm, "radius": 26.5 * mm});
            skCircle(sketch, "E1413", {"center": v(-227.5, -844.37) * mm, "radius": 26.5 * mm});
            skCircle(sketch, "E1414", {"center": v(-260, -900.67) * mm, "radius": 26.5 * mm});
            skCircle(sketch, "E1415", {"center": v(-292.5, -956.96) * mm, "radius": 26.5 * mm});
            skCircle(sketch, "E1416", {"center": v(-325, -1013.25) * mm, "radius": 26.5 * mm});
            skCircle(sketch, "E1417", {"center": v(-357.5, -1069.54) * mm, "radius": 26.5 * mm});
            skCircle(sketch, "E1418", {"center": v(-390, -1125.83) * mm, "radius": 26.5 * mm});
            skCircle(sketch, "E1419", {"center": v(-422.5, -1182.12) * mm, "radius": 26.5 * mm});
            skCircle(sketch, "E1420", {"center": v(-455, -1238.42) * mm, "radius": 26.5 * mm});
            skCircle(sketch, "E1421", {"center": v(-487.5, -1294.7) * mm, "radius": 26.5 * mm});
            skCircle(sketch, "E1422", {"center": v(-520, -1351) * mm, "radius": 26.5 * mm});
            skCircle(sketch, "E1423", {"center": v(-552.5, -1407.3) * mm, "radius": 26.5 * mm});
            skCircle(sketch, "E1424", {"center": v(-585, -1463.58) * mm, "radius": 26.5 * mm});
            skCircle(sketch, "E1425", {"center": v(97.5, -394.04) * mm, "radius": 26.5 * mm});
            skCircle(sketch, "E1426", {"center": v(65, -450.33) * mm, "radius": 26.5 * mm});
            skCircle(sketch, "E1427", {"center": v(32.5, -506.62) * mm, "radius": 26.5 * mm});
            skCircle(sketch, "E1428", {"center": v(0, -562.92) * mm, "radius": 26.5 * mm});
            skCircle(sketch, "E1429", {"center": v(-32.5, -619.2) * mm, "radius": 26.5 * mm});
            skCircle(sketch, "E1430", {"center": v(-65, -675.5) * mm, "radius": 26.5 * mm});
            skCircle(sketch, "E1431", {"center": v(-97.5, -731.8) * mm, "radius": 26.5 * mm});
            skCircle(sketch, "E1432", {"center": v(-130, -788.08) * mm, "radius": 26.5 * mm});
            skCircle(sketch, "E1433", {"center": v(-162.5, -844.37) * mm, "radius": 26.5 * mm});
            skCircle(sketch, "E1434", {"center": v(-195, -900.67) * mm, "radius": 26.5 * mm});
            skCircle(sketch, "E1435", {"center": v(-227.5, -956.96) * mm, "radius": 26.5 * mm});
            skCircle(sketch, "E1436", {"center": v(-260, -1013.25) * mm, "radius": 26.5 * mm});
            skCircle(sketch, "E1437", {"center": v(-292.5, -1069.54) * mm, "radius": 26.5 * mm});
            skCircle(sketch, "E1438", {"center": v(-325, -1125.83) * mm, "radius": 26.5 * mm});
            skCircle(sketch, "E1439", {"center": v(-357.5, -1182.12) * mm, "radius": 26.5 * mm});
            skCircle(sketch, "E1440", {"center": v(-390, -1238.42) * mm, "radius": 26.5 * mm});
            skCircle(sketch, "E1441", {"center": v(-422.5, -1294.7) * mm, "radius": 26.5 * mm});
            skCircle(sketch, "E1442", {"center": v(-455, -1351) * mm, "radius": 26.5 * mm});
            skCircle(sketch, "E1443", {"center": v(-487.5, -1407.3) * mm, "radius": 26.5 * mm});
            skCircle(sketch, "E1444", {"center": v(-520, -1463.58) * mm, "radius": 26.5 * mm});
            skCircle(sketch, "E1445", {"center": v(162.5, -394.04) * mm, "radius": 26.5 * mm});
            skCircle(sketch, "E1446", {"center": v(130, -450.33) * mm, "radius": 26.5 * mm});
            skCircle(sketch, "E1447", {"center": v(97.5, -506.62) * mm, "radius": 26.5 * mm});
            skCircle(sketch, "E1448", {"center": v(65, -562.92) * mm, "radius": 26.5 * mm});
            skCircle(sketch, "E1449", {"center": v(32.5, -619.2) * mm, "radius": 26.5 * mm});
            skCircle(sketch, "E1450", {"center": v(0, -675.5) * mm, "radius": 26.5 * mm});
            skCircle(sketch, "E1451", {"center": v(-32.5, -731.8) * mm, "radius": 26.5 * mm});
            skCircle(sketch, "E1452", {"center": v(-65, -788.08) * mm, "radius": 26.5 * mm});
            skCircle(sketch, "E1453", {"center": v(-97.5, -844.37) * mm, "radius": 26.5 * mm});
            skCircle(sketch, "E1454", {"center": v(-130, -900.67) * mm, "radius": 26.5 * mm});
            skCircle(sketch, "E1455", {"center": v(-162.5, -956.96) * mm, "radius": 26.5 * mm});
            skCircle(sketch, "E1456", {"center": v(-195, -1013.25) * mm, "radius": 26.5 * mm});
            skCircle(sketch, "E1457", {"center": v(-227.5, -1069.54) * mm, "radius": 26.5 * mm});
            skCircle(sketch, "E1458", {"center": v(-260, -1125.83) * mm, "radius": 26.5 * mm});
            skCircle(sketch, "E1459", {"center": v(-292.5, -1182.12) * mm, "radius": 26.5 * mm});
            skCircle(sketch, "E1460", {"center": v(-325, -1238.42) * mm, "radius": 26.5 * mm});
            skCircle(sketch, "E1461", {"center": v(-357.5, -1294.7) * mm, "radius": 26.5 * mm});
            skCircle(sketch, "E1462", {"center": v(-390, -1351) * mm, "radius": 26.5 * mm});
            skCircle(sketch, "E1463", {"center": v(-422.5, -1407.3) * mm, "radius": 26.5 * mm});
            skCircle(sketch, "E1464", {"center": v(-455, -1463.58) * mm, "radius": 26.5 * mm});
            skCircle(sketch, "E1465", {"center": v(195, -450.33) * mm, "radius": 26.5 * mm});
            skCircle(sketch, "E1466", {"center": v(162.5, -506.62) * mm, "radius": 26.5 * mm});
            skCircle(sketch, "E1467", {"center": v(130, -562.92) * mm, "radius": 26.5 * mm});
            skCircle(sketch, "E1468", {"center": v(97.5, -619.2) * mm, "radius": 26.5 * mm});
            skCircle(sketch, "E1469", {"center": v(65, -675.5) * mm, "radius": 26.5 * mm});
            skCircle(sketch, "E1470", {"center": v(32.5, -731.8) * mm, "radius": 26.5 * mm});
            skCircle(sketch, "E1471", {"center": v(0, -788.08) * mm, "radius": 26.5 * mm});
            skCircle(sketch, "E1472", {"center": v(-32.5, -844.37) * mm, "radius": 26.5 * mm});
            skCircle(sketch, "E1473", {"center": v(-65, -900.67) * mm, "radius": 26.5 * mm});
            skCircle(sketch, "E1474", {"center": v(-97.5, -956.96) * mm, "radius": 26.5 * mm});
            skCircle(sketch, "E1475", {"center": v(-130, -1013.25) * mm, "radius": 26.5 * mm});
            skCircle(sketch, "E1476", {"center": v(-162.5, -1069.54) * mm, "radius": 26.5 * mm});
            skCircle(sketch, "E1477", {"center": v(-195, -1125.83) * mm, "radius": 26.5 * mm});
            skCircle(sketch, "E1478", {"center": v(-227.5, -1182.12) * mm, "radius": 26.5 * mm});
            skCircle(sketch, "E1479", {"center": v(-260, -1238.42) * mm, "radius": 26.5 * mm});
            skCircle(sketch, "E1480", {"center": v(-292.5, -1294.7) * mm, "radius": 26.5 * mm});
            skCircle(sketch, "E1481", {"center": v(-325, -1351) * mm, "radius": 26.5 * mm});
            skCircle(sketch, "E1482", {"center": v(-357.5, -1407.3) * mm, "radius": 26.5 * mm});
            skCircle(sketch, "E1483", {"center": v(-390, -1463.58) * mm, "radius": 26.5 * mm});
            skCircle(sketch, "E1484", {"center": v(-422.5, -1519.87) * mm, "radius": 26.5 * mm});
            skCircle(sketch, "E1485", {"center": v(227.5, -506.62) * mm, "radius": 26.5 * mm});
            skCircle(sketch, "E1486", {"center": v(195, -562.92) * mm, "radius": 26.5 * mm});
            skCircle(sketch, "E1487", {"center": v(162.5, -619.2) * mm, "radius": 26.5 * mm});
            skCircle(sketch, "E1488", {"center": v(130, -675.5) * mm, "radius": 26.5 * mm});
            skCircle(sketch, "E1489", {"center": v(97.5, -731.8) * mm, "radius": 26.5 * mm});
            skCircle(sketch, "E1490", {"center": v(65, -788.08) * mm, "radius": 26.5 * mm});
            skCircle(sketch, "E1491", {"center": v(32.5, -844.37) * mm, "radius": 26.5 * mm});
            skCircle(sketch, "E1492", {"center": v(0, -900.67) * mm, "radius": 26.5 * mm});
            skCircle(sketch, "E1493", {"center": v(-32.5, -956.96) * mm, "radius": 26.5 * mm});
            skCircle(sketch, "E1494", {"center": v(-65, -1013.25) * mm, "radius": 26.5 * mm});
            skCircle(sketch, "E1495", {"center": v(-97.5, -1069.54) * mm, "radius": 26.5 * mm});
            skCircle(sketch, "E1496", {"center": v(-130, -1125.83) * mm, "radius": 26.5 * mm});
            skCircle(sketch, "E1497", {"center": v(-162.5, -1182.12) * mm, "radius": 26.5 * mm});
            skCircle(sketch, "E1498", {"center": v(-195, -1238.42) * mm, "radius": 26.5 * mm});
            skCircle(sketch, "E1499", {"center": v(-227.5, -1294.7) * mm, "radius": 26.5 * mm});
            skCircle(sketch, "E1500", {"center": v(-260, -1351) * mm, "radius": 26.5 * mm});
            skCircle(sketch, "E1501", {"center": v(-292.5, -1407.3) * mm, "radius": 26.5 * mm});
            skCircle(sketch, "E1502", {"center": v(-325, -1463.58) * mm, "radius": 26.5 * mm});
            skCircle(sketch, "E1503", {"center": v(-357.5, -1519.87) * mm, "radius": 26.5 * mm});
            skCircle(sketch, "E1504", {"center": v(260, -562.92) * mm, "radius": 26.5 * mm});
            skCircle(sketch, "E1505", {"center": v(227.5, -619.2) * mm, "radius": 26.5 * mm});
            skCircle(sketch, "E1506", {"center": v(195, -675.5) * mm, "radius": 26.5 * mm});
            skCircle(sketch, "E1507", {"center": v(162.5, -731.8) * mm, "radius": 26.5 * mm});
            skCircle(sketch, "E1508", {"center": v(130, -788.08) * mm, "radius": 26.5 * mm});
            skCircle(sketch, "E1509", {"center": v(97.5, -844.37) * mm, "radius": 26.5 * mm});
            skCircle(sketch, "E1510", {"center": v(65, -900.67) * mm, "radius": 26.5 * mm});
            skCircle(sketch, "E1511", {"center": v(32.5, -956.96) * mm, "radius": 26.5 * mm});
            skCircle(sketch, "E1512", {"center": v(0, -1013.25) * mm, "radius": 26.5 * mm});
            skCircle(sketch, "E1513", {"center": v(-97.5, -1182.12) * mm, "radius": 26.5 * mm});
            skCircle(sketch, "E1514", {"center": v(-130, -1238.42) * mm, "radius": 26.5 * mm});
            skCircle(sketch, "E1515", {"center": v(-162.5, -1294.7) * mm, "radius": 26.5 * mm});
            skCircle(sketch, "E1516", {"center": v(-195, -1351) * mm, "radius": 26.5 * mm});
            skCircle(sketch, "E1517", {"center": v(-227.5, -1407.3) * mm, "radius": 26.5 * mm});
            skCircle(sketch, "E1518", {"center": v(-260, -1463.58) * mm, "radius": 26.5 * mm});
            skCircle(sketch, "E1519", {"center": v(-292.5, -1519.87) * mm, "radius": 26.5 * mm});
            skCircle(sketch, "E1520", {"center": v(292.5, -619.2) * mm, "radius": 26.5 * mm});
            skCircle(sketch, "E1521", {"center": v(260, -675.5) * mm, "radius": 26.5 * mm});
            skCircle(sketch, "E1522", {"center": v(227.5, -731.8) * mm, "radius": 26.5 * mm});
            skCircle(sketch, "E1523", {"center": v(195, -788.08) * mm, "radius": 26.5 * mm});
            skCircle(sketch, "E1524", {"center": v(162.5, -844.37) * mm, "radius": 26.5 * mm});
            skCircle(sketch, "E1525", {"center": v(130, -900.67) * mm, "radius": 26.5 * mm});
            skCircle(sketch, "E1526", {"center": v(97.5, -956.96) * mm, "radius": 26.5 * mm});
            skCircle(sketch, "E1527", {"center": v(65, -1013.25) * mm, "radius": 26.5 * mm});
            skCircle(sketch, "E1528", {"center": v(-65, -1238.42) * mm, "radius": 26.5 * mm});
            skCircle(sketch, "E1529", {"center": v(-97.5, -1294.7) * mm, "radius": 26.5 * mm});
            skCircle(sketch, "E1530", {"center": v(-130, -1351) * mm, "radius": 26.5 * mm});
            skCircle(sketch, "E1531", {"center": v(-162.5, -1407.3) * mm, "radius": 26.5 * mm});
            skCircle(sketch, "E1532", {"center": v(-195, -1463.58) * mm, "radius": 26.5 * mm});
            skCircle(sketch, "E1533", {"center": v(-227.5, -1519.87) * mm, "radius": 26.5 * mm});
            skCircle(sketch, "E1534", {"center": v(325, -675.5) * mm, "radius": 26.5 * mm});
            skCircle(sketch, "E1535", {"center": v(292.5, -731.8) * mm, "radius": 26.5 * mm});
            skCircle(sketch, "E1536", {"center": v(260, -788.08) * mm, "radius": 26.5 * mm});
            skCircle(sketch, "E1537", {"center": v(227.5, -844.37) * mm, "radius": 26.5 * mm});
            skCircle(sketch, "E1538", {"center": v(195, -900.67) * mm, "radius": 26.5 * mm});
            skCircle(sketch, "E1539", {"center": v(162.5, -956.96) * mm, "radius": 26.5 * mm});
            skCircle(sketch, "E1540", {"center": v(130, -1013.25) * mm, "radius": 26.5 * mm});
            skCircle(sketch, "E1541", {"center": v(97.5, -1069.54) * mm, "radius": 26.5 * mm});
            skCircle(sketch, "E1542", {"center": v(0, -1238.42) * mm, "radius": 26.5 * mm});
            skCircle(sketch, "E1543", {"center": v(-32.5, -1294.7) * mm, "radius": 26.5 * mm});
            skCircle(sketch, "E1544", {"center": v(-65, -1351) * mm, "radius": 26.5 * mm});
            skCircle(sketch, "E1545", {"center": v(-97.5, -1407.3) * mm, "radius": 26.5 * mm});
            skCircle(sketch, "E1546", {"center": v(-130, -1463.58) * mm, "radius": 26.5 * mm});
            skCircle(sketch, "E1547", {"center": v(-162.5, -1519.87) * mm, "radius": 26.5 * mm});
            skCircle(sketch, "E1548", {"center": v(357.5, -731.8) * mm, "radius": 26.5 * mm});
            skCircle(sketch, "E1549", {"center": v(325, -788.08) * mm, "radius": 26.5 * mm});
            skCircle(sketch, "E1550", {"center": v(292.5, -844.37) * mm, "radius": 26.5 * mm});
            skCircle(sketch, "E1551", {"center": v(260, -900.67) * mm, "radius": 26.5 * mm});
            skCircle(sketch, "E1552", {"center": v(227.5, -956.96) * mm, "radius": 26.5 * mm});
            skCircle(sketch, "E1553", {"center": v(195, -1013.25) * mm, "radius": 26.5 * mm});
            skCircle(sketch, "E1554", {"center": v(162.5, -1069.54) * mm, "radius": 26.5 * mm});
            skCircle(sketch, "E1555", {"center": v(130, -1125.83) * mm, "radius": 26.5 * mm});
            skCircle(sketch, "E1556", {"center": v(97.5, -1182.12) * mm, "radius": 26.5 * mm});
            skCircle(sketch, "E1557", {"center": v(65, -1238.42) * mm, "radius": 26.5 * mm});
            skCircle(sketch, "E1558", {"center": v(32.5, -1294.7) * mm, "radius": 26.5 * mm});
            skCircle(sketch, "E1559", {"center": v(0, -1351) * mm, "radius": 26.5 * mm});
            skCircle(sketch, "E1560", {"center": v(-32.5, -1407.3) * mm, "radius": 26.5 * mm});
            skCircle(sketch, "E1561", {"center": v(-65, -1463.58) * mm, "radius": 26.5 * mm});
            skCircle(sketch, "E1562", {"center": v(-97.5, -1519.87) * mm, "radius": 26.5 * mm});
            skCircle(sketch, "E1563", {"center": v(390, -788.08) * mm, "radius": 26.5 * mm});
            skCircle(sketch, "E1564", {"center": v(357.5, -844.37) * mm, "radius": 26.5 * mm});
            skCircle(sketch, "E1565", {"center": v(325, -900.67) * mm, "radius": 26.5 * mm});
            skCircle(sketch, "E1566", {"center": v(292.5, -956.96) * mm, "radius": 26.5 * mm});
            skCircle(sketch, "E1567", {"center": v(260, -1013.25) * mm, "radius": 26.5 * mm});
            skCircle(sketch, "E1568", {"center": v(227.5, -1069.54) * mm, "radius": 26.5 * mm});
            skCircle(sketch, "E1569", {"center": v(195, -1125.83) * mm, "radius": 26.5 * mm});
            skCircle(sketch, "E1570", {"center": v(162.5, -1182.12) * mm, "radius": 26.5 * mm});
            skCircle(sketch, "E1571", {"center": v(130, -1238.42) * mm, "radius": 26.5 * mm});
            skCircle(sketch, "E1572", {"center": v(97.5, -1294.7) * mm, "radius": 26.5 * mm});
            skCircle(sketch, "E1573", {"center": v(65, -1351) * mm, "radius": 26.5 * mm});
            skCircle(sketch, "E1574", {"center": v(32.5, -1407.3) * mm, "radius": 26.5 * mm});
            skCircle(sketch, "E1575", {"center": v(0, -1463.58) * mm, "radius": 26.5 * mm});
            skCircle(sketch, "E1576", {"center": v(-32.5, -1519.87) * mm, "radius": 26.5 * mm});
            skCircle(sketch, "E1577", {"center": v(-65, -1576.17) * mm, "radius": 26.5 * mm});
            skCircle(sketch, "E1578", {"center": v(422.5, -844.37) * mm, "radius": 26.5 * mm});
            skCircle(sketch, "E1579", {"center": v(390, -900.67) * mm, "radius": 26.5 * mm});
            skCircle(sketch, "E1580", {"center": v(357.5, -956.96) * mm, "radius": 26.5 * mm});
            skCircle(sketch, "E1581", {"center": v(325, -1013.25) * mm, "radius": 26.5 * mm});
            skCircle(sketch, "E1582", {"center": v(292.5, -1069.54) * mm, "radius": 26.5 * mm});
            skCircle(sketch, "E1583", {"center": v(260, -1125.83) * mm, "radius": 26.5 * mm});
            skCircle(sketch, "E1584", {"center": v(227.5, -1182.12) * mm, "radius": 26.5 * mm});
            skCircle(sketch, "E1585", {"center": v(195, -1238.42) * mm, "radius": 26.5 * mm});
            skCircle(sketch, "E1586", {"center": v(162.5, -1294.7) * mm, "radius": 26.5 * mm});
            skCircle(sketch, "E1587", {"center": v(130, -1351) * mm, "radius": 26.5 * mm});
            skCircle(sketch, "E1588", {"center": v(97.5, -1407.3) * mm, "radius": 26.5 * mm});
            skCircle(sketch, "E1589", {"center": v(65, -1463.58) * mm, "radius": 26.5 * mm});
            skCircle(sketch, "E1590", {"center": v(32.5, -1519.87) * mm, "radius": 26.5 * mm});
            skCircle(sketch, "E1591", {"center": v(0, -1576.17) * mm, "radius": 26.5 * mm});
            skCircle(sketch, "E1592", {"center": v(455, -900.67) * mm, "radius": 26.5 * mm});
            skCircle(sketch, "E1593", {"center": v(422.5, -956.96) * mm, "radius": 26.5 * mm});
            skCircle(sketch, "E1594", {"center": v(390, -1013.25) * mm, "radius": 26.5 * mm});
            skCircle(sketch, "E1595", {"center": v(357.5, -1069.54) * mm, "radius": 26.5 * mm});
            skCircle(sketch, "E1596", {"center": v(325, -1125.83) * mm, "radius": 26.5 * mm});
            skCircle(sketch, "E1597", {"center": v(292.5, -1182.12) * mm, "radius": 26.5 * mm});
            skCircle(sketch, "E1598", {"center": v(260, -1238.42) * mm, "radius": 26.5 * mm});
            skCircle(sketch, "E1599", {"center": v(227.5, -1294.7) * mm, "radius": 26.5 * mm});
            skCircle(sketch, "E1600", {"center": v(195, -1351) * mm, "radius": 26.5 * mm});
            skCircle(sketch, "E1601", {"center": v(162.5, -1407.3) * mm, "radius": 26.5 * mm});
            skCircle(sketch, "E1602", {"center": v(130, -1463.58) * mm, "radius": 26.5 * mm});
            skCircle(sketch, "E1603", {"center": v(97.5, -1519.87) * mm, "radius": 26.5 * mm});
            skCircle(sketch, "E1604", {"center": v(65, -1576.17) * mm, "radius": 26.5 * mm});
            skCircle(sketch, "E1605", {"center": v(487.5, -956.96) * mm, "radius": 26.5 * mm});
            skCircle(sketch, "E1606", {"center": v(455, -1013.25) * mm, "radius": 26.5 * mm});
            skCircle(sketch, "E1607", {"center": v(422.5, -1069.54) * mm, "radius": 26.5 * mm});
            skCircle(sketch, "E1608", {"center": v(390, -1125.83) * mm, "radius": 26.5 * mm});
            skCircle(sketch, "E1609", {"center": v(357.5, -1182.12) * mm, "radius": 26.5 * mm});
            skCircle(sketch, "E1610", {"center": v(325, -1238.42) * mm, "radius": 26.5 * mm});
            skCircle(sketch, "E1611", {"center": v(292.5, -1294.7) * mm, "radius": 26.5 * mm});
            skCircle(sketch, "E1612", {"center": v(260, -1351) * mm, "radius": 26.5 * mm});
            skCircle(sketch, "E1613", {"center": v(227.5, -1407.3) * mm, "radius": 26.5 * mm});
            skCircle(sketch, "E1614", {"center": v(195, -1463.58) * mm, "radius": 26.5 * mm});
            skCircle(sketch, "E1615", {"center": v(162.5, -1519.87) * mm, "radius": 26.5 * mm});
            skCircle(sketch, "E1616", {"center": v(520, -1013.25) * mm, "radius": 26.5 * mm});
            skCircle(sketch, "E1617", {"center": v(487.5, -1069.54) * mm, "radius": 26.5 * mm});
            skCircle(sketch, "E1618", {"center": v(455, -1125.83) * mm, "radius": 26.5 * mm});
            skCircle(sketch, "E1619", {"center": v(422.5, -1182.12) * mm, "radius": 26.5 * mm});
            skCircle(sketch, "E1620", {"center": v(390, -1238.42) * mm, "radius": 26.5 * mm});
            skCircle(sketch, "E1621", {"center": v(357.5, -1294.7) * mm, "radius": 26.5 * mm});
            skCircle(sketch, "E1622", {"center": v(325, -1351) * mm, "radius": 26.5 * mm});
            skCircle(sketch, "E1623", {"center": v(292.5, -1407.3) * mm, "radius": 26.5 * mm});
            skCircle(sketch, "E1624", {"center": v(260, -1463.58) * mm, "radius": 26.5 * mm});
            skCircle(sketch, "E1625", {"center": v(227.5, -1519.87) * mm, "radius": 26.5 * mm});
            skCircle(sketch, "E1626", {"center": v(552.5, -1069.54) * mm, "radius": 26.5 * mm});
            skCircle(sketch, "E1627", {"center": v(520, -1125.83) * mm, "radius": 26.5 * mm});
            skCircle(sketch, "E1628", {"center": v(487.5, -1182.12) * mm, "radius": 26.5 * mm});
            skCircle(sketch, "E1629", {"center": v(455, -1238.42) * mm, "radius": 26.5 * mm});
            skCircle(sketch, "E1630", {"center": v(422.5, -1294.7) * mm, "radius": 26.5 * mm});
            skCircle(sketch, "E1631", {"center": v(390, -1351) * mm, "radius": 26.5 * mm});
            skCircle(sketch, "E1632", {"center": v(357.5, -1407.3) * mm, "radius": 26.5 * mm});
            skCircle(sketch, "E1633", {"center": v(325, -1463.58) * mm, "radius": 26.5 * mm});
            skCircle(sketch, "E1634", {"center": v(292.5, -1519.87) * mm, "radius": 26.5 * mm});
            skCircle(sketch, "E1635", {"center": v(585, -1125.83) * mm, "radius": 26.5 * mm});
            skCircle(sketch, "E1636", {"center": v(552.5, -1182.12) * mm, "radius": 26.5 * mm});
            skCircle(sketch, "E1637", {"center": v(520, -1238.42) * mm, "radius": 26.5 * mm});
            skCircle(sketch, "E1638", {"center": v(487.5, -1294.7) * mm, "radius": 26.5 * mm});
            skCircle(sketch, "E1639", {"center": v(455, -1351) * mm, "radius": 26.5 * mm});
            skCircle(sketch, "E1640", {"center": v(422.5, -1407.3) * mm, "radius": 26.5 * mm});
            skCircle(sketch, "E1641", {"center": v(390, -1463.58) * mm, "radius": 26.5 * mm});
            skCircle(sketch, "E1642", {"center": v(357.5, -1519.87) * mm, "radius": 26.5 * mm});
            skCircle(sketch, "E1643", {"center": v(617.5, -1182.12) * mm, "radius": 26.5 * mm});
            skCircle(sketch, "E1644", {"center": v(585, -1238.42) * mm, "radius": 26.5 * mm});
            skCircle(sketch, "E1645", {"center": v(552.5, -1294.7) * mm, "radius": 26.5 * mm});
            skCircle(sketch, "E1646", {"center": v(520, -1351) * mm, "radius": 26.5 * mm});
            skCircle(sketch, "E1647", {"center": v(487.5, -1407.3) * mm, "radius": 26.5 * mm});
            skCircle(sketch, "E1648", {"center": v(455, -1463.58) * mm, "radius": 26.5 * mm});
            skCircle(sketch, "E1649", {"center": v(422.5, -1519.87) * mm, "radius": 26.5 * mm});
            skCircle(sketch, "E1650", {"center": v(650, -1238.42) * mm, "radius": 26.5 * mm});
            skCircle(sketch, "E1651", {"center": v(617.5, -1294.7) * mm, "radius": 26.5 * mm});
            skCircle(sketch, "E1652", {"center": v(585, -1351) * mm, "radius": 26.5 * mm});
            skCircle(sketch, "E1653", {"center": v(552.5, -1407.3) * mm, "radius": 26.5 * mm});
            skCircle(sketch, "E1654", {"center": v(520, -1463.58) * mm, "radius": 26.5 * mm});
            skCircle(sketch, "E1655", {"center": v(682.5, -1294.7) * mm, "radius": 26.5 * mm});
            skCircle(sketch, "E1656", {"center": v(650, -1351) * mm, "radius": 26.5 * mm});
            skCircle(sketch, "E1657", {"center": v(617.5, -1407.3) * mm, "radius": 26.5 * mm});
            skCircle(sketch, "E1658", {"center": v(585, -1463.58) * mm, "radius": 26.5 * mm});
            skCircle(sketch, "E1659", {"center": v(715, -1351) * mm, "radius": 26.5 * mm});
            skCircle(sketch, "E1660", {"center": v(682.5, -1407.3) * mm, "radius": 26.5 * mm});
            skCircle(sketch, "E1661", {"center": v(0, -1125.83) * mm, "radius": 58 * mm});
            skCircle(sketch, "E1662", {"center": v(195, -337.75) * mm, "radius": 26.5 * mm});
            skCircle(sketch, "E1663", {"center": v(227.5, -394.04) * mm, "radius": 26.5 * mm});
            skCircle(sketch, "E1664", {"center": v(260, -450.33) * mm, "radius": 26.5 * mm});
            skCircle(sketch, "E1665", {"center": v(292.5, -506.62) * mm, "radius": 26.5 * mm});
            skCircle(sketch, "E1666", {"center": v(325, -562.92) * mm, "radius": 26.5 * mm});
            skCircle(sketch, "E1667", {"center": v(357.5, -619.2) * mm, "radius": 26.5 * mm});
            skCircle(sketch, "E1668", {"center": v(390, -675.5) * mm, "radius": 26.5 * mm});
            skCircle(sketch, "E1669", {"center": v(422.5, -731.8) * mm, "radius": 26.5 * mm});
            skCircle(sketch, "E1670", {"center": v(455, -788.08) * mm, "radius": 26.5 * mm});
            skCircle(sketch, "E1671", {"center": v(487.5, -844.37) * mm, "radius": 26.5 * mm});
            skCircle(sketch, "E1672", {"center": v(520, -900.67) * mm, "radius": 26.5 * mm});
            skCircle(sketch, "E1673", {"center": v(552.5, -956.96) * mm, "radius": 26.5 * mm});
            skCircle(sketch, "E1674", {"center": v(585, -1013.25) * mm, "radius": 26.5 * mm});
            skCircle(sketch, "E1675", {"center": v(617.5, -1069.54) * mm, "radius": 26.5 * mm});
            skCircle(sketch, "E1676", {"center": v(650, -1125.83) * mm, "radius": 26.5 * mm});
            skCircle(sketch, "E1677", {"center": v(682.5, -1182.12) * mm, "radius": 26.5 * mm});
            skCircle(sketch, "E1678", {"center": v(715, -1238.42) * mm, "radius": 26.5 * mm});
            skCircle(sketch, "E1679", {"center": v(747.5, -1294.7) * mm, "radius": 26.5 * mm});
            skCircle(sketch, "E1680", {"center": v(780, -1351) * mm, "radius": 26.5 * mm});
            skCircle(sketch, "E1681", {"center": v(260, -337.75) * mm, "radius": 26.5 * mm});
            skCircle(sketch, "E1682", {"center": v(292.5, -394.04) * mm, "radius": 26.5 * mm});
            skCircle(sketch, "E1683", {"center": v(325, -450.33) * mm, "radius": 26.5 * mm});
            skCircle(sketch, "E1684", {"center": v(357.5, -506.62) * mm, "radius": 26.5 * mm});
            skCircle(sketch, "E1685", {"center": v(390, -562.92) * mm, "radius": 26.5 * mm});
            skCircle(sketch, "E1686", {"center": v(422.5, -619.2) * mm, "radius": 26.5 * mm});
            skCircle(sketch, "E1687", {"center": v(455, -675.5) * mm, "radius": 26.5 * mm});
            skCircle(sketch, "E1688", {"center": v(487.5, -731.8) * mm, "radius": 26.5 * mm});
            skCircle(sketch, "E1689", {"center": v(520, -788.08) * mm, "radius": 26.5 * mm});
            skCircle(sketch, "E1690", {"center": v(552.5, -844.37) * mm, "radius": 26.5 * mm});
            skCircle(sketch, "E1691", {"center": v(585, -900.67) * mm, "radius": 26.5 * mm});
            skCircle(sketch, "E1692", {"center": v(617.5, -956.96) * mm, "radius": 26.5 * mm});
            skCircle(sketch, "E1693", {"center": v(650, -1013.25) * mm, "radius": 26.5 * mm});
            skCircle(sketch, "E1694", {"center": v(682.5, -1069.54) * mm, "radius": 26.5 * mm});
            skCircle(sketch, "E1695", {"center": v(715, -1125.83) * mm, "radius": 26.5 * mm});
            skCircle(sketch, "E1696", {"center": v(747.5, -1182.12) * mm, "radius": 26.5 * mm});
            skCircle(sketch, "E1697", {"center": v(780, -1238.42) * mm, "radius": 26.5 * mm});
            skCircle(sketch, "E1698", {"center": v(812.5, -1294.7) * mm, "radius": 26.5 * mm});
            skCircle(sketch, "E1699", {"center": v(292.5, -281.46) * mm, "radius": 26.5 * mm});
            skCircle(sketch, "E1700", {"center": v(325, -337.75) * mm, "radius": 26.5 * mm});
            skCircle(sketch, "E1701", {"center": v(357.5, -394.04) * mm, "radius": 26.5 * mm});
            skCircle(sketch, "E1702", {"center": v(390, -450.33) * mm, "radius": 26.5 * mm});
            skCircle(sketch, "E1703", {"center": v(422.5, -506.62) * mm, "radius": 26.5 * mm});
            skCircle(sketch, "E1704", {"center": v(455, -562.92) * mm, "radius": 26.5 * mm});
            skCircle(sketch, "E1705", {"center": v(487.5, -619.2) * mm, "radius": 26.5 * mm});
            skCircle(sketch, "E1706", {"center": v(520, -675.5) * mm, "radius": 26.5 * mm});
            skCircle(sketch, "E1707", {"center": v(552.5, -731.8) * mm, "radius": 26.5 * mm});
            skCircle(sketch, "E1708", {"center": v(585, -788.08) * mm, "radius": 26.5 * mm});
            skCircle(sketch, "E1709", {"center": v(617.5, -844.37) * mm, "radius": 26.5 * mm});
            skCircle(sketch, "E1710", {"center": v(650, -900.67) * mm, "radius": 26.5 * mm});
            skCircle(sketch, "E1711", {"center": v(682.5, -956.96) * mm, "radius": 26.5 * mm});
            skCircle(sketch, "E1712", {"center": v(715, -1013.25) * mm, "radius": 26.5 * mm});
            skCircle(sketch, "E1713", {"center": v(747.5, -1069.54) * mm, "radius": 26.5 * mm});
            skCircle(sketch, "E1714", {"center": v(780, -1125.83) * mm, "radius": 26.5 * mm});
            skCircle(sketch, "E1715", {"center": v(812.5, -1182.12) * mm, "radius": 26.5 * mm});
            skCircle(sketch, "E1716", {"center": v(845, -1238.42) * mm, "radius": 26.5 * mm});
            skCircle(sketch, "E1717", {"center": v(877.5, -1294.7) * mm, "radius": 26.5 * mm});
            skCircle(sketch, "E1718", {"center": v(325, -225.17) * mm, "radius": 26.5 * mm});
            skCircle(sketch, "E1719", {"center": v(357.5, -281.46) * mm, "radius": 26.5 * mm});
            skCircle(sketch, "E1720", {"center": v(390, -337.75) * mm, "radius": 26.5 * mm});
            skCircle(sketch, "E1721", {"center": v(422.5, -394.04) * mm, "radius": 26.5 * mm});
            skCircle(sketch, "E1722", {"center": v(455, -450.33) * mm, "radius": 26.5 * mm});
            skCircle(sketch, "E1723", {"center": v(487.5, -506.62) * mm, "radius": 26.5 * mm});
            skCircle(sketch, "E1724", {"center": v(520, -562.92) * mm, "radius": 26.5 * mm});
            skCircle(sketch, "E1725", {"center": v(552.5, -619.2) * mm, "radius": 26.5 * mm});
            skCircle(sketch, "E1726", {"center": v(585, -675.5) * mm, "radius": 26.5 * mm});
            skCircle(sketch, "E1727", {"center": v(617.5, -731.8) * mm, "radius": 26.5 * mm});
            skCircle(sketch, "E1728", {"center": v(650, -788.08) * mm, "radius": 26.5 * mm});
            skCircle(sketch, "E1729", {"center": v(682.5, -844.37) * mm, "radius": 26.5 * mm});
            skCircle(sketch, "E1730", {"center": v(715, -900.67) * mm, "radius": 26.5 * mm});
            skCircle(sketch, "E1731", {"center": v(747.5, -956.96) * mm, "radius": 26.5 * mm});
            skCircle(sketch, "E1732", {"center": v(780, -1013.25) * mm, "radius": 26.5 * mm});
            skCircle(sketch, "E1733", {"center": v(812.5, -1069.54) * mm, "radius": 26.5 * mm});
            skCircle(sketch, "E1734", {"center": v(845, -1125.83) * mm, "radius": 26.5 * mm});
            skCircle(sketch, "E1735", {"center": v(877.5, -1182.12) * mm, "radius": 26.5 * mm});
            skCircle(sketch, "E1736", {"center": v(910, -1238.42) * mm, "radius": 26.5 * mm});
            skCircle(sketch, "E1737", {"center": v(357.5, -168.87) * mm, "radius": 26.5 * mm});
            skCircle(sketch, "E1738", {"center": v(390, -225.17) * mm, "radius": 26.5 * mm});
            skCircle(sketch, "E1739", {"center": v(422.5, -281.46) * mm, "radius": 26.5 * mm});
            skCircle(sketch, "E1740", {"center": v(455, -337.75) * mm, "radius": 26.5 * mm});
            skCircle(sketch, "E1741", {"center": v(487.5, -394.04) * mm, "radius": 26.5 * mm});
            skCircle(sketch, "E1742", {"center": v(520, -450.33) * mm, "radius": 26.5 * mm});
            skCircle(sketch, "E1743", {"center": v(552.5, -506.62) * mm, "radius": 26.5 * mm});
            skCircle(sketch, "E1744", {"center": v(585, -562.92) * mm, "radius": 26.5 * mm});
            skCircle(sketch, "E1745", {"center": v(617.5, -619.2) * mm, "radius": 26.5 * mm});
            skCircle(sketch, "E1746", {"center": v(650, -675.5) * mm, "radius": 26.5 * mm});
            skCircle(sketch, "E1747", {"center": v(682.5, -731.8) * mm, "radius": 26.5 * mm});
            skCircle(sketch, "E1748", {"center": v(715, -788.08) * mm, "radius": 26.5 * mm});
            skCircle(sketch, "E1749", {"center": v(747.5, -844.37) * mm, "radius": 26.5 * mm});
            skCircle(sketch, "E1750", {"center": v(780, -900.67) * mm, "radius": 26.5 * mm});
            skCircle(sketch, "E1751", {"center": v(812.5, -956.96) * mm, "radius": 26.5 * mm});
            skCircle(sketch, "E1752", {"center": v(845, -1013.25) * mm, "radius": 26.5 * mm});
            skCircle(sketch, "E1753", {"center": v(877.5, -1069.54) * mm, "radius": 26.5 * mm});
            skCircle(sketch, "E1754", {"center": v(910, -1125.83) * mm, "radius": 26.5 * mm});
            skCircle(sketch, "E1755", {"center": v(942.5, -1182.12) * mm, "radius": 26.5 * mm});
            skCircle(sketch, "E1756", {"center": v(975, -1238.42) * mm, "radius": 26.5 * mm});
            skCircle(sketch, "E1757", {"center": v(390, -112.58) * mm, "radius": 26.5 * mm});
            skCircle(sketch, "E1758", {"center": v(422.5, -168.87) * mm, "radius": 26.5 * mm});
            skCircle(sketch, "E1759", {"center": v(455, -225.17) * mm, "radius": 26.5 * mm});
            skCircle(sketch, "E1760", {"center": v(487.5, -281.46) * mm, "radius": 26.5 * mm});
            skCircle(sketch, "E1761", {"center": v(520, -337.75) * mm, "radius": 26.5 * mm});
            skCircle(sketch, "E1762", {"center": v(552.5, -394.04) * mm, "radius": 26.5 * mm});
            skCircle(sketch, "E1763", {"center": v(585, -450.33) * mm, "radius": 26.5 * mm});
            skCircle(sketch, "E1764", {"center": v(617.5, -506.62) * mm, "radius": 26.5 * mm});
            skCircle(sketch, "E1765", {"center": v(650, -562.92) * mm, "radius": 26.5 * mm});
            skCircle(sketch, "E1766", {"center": v(682.5, -619.2) * mm, "radius": 26.5 * mm});
            skCircle(sketch, "E1767", {"center": v(715, -675.5) * mm, "radius": 26.5 * mm});
            skCircle(sketch, "E1768", {"center": v(747.5, -731.8) * mm, "radius": 26.5 * mm});
            skCircle(sketch, "E1769", {"center": v(780, -788.08) * mm, "radius": 26.5 * mm});
            skCircle(sketch, "E1770", {"center": v(812.5, -844.37) * mm, "radius": 26.5 * mm});
            skCircle(sketch, "E1771", {"center": v(845, -900.67) * mm, "radius": 26.5 * mm});
            skCircle(sketch, "E1772", {"center": v(877.5, -956.96) * mm, "radius": 26.5 * mm});
            skCircle(sketch, "E1773", {"center": v(910, -1013.25) * mm, "radius": 26.5 * mm});
            skCircle(sketch, "E1774", {"center": v(942.5, -1069.54) * mm, "radius": 26.5 * mm});
            skCircle(sketch, "E1775", {"center": v(975, -1125.83) * mm, "radius": 26.5 * mm});
            skCircle(sketch, "E1776", {"center": v(1007.5, -1182.12) * mm, "radius": 26.5 * mm});
            skCircle(sketch, "E1777", {"center": v(422.5, -56.3) * mm, "radius": 26.5 * mm});
            skCircle(sketch, "E1778", {"center": v(455, -112.58) * mm, "radius": 26.5 * mm});
            skCircle(sketch, "E1779", {"center": v(487.5, -168.87) * mm, "radius": 26.5 * mm});
            skCircle(sketch, "E1780", {"center": v(520, -225.17) * mm, "radius": 26.5 * mm});
            skCircle(sketch, "E1781", {"center": v(552.5, -281.46) * mm, "radius": 26.5 * mm});
            skCircle(sketch, "E1782", {"center": v(585, -337.75) * mm, "radius": 26.5 * mm});
            skCircle(sketch, "E1783", {"center": v(617.5, -394.04) * mm, "radius": 26.5 * mm});
            skCircle(sketch, "E1784", {"center": v(650, -450.33) * mm, "radius": 26.5 * mm});
            skCircle(sketch, "E1785", {"center": v(682.5, -506.62) * mm, "radius": 26.5 * mm});
            skCircle(sketch, "E1786", {"center": v(715, -562.92) * mm, "radius": 26.5 * mm});
            skCircle(sketch, "E1787", {"center": v(747.5, -619.2) * mm, "radius": 26.5 * mm});
            skCircle(sketch, "E1788", {"center": v(780, -675.5) * mm, "radius": 26.5 * mm});
            skCircle(sketch, "E1789", {"center": v(812.5, -731.8) * mm, "radius": 26.5 * mm});
            skCircle(sketch, "E1790", {"center": v(845, -788.08) * mm, "radius": 26.5 * mm});
            skCircle(sketch, "E1791", {"center": v(877.5, -844.37) * mm, "radius": 26.5 * mm});
            skCircle(sketch, "E1792", {"center": v(910, -900.67) * mm, "radius": 26.5 * mm});
            skCircle(sketch, "E1793", {"center": v(942.5, -956.96) * mm, "radius": 26.5 * mm});
            skCircle(sketch, "E1794", {"center": v(975, -1013.25) * mm, "radius": 26.5 * mm});
            skCircle(sketch, "E1795", {"center": v(1007.5, -1069.54) * mm, "radius": 26.5 * mm});
            skCircle(sketch, "E1796", {"center": v(1040, -1125.83) * mm, "radius": 26.5 * mm});
            skCircle(sketch, "E1797", {"center": v(487.5, -56.3) * mm, "radius": 26.5 * mm});
            skCircle(sketch, "E1798", {"center": v(520, -112.58) * mm, "radius": 26.5 * mm});
            skCircle(sketch, "E1799", {"center": v(552.5, -168.87) * mm, "radius": 26.5 * mm});
            skCircle(sketch, "E1800", {"center": v(585, -225.17) * mm, "radius": 26.5 * mm});
            skCircle(sketch, "E1801", {"center": v(617.5, -281.46) * mm, "radius": 26.5 * mm});
            skCircle(sketch, "E1802", {"center": v(650, -337.75) * mm, "radius": 26.5 * mm});
            skCircle(sketch, "E1803", {"center": v(682.5, -394.04) * mm, "radius": 26.5 * mm});
            skCircle(sketch, "E1804", {"center": v(715, -450.33) * mm, "radius": 26.5 * mm});
            skCircle(sketch, "E1805", {"center": v(747.5, -506.62) * mm, "radius": 26.5 * mm});
            skCircle(sketch, "E1806", {"center": v(780, -562.92) * mm, "radius": 26.5 * mm});
            skCircle(sketch, "E1807", {"center": v(812.5, -619.2) * mm, "radius": 26.5 * mm});
            skCircle(sketch, "E1808", {"center": v(845, -675.5) * mm, "radius": 26.5 * mm});
            skCircle(sketch, "E1809", {"center": v(877.5, -731.8) * mm, "radius": 26.5 * mm});
            skCircle(sketch, "E1810", {"center": v(910, -788.08) * mm, "radius": 26.5 * mm});
            skCircle(sketch, "E1811", {"center": v(942.5, -844.37) * mm, "radius": 26.5 * mm});
            skCircle(sketch, "E1812", {"center": v(975, -900.67) * mm, "radius": 26.5 * mm});
            skCircle(sketch, "E1813", {"center": v(1007.5, -956.96) * mm, "radius": 26.5 * mm});
            skCircle(sketch, "E1814", {"center": v(1040, -1013.25) * mm, "radius": 26.5 * mm});
            skCircle(sketch, "E1815", {"center": v(1072.5, -1069.54) * mm, "radius": 26.5 * mm});
            skCircle(sketch, "E1816", {"center": v(1105, -1125.83) * mm, "radius": 26.5 * mm});
            skCircle(sketch, "E1817", {"center": v(552.5, -56.3) * mm, "radius": 26.5 * mm});
            skCircle(sketch, "E1818", {"center": v(585, -112.58) * mm, "radius": 26.5 * mm});
            skCircle(sketch, "E1819", {"center": v(617.5, -168.87) * mm, "radius": 26.5 * mm});
            skCircle(sketch, "E1820", {"center": v(650, -225.17) * mm, "radius": 26.5 * mm});
            skCircle(sketch, "E1821", {"center": v(682.5, -281.46) * mm, "radius": 26.5 * mm});
            skCircle(sketch, "E1822", {"center": v(715, -337.75) * mm, "radius": 26.5 * mm});
            skCircle(sketch, "E1823", {"center": v(747.5, -394.04) * mm, "radius": 26.5 * mm});
            skCircle(sketch, "E1824", {"center": v(780, -450.33) * mm, "radius": 26.5 * mm});
            skCircle(sketch, "E1825", {"center": v(812.5, -506.62) * mm, "radius": 26.5 * mm});
            skCircle(sketch, "E1826", {"center": v(845, -562.92) * mm, "radius": 26.5 * mm});
            skCircle(sketch, "E1827", {"center": v(877.5, -619.2) * mm, "radius": 26.5 * mm});
            skCircle(sketch, "E1828", {"center": v(910, -675.5) * mm, "radius": 26.5 * mm});
            skCircle(sketch, "E1829", {"center": v(942.5, -731.8) * mm, "radius": 26.5 * mm});
            skCircle(sketch, "E1830", {"center": v(975, -788.08) * mm, "radius": 26.5 * mm});
            skCircle(sketch, "E1831", {"center": v(1007.5, -844.37) * mm, "radius": 26.5 * mm});
            skCircle(sketch, "E1832", {"center": v(1040, -900.67) * mm, "radius": 26.5 * mm});
            skCircle(sketch, "E1833", {"center": v(1072.5, -956.96) * mm, "radius": 26.5 * mm});
            skCircle(sketch, "E1834", {"center": v(1105, -1013.25) * mm, "radius": 26.5 * mm});
            skCircle(sketch, "E1835", {"center": v(1137.5, -1069.54) * mm, "radius": 26.5 * mm});
            skCircle(sketch, "E1836", {"center": v(617.5, -56.3) * mm, "radius": 26.5 * mm});
            skCircle(sketch, "E1837", {"center": v(650, -112.58) * mm, "radius": 26.5 * mm});
            skCircle(sketch, "E1838", {"center": v(682.5, -168.87) * mm, "radius": 26.5 * mm});
            skCircle(sketch, "E1839", {"center": v(715, -225.17) * mm, "radius": 26.5 * mm});
            skCircle(sketch, "E1840", {"center": v(747.5, -281.46) * mm, "radius": 26.5 * mm});
            skCircle(sketch, "E1841", {"center": v(780, -337.75) * mm, "radius": 26.5 * mm});
            skCircle(sketch, "E1842", {"center": v(812.5, -394.04) * mm, "radius": 26.5 * mm});
            skCircle(sketch, "E1843", {"center": v(845, -450.33) * mm, "radius": 26.5 * mm});
            skCircle(sketch, "E1844", {"center": v(877.5, -506.62) * mm, "radius": 26.5 * mm});
            skCircle(sketch, "E1845", {"center": v(975, -675.5) * mm, "radius": 26.5 * mm});
            skCircle(sketch, "E1846", {"center": v(1007.5, -731.8) * mm, "radius": 26.5 * mm});
            skCircle(sketch, "E1847", {"center": v(1040, -788.08) * mm, "radius": 26.5 * mm});
            skCircle(sketch, "E1848", {"center": v(1072.5, -844.37) * mm, "radius": 26.5 * mm});
            skCircle(sketch, "E1849", {"center": v(1105, -900.67) * mm, "radius": 26.5 * mm});
            skCircle(sketch, "E1850", {"center": v(1137.5, -956.96) * mm, "radius": 26.5 * mm});
            skCircle(sketch, "E1851", {"center": v(1170, -1013.25) * mm, "radius": 26.5 * mm});
            skCircle(sketch, "E1852", {"center": v(682.5, -56.3) * mm, "radius": 26.5 * mm});
            skCircle(sketch, "E1853", {"center": v(715, -112.58) * mm, "radius": 26.5 * mm});
            skCircle(sketch, "E1854", {"center": v(747.5, -168.87) * mm, "radius": 26.5 * mm});
            skCircle(sketch, "E1855", {"center": v(780, -225.17) * mm, "radius": 26.5 * mm});
            skCircle(sketch, "E1856", {"center": v(812.5, -281.46) * mm, "radius": 26.5 * mm});
            skCircle(sketch, "E1857", {"center": v(845, -337.75) * mm, "radius": 26.5 * mm});
            skCircle(sketch, "E1858", {"center": v(877.5, -394.04) * mm, "radius": 26.5 * mm});
            skCircle(sketch, "E1859", {"center": v(910, -450.33) * mm, "radius": 26.5 * mm});
            skCircle(sketch, "E1860", {"center": v(1040, -675.5) * mm, "radius": 26.5 * mm});
            skCircle(sketch, "E1861", {"center": v(1072.5, -731.8) * mm, "radius": 26.5 * mm});
            skCircle(sketch, "E1862", {"center": v(1105, -788.08) * mm, "radius": 26.5 * mm});
            skCircle(sketch, "E1863", {"center": v(1137.5, -844.37) * mm, "radius": 26.5 * mm});
            skCircle(sketch, "E1864", {"center": v(1170, -900.67) * mm, "radius": 26.5 * mm});
            skCircle(sketch, "E1865", {"center": v(1202.5, -956.96) * mm, "radius": 26.5 * mm});
            skCircle(sketch, "E1866", {"center": v(747.5, -56.3) * mm, "radius": 26.5 * mm});
            skCircle(sketch, "E1867", {"center": v(780, -112.58) * mm, "radius": 26.5 * mm});
            skCircle(sketch, "E1868", {"center": v(812.5, -168.87) * mm, "radius": 26.5 * mm});
            skCircle(sketch, "E1869", {"center": v(845, -225.17) * mm, "radius": 26.5 * mm});
            skCircle(sketch, "E1870", {"center": v(877.5, -281.46) * mm, "radius": 26.5 * mm});
            skCircle(sketch, "E1871", {"center": v(910, -337.75) * mm, "radius": 26.5 * mm});
            skCircle(sketch, "E1872", {"center": v(942.5, -394.04) * mm, "radius": 26.5 * mm});
            skCircle(sketch, "E1873", {"center": v(975, -450.33) * mm, "radius": 26.5 * mm});
            skCircle(sketch, "E1874", {"center": v(1072.5, -619.2) * mm, "radius": 26.5 * mm});
            skCircle(sketch, "E1875", {"center": v(1105, -675.5) * mm, "radius": 26.5 * mm});
            skCircle(sketch, "E1876", {"center": v(1137.5, -731.8) * mm, "radius": 26.5 * mm});
            skCircle(sketch, "E1877", {"center": v(1170, -788.08) * mm, "radius": 26.5 * mm});
            skCircle(sketch, "E1878", {"center": v(1202.5, -844.37) * mm, "radius": 26.5 * mm});
            skCircle(sketch, "E1879", {"center": v(1235, -900.67) * mm, "radius": 26.5 * mm});
            skCircle(sketch, "E1880", {"center": v(812.5, -56.3) * mm, "radius": 26.5 * mm});
            skCircle(sketch, "E1881", {"center": v(845, -112.58) * mm, "radius": 26.5 * mm});
            skCircle(sketch, "E1882", {"center": v(877.5, -168.87) * mm, "radius": 26.5 * mm});
            skCircle(sketch, "E1883", {"center": v(910, -225.17) * mm, "radius": 26.5 * mm});
            skCircle(sketch, "E1884", {"center": v(942.5, -281.46) * mm, "radius": 26.5 * mm});
            skCircle(sketch, "E1885", {"center": v(975, -337.75) * mm, "radius": 26.5 * mm});
            skCircle(sketch, "E1886", {"center": v(1007.5, -394.04) * mm, "radius": 26.5 * mm});
            skCircle(sketch, "E1887", {"center": v(1040, -450.33) * mm, "radius": 26.5 * mm});
            skCircle(sketch, "E1888", {"center": v(1072.5, -506.62) * mm, "radius": 26.5 * mm});
            skCircle(sketch, "E1889", {"center": v(1105, -562.92) * mm, "radius": 26.5 * mm});
            skCircle(sketch, "E1890", {"center": v(1137.5, -619.2) * mm, "radius": 26.5 * mm});
            skCircle(sketch, "E1891", {"center": v(1170, -675.5) * mm, "radius": 26.5 * mm});
            skCircle(sketch, "E1892", {"center": v(1202.5, -731.8) * mm, "radius": 26.5 * mm});
            skCircle(sketch, "E1893", {"center": v(1235, -788.08) * mm, "radius": 26.5 * mm});
            skCircle(sketch, "E1894", {"center": v(1267.5, -844.37) * mm, "radius": 26.5 * mm});
            skCircle(sketch, "E1895", {"center": v(877.5, -56.3) * mm, "radius": 26.5 * mm});
            skCircle(sketch, "E1896", {"center": v(910, -112.58) * mm, "radius": 26.5 * mm});
            skCircle(sketch, "E1897", {"center": v(942.5, -168.87) * mm, "radius": 26.5 * mm});
            skCircle(sketch, "E1898", {"center": v(975, -225.17) * mm, "radius": 26.5 * mm});
            skCircle(sketch, "E1899", {"center": v(1007.5, -281.46) * mm, "radius": 26.5 * mm});
            skCircle(sketch, "E1900", {"center": v(1040, -337.75) * mm, "radius": 26.5 * mm});
            skCircle(sketch, "E1901", {"center": v(1072.5, -394.04) * mm, "radius": 26.5 * mm});
            skCircle(sketch, "E1902", {"center": v(1105, -450.33) * mm, "radius": 26.5 * mm});
            skCircle(sketch, "E1903", {"center": v(1137.5, -506.62) * mm, "radius": 26.5 * mm});
            skCircle(sketch, "E1904", {"center": v(1170, -562.92) * mm, "radius": 26.5 * mm});
            skCircle(sketch, "E1905", {"center": v(1202.5, -619.2) * mm, "radius": 26.5 * mm});
            skCircle(sketch, "E1906", {"center": v(1235, -675.5) * mm, "radius": 26.5 * mm});
            skCircle(sketch, "E1907", {"center": v(1267.5, -731.8) * mm, "radius": 26.5 * mm});
            skCircle(sketch, "E1908", {"center": v(1300, -788.08) * mm, "radius": 26.5 * mm});
            skCircle(sketch, "E1909", {"center": v(1332.5, -844.37) * mm, "radius": 26.5 * mm});
            skCircle(sketch, "E1910", {"center": v(942.5, -56.3) * mm, "radius": 26.5 * mm});
            skCircle(sketch, "E1911", {"center": v(975, -112.58) * mm, "radius": 26.5 * mm});
            skCircle(sketch, "E1912", {"center": v(1007.5, -168.87) * mm, "radius": 26.5 * mm});
            skCircle(sketch, "E1913", {"center": v(1040, -225.17) * mm, "radius": 26.5 * mm});
            skCircle(sketch, "E1914", {"center": v(1072.5, -281.46) * mm, "radius": 26.5 * mm});
            skCircle(sketch, "E1915", {"center": v(1105, -337.75) * mm, "radius": 26.5 * mm});
            skCircle(sketch, "E1916", {"center": v(1137.5, -394.04) * mm, "radius": 26.5 * mm});
            skCircle(sketch, "E1917", {"center": v(1170, -450.33) * mm, "radius": 26.5 * mm});
            skCircle(sketch, "E1918", {"center": v(1202.5, -506.62) * mm, "radius": 26.5 * mm});
            skCircle(sketch, "E1919", {"center": v(1235, -562.92) * mm, "radius": 26.5 * mm});
            skCircle(sketch, "E1920", {"center": v(1267.5, -619.2) * mm, "radius": 26.5 * mm});
            skCircle(sketch, "E1921", {"center": v(1300, -675.5) * mm, "radius": 26.5 * mm});
            skCircle(sketch, "E1922", {"center": v(1332.5, -731.8) * mm, "radius": 26.5 * mm});
            skCircle(sketch, "E1923", {"center": v(1365, -788.08) * mm, "radius": 26.5 * mm});
            skCircle(sketch, "E1924", {"center": v(1007.5, -56.3) * mm, "radius": 26.5 * mm});
            skCircle(sketch, "E1925", {"center": v(1040, -112.58) * mm, "radius": 26.5 * mm});
            skCircle(sketch, "E1926", {"center": v(1072.5, -168.87) * mm, "radius": 26.5 * mm});
            skCircle(sketch, "E1927", {"center": v(1105, -225.17) * mm, "radius": 26.5 * mm});
            skCircle(sketch, "E1928", {"center": v(1137.5, -281.46) * mm, "radius": 26.5 * mm});
            skCircle(sketch, "E1929", {"center": v(1170, -337.75) * mm, "radius": 26.5 * mm});
            skCircle(sketch, "E1930", {"center": v(1202.5, -394.04) * mm, "radius": 26.5 * mm});
            skCircle(sketch, "E1931", {"center": v(1235, -450.33) * mm, "radius": 26.5 * mm});
            skCircle(sketch, "E1932", {"center": v(1267.5, -506.62) * mm, "radius": 26.5 * mm});
            skCircle(sketch, "E1933", {"center": v(1300, -562.92) * mm, "radius": 26.5 * mm});
            skCircle(sketch, "E1934", {"center": v(1332.5, -619.2) * mm, "radius": 26.5 * mm});
            skCircle(sketch, "E1935", {"center": v(1365, -675.5) * mm, "radius": 26.5 * mm});
            skCircle(sketch, "E1936", {"center": v(1397.5, -731.8) * mm, "radius": 26.5 * mm});
            skCircle(sketch, "E1937", {"center": v(1072.5, -56.3) * mm, "radius": 26.5 * mm});
            skCircle(sketch, "E1938", {"center": v(1105, -112.58) * mm, "radius": 26.5 * mm});
            skCircle(sketch, "E1939", {"center": v(1137.5, -168.87) * mm, "radius": 26.5 * mm});
            skCircle(sketch, "E1940", {"center": v(1170, -225.17) * mm, "radius": 26.5 * mm});
            skCircle(sketch, "E1941", {"center": v(1202.5, -281.46) * mm, "radius": 26.5 * mm});
            skCircle(sketch, "E1942", {"center": v(1235, -337.75) * mm, "radius": 26.5 * mm});
            skCircle(sketch, "E1943", {"center": v(1267.5, -394.04) * mm, "radius": 26.5 * mm});
            skCircle(sketch, "E1944", {"center": v(1300, -450.33) * mm, "radius": 26.5 * mm});
            skCircle(sketch, "E1945", {"center": v(1332.5, -506.62) * mm, "radius": 26.5 * mm});
            skCircle(sketch, "E1946", {"center": v(1365, -562.92) * mm, "radius": 26.5 * mm});
            skCircle(sketch, "E1947", {"center": v(1397.5, -619.2) * mm, "radius": 26.5 * mm});
            skCircle(sketch, "E1948", {"center": v(1137.5, -56.3) * mm, "radius": 26.5 * mm});
            skCircle(sketch, "E1949", {"center": v(1170, -112.58) * mm, "radius": 26.5 * mm});
            skCircle(sketch, "E1950", {"center": v(1202.5, -168.87) * mm, "radius": 26.5 * mm});
            skCircle(sketch, "E1951", {"center": v(1235, -225.17) * mm, "radius": 26.5 * mm});
            skCircle(sketch, "E1952", {"center": v(1267.5, -281.46) * mm, "radius": 26.5 * mm});
            skCircle(sketch, "E1953", {"center": v(1300, -337.75) * mm, "radius": 26.5 * mm});
            skCircle(sketch, "E1954", {"center": v(1332.5, -394.04) * mm, "radius": 26.5 * mm});
            skCircle(sketch, "E1955", {"center": v(1365, -450.33) * mm, "radius": 26.5 * mm});
            skCircle(sketch, "E1956", {"center": v(1397.5, -506.62) * mm, "radius": 26.5 * mm});
            skCircle(sketch, "E1957", {"center": v(1430, -562.92) * mm, "radius": 26.5 * mm});
            skCircle(sketch, "E1958", {"center": v(1202.5, -56.3) * mm, "radius": 26.5 * mm});
            skCircle(sketch, "E1959", {"center": v(1235, -112.58) * mm, "radius": 26.5 * mm});
            skCircle(sketch, "E1960", {"center": v(1267.5, -168.87) * mm, "radius": 26.5 * mm});
            skCircle(sketch, "E1961", {"center": v(1300, -225.17) * mm, "radius": 26.5 * mm});
            skCircle(sketch, "E1962", {"center": v(1332.5, -281.46) * mm, "radius": 26.5 * mm});
            skCircle(sketch, "E1963", {"center": v(1365, -337.75) * mm, "radius": 26.5 * mm});
            skCircle(sketch, "E1964", {"center": v(1397.5, -394.04) * mm, "radius": 26.5 * mm});
            skCircle(sketch, "E1965", {"center": v(1430, -450.33) * mm, "radius": 26.5 * mm});
            skCircle(sketch, "E1966", {"center": v(1462.5, -506.62) * mm, "radius": 26.5 * mm});
            skCircle(sketch, "E1967", {"center": v(1267.5, -56.3) * mm, "radius": 26.5 * mm});
            skCircle(sketch, "E1968", {"center": v(1300, -112.58) * mm, "radius": 26.5 * mm});
            skCircle(sketch, "E1969", {"center": v(1332.5, -168.87) * mm, "radius": 26.5 * mm});
            skCircle(sketch, "E1970", {"center": v(1365, -225.17) * mm, "radius": 26.5 * mm});
            skCircle(sketch, "E1971", {"center": v(1397.5, -281.46) * mm, "radius": 26.5 * mm});
            skCircle(sketch, "E1972", {"center": v(1430, -337.75) * mm, "radius": 26.5 * mm});
            skCircle(sketch, "E1973", {"center": v(1462.5, -394.04) * mm, "radius": 26.5 * mm});
            skCircle(sketch, "E1974", {"center": v(1495, -450.33) * mm, "radius": 26.5 * mm});
            skCircle(sketch, "E1975", {"center": v(1332.5, -56.3) * mm, "radius": 26.5 * mm});
            skCircle(sketch, "E1976", {"center": v(1365, -112.58) * mm, "radius": 26.5 * mm});
            skCircle(sketch, "E1977", {"center": v(1397.5, -168.87) * mm, "radius": 26.5 * mm});
            skCircle(sketch, "E1978", {"center": v(1430, -225.17) * mm, "radius": 26.5 * mm});
            skCircle(sketch, "E1979", {"center": v(1462.5, -281.46) * mm, "radius": 26.5 * mm});
            skCircle(sketch, "E1980", {"center": v(1495, -337.75) * mm, "radius": 26.5 * mm});
            skCircle(sketch, "E1981", {"center": v(1527.5, -394.04) * mm, "radius": 26.5 * mm});
            skCircle(sketch, "E1982", {"center": v(1397.5, -56.3) * mm, "radius": 26.5 * mm});
            skCircle(sketch, "E1983", {"center": v(1430, -112.58) * mm, "radius": 26.5 * mm});
            skCircle(sketch, "E1984", {"center": v(1462.5, -168.87) * mm, "radius": 26.5 * mm});
            skCircle(sketch, "E1985", {"center": v(1495, -225.17) * mm, "radius": 26.5 * mm});
            skCircle(sketch, "E1986", {"center": v(1527.5, -281.46) * mm, "radius": 26.5 * mm});
            skCircle(sketch, "E1987", {"center": v(1462.5, -56.3) * mm, "radius": 26.5 * mm});
            skCircle(sketch, "E1988", {"center": v(1495, -112.58) * mm, "radius": 26.5 * mm});
            skCircle(sketch, "E1989", {"center": v(1527.5, -168.87) * mm, "radius": 26.5 * mm});
            skCircle(sketch, "E1990", {"center": v(1560, -225.17) * mm, "radius": 26.5 * mm});
            skCircle(sketch, "E1991", {"center": v(1527.5, -56.3) * mm, "radius": 26.5 * mm});
            skCircle(sketch, "E1992", {"center": v(1560, -112.58) * mm, "radius": 26.5 * mm});
            skCircle(sketch, "E1993", {"center": v(975, -562.92) * mm, "radius": 58 * mm});
            skCircle(sketch, "E1994", {"center": v(0, 0) * mm, "radius": 2049 * mm});
            skCircle(sketch, "E1995", {"center": v(0, 0) * mm, "radius": 306.3 * mm});
            skSolve(sketch);
        }
        {
            var Q0;
            Q0=makeQuery(id+"F1.imprint","IMPRINT",FACE,{"disambiguationData":[TD([[makeQuery(id+"F1.imprint","IMPRINT",EDGE,{"derivedFrom":sQuery(id+"F1.wireOp",EDGE,"E0")}),1.0]])]});
            extrude(context, id + "F2", {"entities" : qUnion([Q0]), "depth" : (getVariable(context, 'F3')) * mm});
        }
    });
